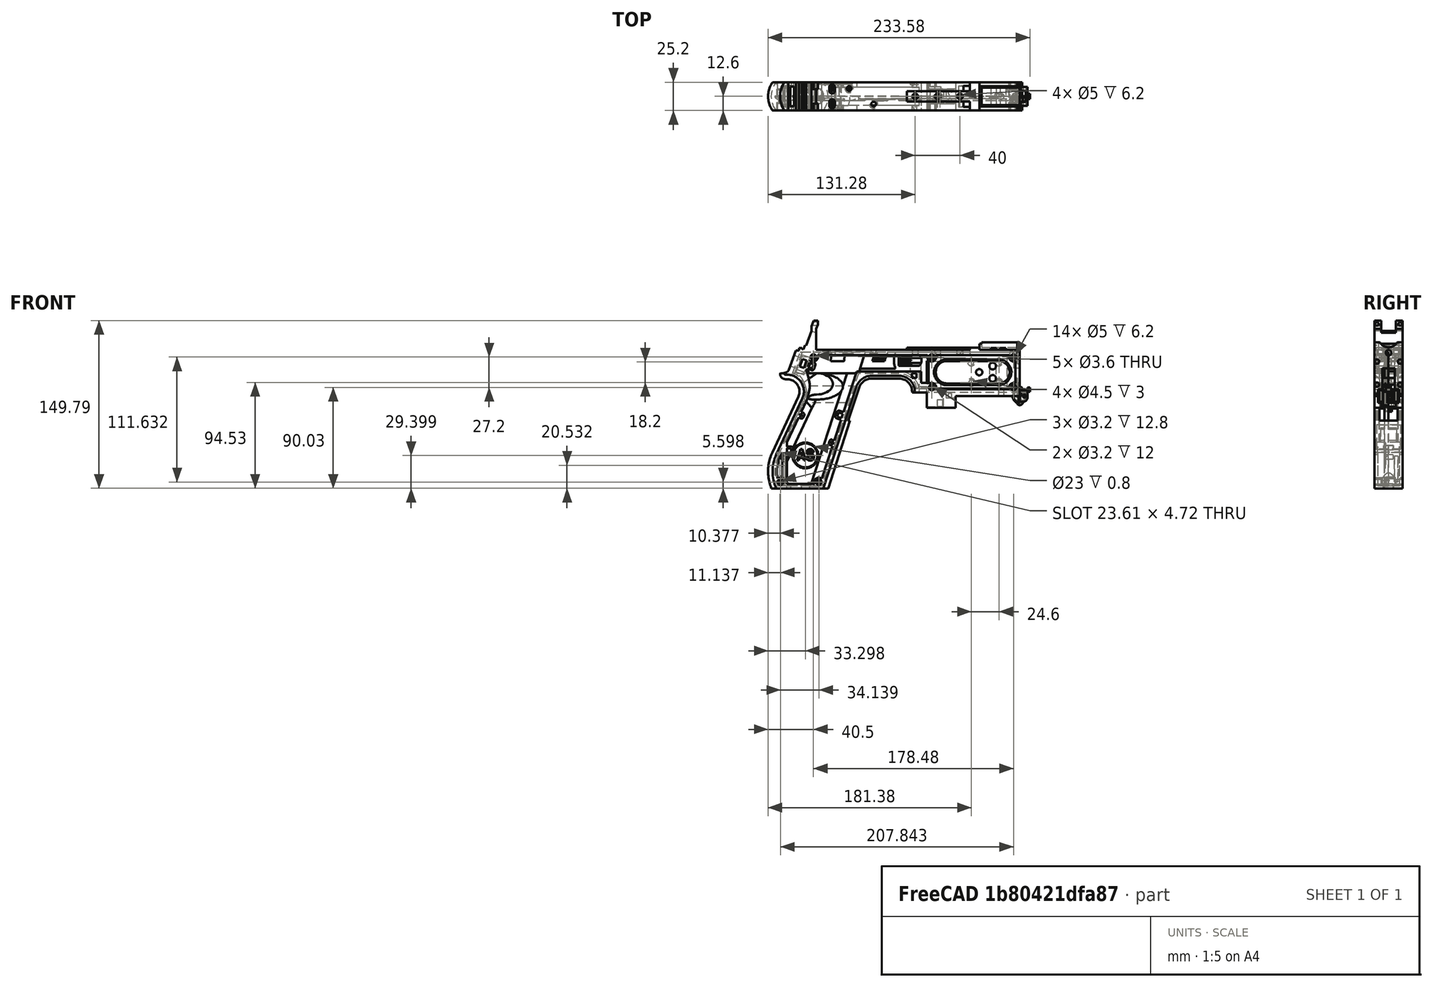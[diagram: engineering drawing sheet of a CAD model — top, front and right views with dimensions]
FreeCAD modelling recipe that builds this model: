
FCSTD DOCUMENT  (FreeCAD 1.0R39319 (Git))
Label: PICON-OF_ver_35
License: All rights reserved
LicenseURL: https://en.wikipedia.org/wiki/All_rights_reserved
objects: Sketcher::SketchObject×106, Part::Extrusion×61, Part::Cut×43, PartDesign::Pad×20, PartDesign::Pocket×14, PartDesign::Chamfer×14, PartDesign::Body×8, PartDesign::Fillet×6, Part::MultiFuse×4, PartDesign::SubtractivePipe×4, Part::Part2DObjectPython×4, PartDesign::SubtractiveLoft×4, PartDesign::Plane×2, PartDesign::SubShapeBinder×2, Part::Sweep×1, PartDesign::ShapeBinder×1, Part::Chamfer×1, Mesh::Feature×1
note: 525 computed .brp shape members not serialized (recipe doc carries the construction recipe); baked Part::Feature solids carry a one-line shape summary decoded from their .brp

FEATURE [Sketcher::SketchObject] Sketch  label="corpo principale"
  ArcFitTolerance = 1e-06
  AttacherType = Attacher::AttachEngine3D
  AttachmentSupport = -> [XZ_Plane]
  FullyConstrained = true
  MakeInternals = false
  MapMode = 5
  Placement = pos=(0,0,0) rot=(1,0,0;1.5708rad)
  sketch-geometry (65):
    g0: LineSegment StartX=0 StartY=0 StartZ=0 EndX=-57.2 EndY=0 EndZ=0
    g1: LineSegment StartX=-57.2 StartY=0 StartZ=0 EndX=-57.2 EndY=-10.4 EndZ=0
    g2: LineSegment StartX=-57.2 StartY=-10.4 StartZ=0 EndX=-82.8 EndY=-10.4 EndZ=0
    g3: LineSegment StartX=-82.8 StartY=-10.4 StartZ=0 EndX=-82.8 EndY=3.2 EndZ=0
    g4: LineSegment StartX=-82.8 StartY=3.2 StartZ=0 EndX=-93.6 EndY=3.2 EndZ=0
    g5: LineSegment StartX=-93.6 StartY=3.2 StartZ=0 EndX=-93.6 EndY=4 EndZ=0
    g6: LineSegment StartX=-107.6 StartY=18 StartZ=0 EndX=-132.428 EndY=18 EndZ=0
    g7: LineSegment StartX=-145.743 StartY=8.32624 StartZ=0 EndX=-175.232 EndY=-82.4316 EndZ=0
    g8: LineSegment StartX=-175.232 StartY=-82.4316 StartZ=0 EndX=-217.232 EndY=-82.4316 EndZ=0
    g9: LineSegment StartX=-217.232 StartY=-52.1862 StartZ=0 EndX=-193.988 EndY=-2.33927 EndZ=0
    g10: LineSegment StartX=-206.196 StartY=23.0857 StartZ=0 EndX=-199.861 EndY=40.4914 EndZ=0
    g11: LineSegment StartX=-199.861 StartY=40.4914 StartZ=0 EndX=-197.061 EndY=40.4914 EndZ=0
    g12: LineSegment StartX=-197.061 StartY=40.4914 StartZ=0 EndX=-197.061 EndY=42.8914 EndZ=0
    g13: LineSegment StartX=-197.061 StartY=42.8914 StartZ=0 EndX=-194.261 EndY=42.8914 EndZ=0
    g14: LineSegment StartX=-194.261 StartY=42.8914 StartZ=0 EndX=-194.535 EndY=42.1397 EndZ=0
    g15: LineSegment StartX=-194.535 StartY=42.1397 StartZ=0 EndX=-193.031 EndY=41.5924 EndZ=0
    g16: LineSegment StartX=-193.031 StartY=41.5924 StartZ=0 EndX=-191.663 EndY=45.3512 EndZ=0
    g17: LineSegment StartX=-191.663 StartY=45.3512 StartZ=0 EndX=-190.536 EndY=44.9408 EndZ=0
    g18: LineSegment StartX=-190.536 StartY=44.9408 StartZ=0 EndX=-185.747 EndY=58.0965 EndZ=0
    g19: LineSegment StartX=-185.747 StartY=58.0965 StartZ=0 EndX=-185.747 EndY=62.0965 EndZ=0
    g20: LineSegment StartX=-185.747 StartY=62.0965 StartZ=0 EndX=-183.832 EndY=67.3588 EndZ=0
    g21: LineSegment StartX=-183.832 StartY=67.3588 StartZ=0 EndX=-180.232 EndY=67.3588 EndZ=0
    g22: LineSegment StartX=-180.232 StartY=67.3588 StartZ=0 EndX=-180.232 EndY=63.7588 EndZ=0
    g23: LineSegment StartX=-180.232 StartY=63.7588 StartZ=0 EndX=-181.6 EndY=60 EndZ=0
    g24: LineSegment StartX=-181.6 StartY=60 StartZ=0 EndX=-181.6 EndY=41.2 EndZ=0
    g25: LineSegment StartX=-181.6 StartY=41.2 StartZ=0 EndX=-100.8 EndY=41.2 EndZ=0
    g26: LineSegment StartX=-36 StartY=43.2 StartZ=0 EndX=-36 EndY=41.2 EndZ=0
    g27: LineSegment StartX=0 StartY=48 StartZ=0 EndX=0 EndY=0 EndZ=0
    g28: LineSegment StartX=-209.901 StartY=19.85 StartZ=0 EndX=-209.901 EndY=20.1 EndZ=0
    g29: LineSegment StartX=-208.001 StartY=22 StartZ=0 EndX=-207.747 EndY=22 EndZ=0
    g30: LineSegment StartX=-207.583 StartY=19 StartZ=0 EndX=-209.051 EndY=19 EndZ=0
    g31: ArcOfCircle CenterX=-208.001 CenterY=20.1 CenterZ=0 NormalX=0 NormalY=0 NormalZ=1 AngleXU=0 Radius=1.9 StartAngle=1.5708 EndAngle=3.14159
    g32: GeomPoint [constr] X=-209.901 Y=22 Z=0
    g33: ArcOfCircle CenterX=-209.051 CenterY=19.85 CenterZ=0 NormalX=0 NormalY=0 NormalZ=1 AngleXU=0 Radius=0.85 StartAngle=3.14159 EndAngle=4.71239
    g34: GeomPoint [constr] X=-209.901 Y=19 Z=0
    g35: ArcOfCircle CenterX=-207.747 CenterY=23.65 CenterZ=0 NormalX=0 NormalY=0 NormalZ=1 AngleXU=0 Radius=1.65 StartAngle=4.71239 EndAngle=5.93412
    g36: GeomPoint [constr] X=-206.591 Y=22 Z=0
    g37: LineSegment StartX=-4 StartY=6 StartZ=0 EndX=-4 EndY=36.4 EndZ=0
    g38: LineSegment StartX=-4 StartY=36.4 StartZ=0 EndX=-185.2 EndY=36.4 EndZ=0
    g39: LineSegment StartX=-185.2 StartY=36.4 StartZ=0 EndX=-190.441 EndY=22 EndZ=0
    g40: LineSegment StartX=-214.575 StartY=-78.4316 StartZ=0 EndX=-178.142 EndY=-78.4316 EndZ=0
    g41: LineSegment StartX=-178.142 StartY=-78.4316 StartZ=0 EndX=-145.51 EndY=22 EndZ=0
    g42: LineSegment StartX=-145.51 StartY=22 StartZ=0 EndX=-87.91 EndY=22 EndZ=0
    g43: LineSegment StartX=-87.91 StartY=22 StartZ=0 EndX=-87.91 EndY=11.6 EndZ=0
    g44: LineSegment StartX=-87.91 StartY=11.6 StartZ=0 EndX=-80.11 EndY=11.6 EndZ=0
    g45: LineSegment StartX=-80.11 StartY=11.6 StartZ=0 EndX=-80.11 EndY=6 EndZ=0
    g46: LineSegment StartX=-80.11 StartY=6 StartZ=0 EndX=-4 EndY=6 EndZ=0
    g47: LineSegment StartX=-190.363 StartY=-4.02975 StartZ=0 EndX=-213.607 EndY=-53.8767 EndZ=0
    g48: ArcOfCircle CenterX=-132.428 CenterY=4 CenterZ=0 NormalX=0 NormalY=0 NormalZ=1 AngleXU=0 Radius=14 StartAngle=1.5708 EndAngle=2.82743
    g49: GeomPoint [constr] X=-142.6 Y=18 Z=0
    g50: ArcOfCircle CenterX=-107.6 CenterY=4 CenterZ=0 NormalX=0 NormalY=0 NormalZ=1 AngleXU=0 Radius=14 StartAngle=0 EndAngle=1.5708
    g51: GeomPoint [constr] X=-93.6 Y=18 Z=0
    g52: ArcOfCircle CenterX=-184.801 CenterY=-67.3089 CenterZ=0 NormalX=0 NormalY=0 NormalZ=1 AngleXU=0 Radius=35.7833 StartAngle=2.70526 EndAngle=3.57792
    g53: ArcOfCircle CenterX=-207.583 CenterY=4 CenterZ=0 NormalX=0 NormalY=0 NormalZ=1 AngleXU=0 Radius=15 StartAngle=5.84685 EndAngle=7.85398
    g54: LineSegment [constr] StartX=-213.607 StartY=-53.8767 StartZ=0 EndX=-217.232 EndY=-52.1862 EndZ=0
    g55: ArcOfCircle CenterX=-184.801 CenterY=-67.3089 CenterZ=0 NormalX=0 NormalY=0 NormalZ=1 AngleXU=0 Radius=31.7833 StartAngle=2.70526 EndAngle=3.49911
    g56: ArcOfCircle CenterX=-218.095 CenterY=8.90192 CenterZ=0 NormalX=0 NormalY=0 NormalZ=1 AngleXU=0 Radius=30.5989 StartAngle=5.84685 EndAngle=6.72553
    g57: LineSegment StartX=-44.6 StartY=43.2 StartZ=0 EndX=-36 EndY=43.2 EndZ=0
    g58: LineSegment StartX=-100.8 StartY=41.2 StartZ=0 EndX=-44.6 EndY=41.2 EndZ=0
    g59: LineSegment StartX=-44.6 StartY=41.2 StartZ=0 EndX=-44.6 EndY=43.2 EndZ=0
    g60: LineSegment StartX=-2.4 StartY=48 StartZ=0 EndX=0 EndY=48 EndZ=0
    g61: LineSegment StartX=-36 StartY=41.2 StartZ=0 EndX=-2.4 EndY=41.2 EndZ=0
    g62: LineSegment StartX=-2.4 StartY=41.2 StartZ=0 EndX=-2.4 EndY=48 EndZ=0
    g63: LineSegment [constr] StartX=-181.6 StartY=36.4 StartZ=0 EndX=-152.209 EndY=36.4 EndZ=0
    g64: LineSegment [constr] StartX=-181.6 StartY=36.4 StartZ=0 EndX=-130.41 EndY=36.4 EndZ=0
  constraints (183):
    c: Coincident(g-1,g0)
    c: PointOnObject(g0,g-1)
    c: Coincident(g0,g1)
    c: Vertical(g1)
    c: Coincident(g1,g2)
    c: Horizontal(g2)
    c: Coincident(g2,g3)
    c: Vertical(g3)
    c: Coincident(g3,g4)
    c: Coincident(g4,g5)
    c: Vertical(g5)
    c: Horizontal(g6)
    c: Coincident(g7,g8)
    c: Horizontal(g8)
    c: Coincident(g10,g11)
    c: Horizontal(g11)
    c: Coincident(g11,g12)
    c: Vertical(g12)
    c: Coincident(g12,g13)
    c: Horizontal(g13)
    c: Coincident(g13,g14)
    c: Coincident(g14,g15)
    c: Coincident(g15,g16)
    c: Coincident(g16,g17)
    c: Coincident(g17,g18)
    c: Coincident(g18,g19)
    c: Vertical(g19)
    c: Coincident(g19,g20)
    c: Coincident(g20,g21)
    c: Horizontal(g21)
    c: Coincident(g21,g22)
    c: Vertical(g22)
    c: Coincident(g22,g23)
    c: Coincident(g23,g24)
    c: Vertical(g24)
    c: Coincident(g24,g25)
    c: Horizontal(g25)
    c: Coincident(g57,g26)
    c: Vertical(g26)
    c: Coincident(g26,g61)
    c: PointOnObject(g60,g-2)
    c: Coincident(g60,g27)
    c: Coincident(g27,g0)
    c: DistanceY(g27,g27) = 48
    c: DistanceY(g1,g1) = 10.4
    c: DistanceX(g0,g0) = 57.2
    c: DistanceX(g2,g2) = 25.6
    c: Horizontal(g4)
    c: DistanceY(g3,g3) = 13.6
    c: DistanceX(g4,g4) = 10.8
    c: DistanceY(g5,g51) = 14.8
    c: DistanceX(g49,g51) = 49
    c: Distance(g7,g49) = 105.6
    c: DistanceX(g61,g60) = 36
    c: DistanceX(g25,g25) = 80.8
    c: DistanceY(g24,g24) = 18.8
    c: DistanceY(g22,g22) = 3.6
    c: Distance(g23) = 4
    c: Angle(g-1,g23) = 1.22173
    c: DistanceX(g21,g21) = 3.6
    c: Distance(g20) = 5.6
    c: Angle(g-1,g20) = 1.22173
    c: DistanceY(g19,g19) = 4
    c: Distance(g18) = 14
    c: Angle(g-1,g18) = 1.22173
    c: Distance(g17) = 1.2
    c: Distance(g16) = 4
    c: Angle(g16) = 1.22173
    c: Perpendicular(g18,g17)
    c: Distance(g15) = 1.6
    c: Perpendicular(g16,g15)
    c: Distance(g14) = 0.8
    c: DistanceX(g13,g13) = 2.8
    c: Perpendicular(g15,g14)
    c: DistanceY(g12,g12) = 2.4
    c: DistanceX(g11,g11) = 2.8
    c: Distance(g9) = 55
    c: Angle(g9,g-1) = 2.00713
    c: Horizontal(g29)
    c: Vertical(g28)
    c: Horizontal(g30)
    c: PointOnObject(g32,g29)
    c: PointOnObject(g32,g28)
    c: Tangent(g29,g31) = 1.5708
    c: Tangent(g28,g31) = 1.5708
    c: PointOnObject(g34,g28)
    c: PointOnObject(g34,g30)
    c: Tangent(g28,g33) = 1.5708
    c: Tangent(g30,g33) = 1.5708
    c: PointOnObject(g36,g29)
    c: PointOnObject(g36,g10)
    c: Tangent(g29,g35) = -1.5708
    c: Tangent(g10,g35) = -1.5708
    c: Angle(g-1,g10) = 1.22173
    c: Radius(g35) = 1.65
    c: Vertical(g37)
    c: Coincident(g37,g38)
    c: Horizontal(g38)
    c: Coincident(g38,g39)
    c: Horizontal(g40)
    c: Coincident(g40,g41)
    c: Coincident(g41,g42)
    c: Horizontal(g42)
    c: Coincident(g42,g43)
    c: Vertical(g43)
    c: Coincident(g43,g44)
    c: Horizontal(g44)
    c: Coincident(g44,g45)
    c: Vertical(g45)
    c: Coincident(g45,g46)
    c: Coincident(g46,g37)
    c: Horizontal(g46)
    c: DistanceY(g0,g37) = 6
    c: DistanceX(g37,g0) = 4
    c: DistanceY(g37,g25) = 4.8
    c: DistanceX(g38,g38) = 181.2
    c: DistanceX(g42,g42) = 57.6
    c: DistanceY(g49,g41) = 4
    c: DistanceX(g41,g49) = 2.91
    c: DistanceY(g43,g43) = 10.4
    c: DistanceX(g44,g44) = 7.8
    c: DistanceY(g7,g40) = 4
    c: Distance(g47) = 55
    c: Angle(g-1,g39) = 1.22173
    c: PointOnObject(g49,g7)
    c: PointOnObject(g49,g6)
    c: Tangent(g7,g48) = -1.5708
    c: Tangent(g6,g48) = -1.5708
    c: PointOnObject(g51,g5)
    c: PointOnObject(g51,g6)
    c: Tangent(g5,g50) = -1.5708
    c: Tangent(g6,g50) = -1.5708
    c: Radius(g50) = 14
    c: Radius(g48) = 14
    c: DistanceX(g8,g8) = 42
    c: Angle(g7,g-1) = 1.88496
    c: Parallel(g41,g7)
    c: Parallel(g47,g9)
    c: Coincident(g52,g8)
    c: Tangent(g52,g9) = 1.5708
    c: DistanceX(g9,g8) = 0
    c: Tangent(g53,g9) = -1.5708
    c: Tangent(g53,g30) = -1.5708
    c: Diameter(g53) = 30
    c: DistanceY(g53,g0) = -4
    c: Coincident(g54,g47)
    c: Distance(g54) = 4
    c: Coincident(g54,g9)
    c: Coincident(g55,g40)
    c: Tangent(g55,g47) = -1.5708
    c: Coincident(g52,g55)
    c: Coincident(g56,g39)
    c: Tangent(g56,g47) = 1.5708
    c: Horizontal(g57)
    c: DistanceX(g57,g57) = 8.6
    c: Coincident(g58,g25)
    c: Horizontal(g58)
    c: Coincident(g59,g58)
    c: Vertical(g59)
    c: DistanceY(g58,g57) = 2
    c: DistanceX(g58,g58) = 56.2
    c: Coincident(g59,g57)
    c: DistanceY(g41,g36) = 0
    c: DistanceY(g36,g39) = 0
    c: DistanceY(g28,g28) = 0.25
    c: DistanceX(g30,g36) = 2.46
    c: DistanceX(g28,g29) = 1.9
    c: Coincident(g62,g60)
    c: Horizontal(g60)
    c: DistanceX(g62,g27) = 2.4
    c: Coincident(g61,g62)
    c: DistanceY(g26,g26) = 2
    c: Vertical(g62)
    c: DistanceY(g61,g60) = 6.8
    c: Horizontal(g61)
    c: Distance(g63) = 29.391
    c: PointOnObject(g63,g38)
    c: PointOnObject(g63,g38)
    c: Distance(g64) = 51.19
    c: PointOnObject(g64,g38)
    c: PointOnObject(g64,g38)
    c: DistanceX(g24,g63) = 0
    c: DistanceX(g24,g64) = 0
FEATURE [Part::Extrusion] Extrude  label="Extrude corpo principale"
  Base = -> Sketch
  Dir = (0,-1,2e-16)
  DirMode = 2
  FaceMakerClass = Part::FaceMakerBullseye
  FaceMakerMode = 3
  LengthFwd = 25.2
  LengthRev = 12.6
  Solid = true
  Symmetric = true
FEATURE [Sketcher::SketchObject] Sketch002  label="scavo grilletto"
  ArcFitTolerance = 1e-06
  AttachmentSupport = -> [XZ_Plane]
  ExternalGeometry = -> [Sketch]
  FullyConstrained = true
  MakeInternals = false
  MapMode = 5
  Placement = pos=(0,0,0) rot=(1,0,0;1.5708rad)
  sketch-geometry (4):
    g0: LineSegment StartX=-89.51 StartY=22 StartZ=0 EndX=-152.71 EndY=22 EndZ=0
    g1: LineSegment StartX=-152.71 StartY=22 StartZ=0 EndX=-167.006 EndY=-22 EndZ=0
    g2: LineSegment StartX=-167.006 StartY=-22 StartZ=0 EndX=-89.51 EndY=-22 EndZ=0
    g3: LineSegment StartX=-89.51 StartY=-22 StartZ=0 EndX=-89.51 EndY=22 EndZ=0
  constraints (12):
    c: Horizontal(g0)
    c: Coincident(g0,g1)
    c: Coincident(g1,g2)
    c: Horizontal(g2)
    c: Coincident(g2,g3)
    c: Coincident(g3,g0)
    c: Vertical(g3)
    c: Angle(g1,g0) = 1.88496
    c: DistanceY(g3,g3) = 44
    c: DistanceX(g0,g0) = 63.2
    c: DistanceX(g0,g-3) = 1.6
    c: DistanceY(g-3,g0) = 0
FEATURE [Sketcher::SketchObject] Sketch004  label="traiettoria arrotondamento impugnatura anteriore"
  ArcFitTolerance = 1e-06
  AttachmentSupport = -> [XZ_Plane]
  ExternalGeometry = -> [Sketch]
  FullyConstrained = true
  MakeInternals = false
  MapMode = 5
  Placement = pos=(0,0,0) rot=(1,0,0;1.5708rad)
  sketch-geometry (13):
    g0: LineSegment StartX=-175.232 StartY=-82.4316 StartZ=0 EndX=-145.743 EndY=8.32624 EndZ=0
    g1: LineSegment StartX=-93.6 StartY=3.2 StartZ=0 EndX=-93.6 EndY=4 EndZ=0
    g2: LineSegment StartX=-132.428 StartY=18 StartZ=0 EndX=-107.6 EndY=18 EndZ=0
    g3: ArcOfCircle CenterX=-132.428 CenterY=4 CenterZ=0 NormalX=0 NormalY=0 NormalZ=1 AngleXU=0 Radius=14 StartAngle=1.5708 EndAngle=2.82743
    g4: ArcOfCircle CenterX=-107.6 CenterY=4 CenterZ=0 NormalX=0 NormalY=0 NormalZ=1 AngleXU=0 Radius=14 StartAngle=0 EndAngle=1.5708
    g5: LineSegment StartX=-175.232 StartY=-82.4316 StartZ=0 EndX=-217.232 EndY=-82.4316 EndZ=0
    g6: LineSegment StartX=-217.232 StartY=-52.1862 StartZ=0 EndX=-193.988 EndY=-2.33927 EndZ=0
    g7: LineSegment StartX=-209.051 StartY=19 StartZ=0 EndX=-207.583 EndY=19 EndZ=0
    g8: LineSegment StartX=-209.901 StartY=20.1 StartZ=0 EndX=-209.901 EndY=19.85 EndZ=0
    g9: ArcOfCircle CenterX=-184.801 CenterY=-67.3089 CenterZ=0 NormalX=0 NormalY=0 NormalZ=1 AngleXU=0 Radius=35.7833 StartAngle=2.70526 EndAngle=3.57792
    g10: ArcOfCircle CenterX=-207.583 CenterY=4 CenterZ=0 NormalX=0 NormalY=0 NormalZ=1 AngleXU=0 Radius=15 StartAngle=5.84685 EndAngle=7.85398
    g11: ArcOfCircle CenterX=-209.051 CenterY=19.85 CenterZ=0 NormalX=0 NormalY=0 NormalZ=1 AngleXU=0 Radius=0.85 StartAngle=3.14159 EndAngle=4.71239
    g12: ArcOfCircle CenterX=-208.001 CenterY=20.1 CenterZ=0 NormalX=0 NormalY=0 NormalZ=1 AngleXU=0 Radius=1.9 StartAngle=1.5708 EndAngle=3.14159
  constraints (26):
    c: Coincident(g0,g-3)
    c: Coincident(g0,g-6)
    c: Coincident(g1,g-8)
    c: Coincident(g1,g-7)
    c: Coincident(g2,g-5)
    c: Coincident(g2,g-4)
    c: Coincident(g3,g2)
    c: Tangent(g3,g0) = 1.5708
    c: Coincident(g4,g1)
    c: Tangent(g4,g2) = 1.5708
    c: Coincident(g5,g0)
    c: Coincident(g5,g-9)
    c: Coincident(g6,g-12)
    c: Coincident(g6,g-11)
    c: Coincident(g7,g-15)
    c: Coincident(g7,g-14)
    c: Coincident(g8,g-16)
    c: Coincident(g8,g-17)
    c: Tangent(g9,g6) = 1.5708
    c: Coincident(g9,g5)
    c: Coincident(g10,g7)
    c: Tangent(g10,g6) = -1.5708
    c: Tangent(g11,g7) = -1.5708
    c: Coincident(g11,g8)
    c: Tangent(g12,g8) = -1.5708
    c: Coincident(g12,g-17)
FEATURE [PartDesign::Plane] DatumPlane  label="Piano per disegno arrotondamento impugnatura"
  AttachmentSupport = -> [Sketch]
  Length = 68.5841
  MapMode = 7
  Placement = pos=(-145.743,1.8e-15,8.32624) rot=(0.154555,0.154555,0.97582;1.59527rad)
  ResizeMode = 0
  Width = 191.269
FEATURE [Sketcher::SketchObject] Sketch005  label="forma arrotondamento impugnatura anteriore"
  ArcFitTolerance = 1e-06
  AttachmentSupport = -> [DatumPlane]
  FullyConstrained = true
  MakeInternals = false
  MapMode = 5
  Placement = pos=(-145.743,1.8e-15,8.32624) rot=(0.154555,0.154555,0.97582;1.59527rad)
  sketch-geometry (5):
    g0: GeomPoint [constr] X=0 Y=-4 Z=0
    g1: GeomPoint [constr] X=-12.6 Y=7.1e-15 Z=0
    g2: GeomPoint [constr] X=12.6 Y=4.97e-14 Z=0
    g3: LineSegment StartX=-12.6 StartY=7.1e-15 StartZ=0 EndX=12.6 EndY=4.97e-14 EndZ=0
    g4: ArcOfCircle CenterX=-3.88e-14 CenterY=17.845 CenterZ=0 NormalX=0 NormalY=0 NormalZ=1 AngleXU=0 Radius=21.845 StartAngle=4.09759 EndAngle=5.32718
  constraints (11):
    c: DistanceY(g0,g-1) = 4
    c: DistanceX(g-1,g0) = 0
    c: DistanceX(g1,g-1) = 12.6
    c: DistanceX(g-1,g2) = 12.6
    c: DistanceY(g-1,g2) = 0
    c: DistanceY(g-1,g1) = 0
    c: Coincident(g3,g1)
    c: Coincident(g3,g2)
    c: Coincident(g4,g1)
    c: Coincident(g4,g2)
    c: PointOnObject(g0,g4)
FEATURE [Part::Sweep] Sweep  label="Sweep impugnatura"
  Frenet = true
  Sections = -> [Sketch005]
  Solid = true
  Spine = -> Sketch [Edge32,Edge33,Edge34,Edge35,Edge36,Edge37,Edge38,Edge39,Edge40,Edge41,Edge42,Edge43,Edge44]
  Transition = 1
FEATURE [Sketcher::SketchObject] Sketch008  label="buchi e pulizie varie"
  ArcFitTolerance = 1e-06
  AttachmentSupport = -> [XZ_Plane]
  ExternalGeometry = -> [Sketch]
  FullyConstrained = true
  MakeInternals = false
  MapMode = 5
  Placement = pos=(0,0,0) rot=(1,0,0;1.5708rad)
  sketch-geometry (26):
    g0: LineSegment StartX=-96.278 StartY=20.155 StartZ=0 EndX=-92.278 EndY=20.155 EndZ=0
    g1: LineSegment StartX=-92.278 StartY=20.155 StartZ=0 EndX=-92.278 EndY=16.155 EndZ=0
    g2: LineSegment StartX=-92.278 StartY=16.155 StartZ=0 EndX=-96.278 EndY=16.155 EndZ=0
    g3: LineSegment StartX=-96.278 StartY=16.155 StartZ=0 EndX=-96.278 EndY=20.155 EndZ=0
    g4: LineSegment StartX=-222.232 StartY=-82.4316 StartZ=0 EndX=-170.232 EndY=-82.4316 EndZ=0
    g5: LineSegment StartX=-170.232 StartY=-82.4316 StartZ=0 EndX=-170.232 EndY=-86.4316 EndZ=0
    g6: LineSegment StartX=-170.232 StartY=-86.4316 StartZ=0 EndX=-222.232 EndY=-86.4316 EndZ=0
    g7: LineSegment StartX=-222.232 StartY=-86.4316 StartZ=0 EndX=-222.232 EndY=-82.4316 EndZ=0
    g8: LineSegment StartX=-213.901 StartY=20.1 StartZ=0 EndX=-213.901 EndY=26 EndZ=0
    g9: LineSegment StartX=-213.901 StartY=26 StartZ=0 EndX=-206.196 EndY=26 EndZ=0
    g10: LineSegment StartX=-17.4 StartY=42.8 StartZ=0 EndX=-12.4 EndY=42.8 EndZ=0
    g11: LineSegment StartX=-12.4 StartY=42.8 StartZ=0 EndX=-12.4 EndY=41.2 EndZ=0
    g12: LineSegment StartX=-12.4 StartY=41.2 StartZ=0 EndX=-17.4 EndY=41.2 EndZ=0
    g13: LineSegment StartX=-17.4 StartY=41.2 StartZ=0 EndX=-17.4 EndY=42.8 EndZ=0
    g14: LineSegment StartX=-25.9 StartY=42.8 StartZ=0 EndX=-20.9 EndY=42.8 EndZ=0
    g15: LineSegment StartX=-20.9 StartY=42.8 StartZ=0 EndX=-20.9 EndY=41.2 EndZ=0
    g16: LineSegment StartX=-20.9 StartY=41.2 StartZ=0 EndX=-25.9 EndY=41.2 EndZ=0
    g17: LineSegment StartX=-25.9 StartY=41.2 StartZ=0 EndX=-25.9 EndY=42.8 EndZ=0
    g18: GeomPoint [constr] X=-206.196 Y=23.0857 Z=0
    g19: GeomPoint [constr] X=-213.901 Y=20.1 Z=0
    g20: BSplineCurve PolesCount=4 KnotsCount=2 Degree=3 IsPeriodic=0
    g21-g24: Circle [constr] x4 (B-spline internal-alignment scaffolding for g20; pole/knot coordinates omitted)
    g25: LineSegment StartX=-206.196 StartY=26 StartZ=0 EndX=-206.196 EndY=23.0857 EndZ=0
  constraints (73):
    c: Horizontal(g0)
    c: Coincident(g1,g0)
    c: Vertical(g1)
    c: Coincident(g2,g1)
    c: Horizontal(g2)
    c: Coincident(g3,g2)
    c: Coincident(g3,g0)
    c: Vertical(g3)
    c: DistanceX(g0,g-4) = 4.368
    c: DistanceY(g0,g-4) = 1.845
    c: DistanceY(g1,g1) = 4
    c: DistanceX(g2,g2) = 4
    c: Horizontal(g4)
    c: Coincident(g5,g4)
    c: Vertical(g5)
    c: Coincident(g6,g5)
    c: Horizontal(g6)
    c: Coincident(g7,g6)
    c: Coincident(g7,g4)
    c: Vertical(g7)
    c: DistanceY(g7,g7) = 4
    c: DistanceX(g4,g-5) = 5
    c: DistanceX(g-5,g4) = 5
    c: DistanceY(g4,g-5) = 0
    c: Coincident(g9,g8)
    c: Parallel(g9,g-6)
    c: DistanceX(g8,g-8) = 4
    c: Horizontal(g10)
    c: Coincident(g11,g10)
    c: Vertical(g11)
    c: Coincident(g12,g11)
    c: Horizontal(g12)
    c: Coincident(g13,g12)
    c: Coincident(g13,g10)
    c: Vertical(g13)
    c: Horizontal(g14)
    c: Coincident(g15,g14)
    c: Vertical(g15)
    c: Coincident(g16,g15)
    c: Horizontal(g16)
    c: Coincident(g17,g16)
    c: Coincident(g17,g14)
    c: Vertical(g17)
    c: DistanceY(g11,g10) = 1.6
    c: DistanceX(g10,g10) = 5
    c: DistanceY(g15,g14) = 1.6
    c: DistanceX(g14,g14) = 5
    c: DistanceX(g15,g12) = 3.5
    c: DistanceX(g11,g-9) = 10
    c: DistanceY(g-9,g11) = 0
    c: DistanceY(g-9,g15) = 0
    c: Perpendicular(g8,g9)
    c: DistanceY(g-7,g9) = 4
    c: DistanceY(g8,g-8) = 0
    c: InternalAlignment(g18,g20)
    c: InternalAlignment(g19,g20)
    c: InternalAlignment(g21,g20)
    c: Weight(g21) = 1
    c: InternalAlignment(g22,g20)
    c: Equal(g22,g21)
    c: InternalAlignment(g23,g20)
    c: Equal(g23,g21)
    c: InternalAlignment(g24,g20)
    c: Equal(g24,g21)
    c: Coincident(g18,g-12)
    c: Coincident(g19,g8)
    c: Coincident(g25,g9)
    c: Coincident(g25,g20)
    c: Vertical(g25)
    c: DistanceY(g20,g23) = 0
    c: DistanceY(g22,g18) = 2.26
    c: DistanceX(g22,g18) = 0.93
    c: DistanceX(g20,g23) = 2.9
FEATURE [Part::Extrusion] Extrude004  label="Extrude Buchi e pulizie varie"
  Base = -> Sketch008
  Dir = (0,-1,2e-16)
  DirMode = 2
  FaceMakerClass = Part::FaceMakerBullseye
  FaceMakerMode = 3
  LengthFwd = 25.2
  LengthRev = 0
  Solid = true
  Symmetric = true
FEATURE [Sketcher::SketchObject] Sketch009  label="rinforzi"
  ArcFitTolerance = 1e-06
  AttachmentSupport = -> [XZ_Plane]
  ExternalGeometry = -> [Sketch]
  FullyConstrained = true
  MakeInternals = false
  MapMode = 5
  Placement = pos=(0,0,0) rot=(1,0,0;1.5708rad)
  sketch-geometry (9):
    g0: LineSegment StartX=-87.91 StartY=22 StartZ=0 EndX=-87.91 EndY=36.4 EndZ=0
    g1: LineSegment StartX=-87.91 StartY=36.4 StartZ=0 EndX=-97.91 EndY=36.4 EndZ=0
    g2: LineSegment StartX=-97.91 StartY=36.4 StartZ=0 EndX=-97.91 EndY=22 EndZ=0
    g3: LineSegment StartX=-97.91 StartY=22 StartZ=0 EndX=-87.91 EndY=22 EndZ=0
    g4: LineSegment StartX=-149.713 StartY=9.06563 StartZ=0 EndX=-154.586 EndY=-5.93437 EndZ=0
    g5: LineSegment StartX=-154.586 StartY=-5.93437 StartZ=0 EndX=-191.863 EndY=-5.93437 EndZ=0
    g6: LineSegment StartX=-191.863 StartY=-5.93437 StartZ=0 EndX=-191.863 EndY=9.06563 EndZ=0
    g7: LineSegment StartX=-191.863 StartY=9.06563 StartZ=0 EndX=-149.713 EndY=9.06563 EndZ=0
    g8: LineSegment [constr] StartX=-145.51 StartY=22 StartZ=0 EndX=-149.713 EndY=9.06563 EndZ=0
  constraints (25):
    c: Vertical(g0)
    c: Coincident(g1,g0)
    c: Horizontal(g1)
    c: Coincident(g2,g1)
    c: Vertical(g2)
    c: Coincident(g3,g2)
    c: Coincident(g3,g0)
    c: Horizontal(g3)
    c: Coincident(g0,g-4)
    c: DistanceX(g3,g3) = 10
    c: DistanceY(g0,g-3) = 0
    c: Coincident(g5,g4)
    c: Horizontal(g5)
    c: Coincident(g6,g5)
    c: Vertical(g6)
    c: Coincident(g7,g6)
    c: Coincident(g7,g4)
    c: Horizontal(g7)
    c: Distance(g8) = 13.6
    c: Parallel(g-6,g8)
    c: Coincident(g-6,g8)
    c: Parallel(g4,g-6)
    c: DistanceY(g4,g4) = 15
    c: Coincident(g4,g8)
    c: DistanceX(g-5,g5) = -1.5
FEATURE [Part::Extrusion] Extrude001  label="Extrude scavo grilletto"
  Base = -> Sketch002
  Dir = (0,-1,2e-16)
  DirMode = 2
  FaceMakerClass = Part::FaceMakerBullseye
  FaceMakerMode = 3
  LengthFwd = 16
  LengthRev = 0
  Solid = true
  Symmetric = true
FEATURE [Part::Extrusion] Extrude005  label="Extrude Rinforzi"
  Base = -> Sketch009
  Dir = (0,-1,2e-16)
  DirMode = 2
  FaceMakerClass = Part::FaceMakerBullseye
  FaceMakerMode = 3
  LengthFwd = 2
  LengthRev = 0
  Placement = pos=(0,12.6,0) rot=(0,0,1;0rad)
  Solid = true
  Symmetric = false
FEATURE [PartDesign::ShapeBinder] CopyCut
  TraceSupport = false
FEATURE [PartDesign::Plane] DatumPlane001
  AttachmentSupport = -> [CopyCut]
  Length = 60
  MapMode = 5
  Placement = pos=(0,12.6,0) rot=(0,0.707107,0.707107;3.14159rad)
  ResizeMode = 0
  Width = 60
FEATURE [Sketcher::SketchObject] Sketch010  label="buco neopixel"
  ArcFitTolerance = 1e-06
  AttachmentSupport = -> [XZ_Plane]
  ExternalGeometry = -> [Sketch]
  FullyConstrained = true
  MakeInternals = false
  MapMode = 5
  Placement = pos=(0,0,0) rot=(1,0,0;1.5708rad)
  sketch-geometry (5):
    g0: LineSegment [constr] StartX=-199.861 StartY=40.4914 StartZ=0 EndX=-201.368 EndY=36.3521 EndZ=0
    g1: LineSegment StartX=-201.368 StartY=36.3521 StartZ=0 EndX=-204.932 EndY=26.5605 EndZ=0
    g2: LineSegment StartX=-201.368 StartY=36.3521 StartZ=0 EndX=-180.2 EndY=28.6477 EndZ=0
    g3: LineSegment StartX=-180.2 StartY=28.6477 StartZ=0 EndX=-183.764 EndY=18.8561 EndZ=0
    g4: LineSegment StartX=-183.764 StartY=18.8561 StartZ=0 EndX=-204.932 EndY=26.5605 EndZ=0
  constraints (14):
    c: Parallel(g0,g-3)
    c: Distance(g0) = 4.405
    c: Coincident(g0,g-3)
    c: Coincident(g2,g1)
    c: Coincident(g3,g2)
    c: Coincident(g4,g3)
    c: Coincident(g4,g1)
    c: Parallel(g1,g-3)
    c: Distance(g1) = 10.42
    c: Coincident(g1,g0)
    c: Parallel(g2,g4)
    c: Perpendicular(g1,g2)
    c: DistanceX(g-4,g2) = 5
    c: Parallel(g3,g1)
FEATURE [Part::Extrusion] Extrude006  label="Extrude buco neopixel"
  Base = -> Sketch010
  Dir = (0,-1,2e-16)
  DirMode = 2
  FaceMakerClass = Part::FaceMakerBullseye
  FaceMakerMode = 3
  LengthFwd = 17.2
  LengthRev = 0
  Solid = true
  Symmetric = true
FEATURE [Sketcher::SketchObject] Sketch011  label="fermo grilletto"
  ArcFitTolerance = 1e-06
  AttachmentSupport = -> [XZ_Plane]
  ExternalGeometry = -> [Sketch]
  FullyConstrained = true
  MakeInternals = false
  MapMode = 5
  Placement = pos=(0,0,0) rot=(1,0,0;1.5708rad)
  sketch-geometry (18):
    g0: LineSegment [constr] StartX=-145.51 StartY=22 StartZ=0 EndX=-157.347 EndY=-14.4293 EndZ=0
    g1: LineSegment [constr] StartX=-157.347 StartY=-14.4293 StartZ=0 EndX=-157.841 EndY=-15.951 EndZ=0
    g2: LineSegment StartX=-161.151 StartY=-13.1932 StartZ=0 EndX=-155.825 EndY=-14.9237 EndZ=0
    g3: LineSegment StartX=-163.167 StartY=-14.2205 StartZ=0 EndX=-164.403 EndY=-18.0247 EndZ=0
    g4: LineSegment StartX=-163.376 StartY=-20.0408 StartZ=0 EndX=-158.05 EndY=-21.7713 EndZ=0
    g5: LineSegment StartX=-158.05 StartY=-21.7713 StartZ=0 EndX=-155.825 EndY=-14.9237 EndZ=0
    g6: LineSegment StartX=-161.645 StartY=-14.7149 StartZ=0 EndX=-157.841 EndY=-15.951 EndZ=0
    g7: LineSegment StartX=-157.841 StartY=-15.951 StartZ=0 EndX=-159.077 EndY=-19.7552 EndZ=0
    g8: LineSegment StartX=-159.077 StartY=-19.7552 StartZ=0 EndX=-162.881 EndY=-18.5191 EndZ=0
    g9: LineSegment StartX=-162.881 StartY=-18.5191 StartZ=0 EndX=-161.645 EndY=-14.7149 EndZ=0
    g10: LineSegment [constr] StartX=-161.645 StartY=-14.7149 StartZ=0 EndX=-161.151 EndY=-13.1932 EndZ=0
    g11: LineSegment [constr] StartX=-159.077 StartY=-19.7552 StartZ=0 EndX=-157.555 EndY=-20.2496 EndZ=0
    g12: LineSegment [constr] StartX=-159.077 StartY=-19.7552 StartZ=0 EndX=-159.572 EndY=-21.2769 EndZ=0
    g13: LineSegment [constr] StartX=-161.645 StartY=-14.7149 StartZ=0 EndX=-163.167 EndY=-14.2205 EndZ=0
    g14: ArcOfCircle CenterX=-161.645 CenterY=-14.7149 CenterZ=0 NormalX=0 NormalY=0 NormalZ=1 AngleXU=0 Radius=1.6 StartAngle=1.25664 EndAngle=2.82743
    g15: GeomPoint [constr] X=-162.673 Y=-12.6988 Z=0
    g16: ArcOfCircle CenterX=-162.881 CenterY=-18.5191 CenterZ=0 NormalX=0 NormalY=0 NormalZ=1 AngleXU=0 Radius=1.6 StartAngle=2.82743 EndAngle=4.39823
    g17: GeomPoint [constr] X=-164.897 Y=-19.5464 Z=0
  constraints (48):
    c: Parallel(g0,g-3)
    c: Distance(g0) = 38.304
    c: Coincident(g0,g-3)
    c: Parallel(g1,g-3)
    c: Distance(g1) = 1.6
    c: Coincident(g1,g0)
    c: Coincident(g5,g4)
    c: Coincident(g5,g2)
    c: Coincident(g7,g6)
    c: Coincident(g8,g7)
    c: Coincident(g9,g8)
    c: Coincident(g9,g6)
    c: Parallel(g7,g-3)
    c: Parallel(g9,g7)
    c: Perpendicular(g6,g7)
    c: Parallel(g6,g8)
    c: Distance(g6) = 4
    c: Distance(g9) = 4
    c: Parallel(g5,g7)
    c: Parallel(g9,g3)
    c: Parallel(g2,g6)
    c: Parallel(g4,g8)
    c: Parallel(g13,g6)
    c: Parallel(g10,g9)
    c: Parallel(g11,g8)
    c: Parallel(g12,g7)
    c: Distance(g10) = 1.6
    c: Distance(g13) = 1.6
    c: Distance(g12) = 1.6
    c: Distance(g11) = 1.6
    c: Coincident(g10,g6)
    c: Coincident(g13,g6)
    c: Coincident(g12,g7)
    c: Coincident(g11,g7)
    c: Distance(g10,g15) = 1.6
    c: Distance(g15,g13) = 1.6
    c: Distance(g4,g12) = 1.6
    c: Distance(g4,g11) = 1.6
    c: PointOnObject(g15,g2)
    c: Tangent(g3,g14) = -1.5708
    c: Tangent(g2,g14) = 1.5708
    c: PointOnObject(g17,g4)
    c: PointOnObject(g17,g3)
    c: Tangent(g4,g16) = -1.5708
    c: Tangent(g3,g16) = -1.5708
    c: Equal(g16,g14)
    c: Coincident(g16,g8)
    c: Coincident(g6,g1)
FEATURE [Part::Extrusion] Extrude007  label="Extrude fermo grilletto"
  Base = -> Sketch011
  Dir = (0,-1,2e-16)
  DirMode = 2
  FaceMakerClass = Part::FaceMakerBullseye
  FaceMakerMode = 3
  LengthFwd = 25.2
  LengthRev = 0
  Solid = true
  Symmetric = true
FEATURE [Sketcher::SketchObject] Sketch012  label="buco oled"
  ArcFitTolerance = 1e-06
  AttachmentSupport = -> [XZ_Plane]
  ExternalGeometry = -> [Sketch]
  FullyConstrained = true
  MakeInternals = false
  MapMode = 5
  Placement = pos=(0,0,0) rot=(1,0,0;1.5708rad)
  sketch-geometry (4):
    g0: LineSegment StartX=-185.747 StartY=58.0965 StartZ=0 EndX=-180.232 EndY=56.0891 EndZ=0
    g1: LineSegment StartX=-185.747 StartY=58.0965 StartZ=0 EndX=-185.747 EndY=67.3588 EndZ=0
    g2: LineSegment StartX=-185.747 StartY=67.3588 StartZ=0 EndX=-180.232 EndY=67.3588 EndZ=0
    g3: LineSegment StartX=-180.232 StartY=67.3588 StartZ=0 EndX=-180.232 EndY=56.0891 EndZ=0
  constraints (10):
    c: Coincident(g1,g0)
    c: Coincident(g2,g1)
    c: Coincident(g3,g2)
    c: Coincident(g3,g0)
    c: Parallel(g1,g-5)
    c: Perpendicular(g-3,g0)
    c: Parallel(g2,g-6)
    c: Parallel(g3,g-4)
    c: Coincident(g0,g-5)
    c: Coincident(g2,g-6)
FEATURE [Part::Extrusion] Extrude008  label="Extrude buco oled"
  Base = -> Sketch012
  Dir = (0,-1,2e-16)
  DirMode = 2
  FaceMakerClass = Part::FaceMakerBullseye
  FaceMakerMode = 3
  LengthFwd = 12.8
  LengthRev = 0
  Solid = true
  Symmetric = true
FEATURE [Sketcher::SketchObject] Sketch013  label="buco pompa"
  ArcFitTolerance = 1e-06
  AttachmentSupport = -> [XZ_Plane]
  ExternalGeometry = -> [Sketch]
  FullyConstrained = true
  MakeInternals = false
  MapMode = 5
  Placement = pos=(0,0,0) rot=(1,0,0;1.5708rad)
  sketch-geometry (8):
    g0: LineSegment StartX=-82.8 StartY=-10.4 StartZ=0 EndX=-82.8 EndY=-9.6 EndZ=0
    g1: LineSegment StartX=-82.8 StartY=-9.6 StartZ=0 EndX=-67.9 EndY=-9.6 EndZ=0
    g2: LineSegment StartX=-67.9 StartY=-9.6 StartZ=0 EndX=-67.9 EndY=6 EndZ=0
    g3: LineSegment StartX=-67.9 StartY=6 StartZ=0 EndX=-65.9 EndY=6 EndZ=0
    g4: LineSegment StartX=-65.9 StartY=6 StartZ=0 EndX=-65.9 EndY=-1.7 EndZ=0
    g5: LineSegment StartX=-65.9 StartY=-1.7 StartZ=0 EndX=-57.2 EndY=-1.7 EndZ=0
    g6: LineSegment StartX=-57.2 StartY=-1.7 StartZ=0 EndX=-57.2 EndY=-10.4 EndZ=0
    g7: LineSegment StartX=-57.2 StartY=-10.4 StartZ=0 EndX=-82.8 EndY=-10.4 EndZ=0
  constraints (22):
    c: Vertical(g0)
    c: Coincident(g1,g0)
    c: Horizontal(g1)
    c: Coincident(g2,g1)
    c: Vertical(g2)
    c: Coincident(g3,g2)
    c: Horizontal(g3)
    c: Coincident(g4,g3)
    c: Vertical(g4)
    c: Coincident(g5,g4)
    c: Horizontal(g5)
    c: Coincident(g6,g5)
    c: Vertical(g6)
    c: Coincident(g7,g6)
    c: Coincident(g7,g0)
    c: DistanceY(g0,g0) = 0.8
    c: DistanceY(g6,g6) = 8.7
    c: DistanceX(g1,g1) = 14.9
    c: DistanceX(g3,g3) = 2
    c: Coincident(g0,g-4)
    c: DistanceY(g2,g-6) = 0
    c: Coincident(g6,g-5)
FEATURE [Part::Extrusion] Extrude009  label="Extrude buco pompa"
  Base = -> Sketch013
  Dir = (0,-1,2e-16)
  DirMode = 2
  FaceMakerClass = Part::FaceMakerBullseye
  FaceMakerMode = 3
  LengthFwd = 13.2
  LengthRev = 0
  Solid = true
  Symmetric = true
FEATURE [Sketcher::SketchObject] Sketch014  label="buco frontale"
  ArcFitTolerance = 1e-06
  AttachmentSupport = -> [XZ_Plane]
  ExternalGeometry = -> [Sketch]
  FullyConstrained = true
  MakeInternals = false
  MapMode = 5
  Placement = pos=(0,0,0) rot=(1,0,0;1.5708rad)
  sketch-geometry (10):
    g0: LineSegment StartX=0 StartY=0 StartZ=0 EndX=0 EndY=24.671 EndZ=0
    g1: LineSegment StartX=0 StartY=24.671 StartZ=0 EndX=-4 EndY=24.671 EndZ=0
    g2: LineSegment StartX=-4 StartY=24.671 StartZ=0 EndX=-4 EndY=16 EndZ=0
    g3: LineSegment StartX=-4 StartY=16 StartZ=0 EndX=-2.4 EndY=16 EndZ=0
    g4: LineSegment StartX=-2.4 StartY=16 StartZ=0 EndX=-2.4 EndY=10 EndZ=0
    g5: LineSegment StartX=-2.4 StartY=10 StartZ=0 EndX=-12 EndY=10 EndZ=0
    g6: LineSegment StartX=-12 StartY=10 StartZ=0 EndX=-12 EndY=6 EndZ=0
    g7: LineSegment StartX=-12 StartY=6 StartZ=0 EndX=-2.4 EndY=6 EndZ=0
    g8: LineSegment StartX=-2.4 StartY=6 StartZ=0 EndX=-2.4 EndY=0 EndZ=0
    g9: LineSegment StartX=-2.4 StartY=0 StartZ=0 EndX=0 EndY=0 EndZ=0
  constraints (29):
    c: Vertical(g0)
    c: Coincident(g1,g0)
    c: Horizontal(g1)
    c: Coincident(g2,g1)
    c: Vertical(g2)
    c: Coincident(g3,g2)
    c: Horizontal(g3)
    c: Coincident(g4,g3)
    c: Vertical(g4)
    c: Coincident(g5,g4)
    c: Horizontal(g5)
    c: Coincident(g6,g5)
    c: Vertical(g6)
    c: Coincident(g7,g6)
    c: Coincident(g8,g7)
    c: Vertical(g8)
    c: Coincident(g9,g8)
    c: Coincident(g9,g0)
    c: Horizontal(g9)
    c: DistanceY(g0,g0) = 24.671
    c: Horizontal(g7)
    c: DistanceY(g6,g6) = 4
    c: DistanceY(g4,g4) = 6
    c: DistanceX(g9,g9) = 2.4
    c: Coincident(g0,g-1)
    c: DistanceY(g-3,g7) = 0
    c: DistanceX(g8,g4) = 0
    c: DistanceX(g-3,g1) = 0
    c: DistanceX(g6,g-3) = 8
FEATURE [Part::Extrusion] Extrude010  label="Extrude buco frontale"
  Base = -> Sketch014
  Dir = (0,-1,2e-16)
  DirMode = 2
  FaceMakerClass = Part::FaceMakerBullseye
  FaceMakerMode = 3
  LengthFwd = 11.2
  LengthRev = 0
  Solid = true
  Symmetric = true
FEATURE [Sketcher::SketchObject] Sketch015  label="guida rail"
  ArcFitTolerance = 1e-06
  AttachmentSupport = -> [XZ_Plane]
  ExternalGeometry = -> [Sketch]
  FullyConstrained = true
  MakeInternals = false
  MapMode = 5
  Placement = pos=(0,0,0) rot=(1,0,0;1.5708rad)
  sketch-geometry (4):
    g0: LineSegment StartX=-100.8 StartY=43.2 StartZ=0 EndX=-44.6 EndY=43.2 EndZ=0
    g1: LineSegment StartX=-44.6 StartY=43.2 StartZ=0 EndX=-44.6 EndY=41.2 EndZ=0
    g2: LineSegment StartX=-44.6 StartY=41.2 StartZ=0 EndX=-100.8 EndY=41.2 EndZ=0
    g3: LineSegment StartX=-100.8 StartY=41.2 StartZ=0 EndX=-100.8 EndY=43.2 EndZ=0
  constraints (9):
    c: Horizontal(g0)
    c: Coincident(g1,g0)
    c: Coincident(g2,g1)
    c: Coincident(g3,g2)
    c: Coincident(g3,g0)
    c: Vertical(g3)
    c: Coincident(g2,g-3)
    c: Coincident(g1,g-3)
    c: Coincident(g0,g-4)
FEATURE [Part::Extrusion] Extrude011  label="Extrude guida rail"
  Base = -> Sketch015
  Dir = (0,-1,2e-16)
  DirMode = 2
  FaceMakerClass = Part::FaceMakerBullseye
  FaceMakerMode = 3
  LengthFwd = 9
  LengthRev = 0
  Solid = true
  Symmetric = true
FEATURE [Sketcher::SketchObject] Sketch016  label="guide per coperture laterali"
  ArcFitTolerance = 1e-06
  AttachmentSupport = -> [XZ_Plane]
  ExternalGeometry = -> [Sketch]
  FullyConstrained = true
  MakeInternals = false
  MapMode = 5
  Placement = pos=(0,0,0) rot=(1,0,0;1.5708rad)
  sketch-geometry (14):
    g0: Circle CenterX=-5.6 CenterY=7.6 CenterZ=0 NormalX=0 NormalY=0 NormalZ=1 AngleXU=0 Radius=1.6
    g1: Circle CenterX=-5.6 CenterY=7.6 CenterZ=0 NormalX=0 NormalY=0 NormalZ=1 AngleXU=0 Radius=4
    g2: Circle CenterX=-5.6 CenterY=34.8 CenterZ=0 NormalX=0 NormalY=0 NormalZ=1 AngleXU=0 Radius=1.6
    g3: Circle CenterX=-5.6 CenterY=34.8 CenterZ=0 NormalX=0 NormalY=0 NormalZ=1 AngleXU=0 Radius=4
    g4: Circle CenterX=-184.08 CenterY=34.8 CenterZ=0 NormalX=0 NormalY=0 NormalZ=1 AngleXU=0 Radius=1.6
    g5: Circle CenterX=-184.08 CenterY=34.8 CenterZ=0 NormalX=0 NormalY=0 NormalZ=1 AngleXU=0 Radius=4
    g6: Circle CenterX=-179.305 CenterY=-76.8316 CenterZ=0 NormalX=0 NormalY=0 NormalZ=1 AngleXU=0 Radius=1.6
    g7: Circle CenterX=-179.305 CenterY=-76.8316 CenterZ=0 NormalX=0 NormalY=0 NormalZ=1 AngleXU=0 Radius=4
    g8: Circle CenterX=-213.443 CenterY=-76.8316 CenterZ=0 NormalX=0 NormalY=0 NormalZ=1 AngleXU=0 Radius=1.6
    g9: Circle CenterX=-213.443 CenterY=-76.8316 CenterZ=0 NormalX=0 NormalY=0 NormalZ=1 AngleXU=0 Radius=4
    g10: Circle CenterX=-78.51 CenterY=7.6 CenterZ=0 NormalX=0 NormalY=0 NormalZ=1 AngleXU=0 Radius=1.6
    g11: Circle CenterX=-78.51 CenterY=7.6 CenterZ=0 NormalX=0 NormalY=0 NormalZ=1 AngleXU=0 Radius=4
    g12: Circle CenterX=-78.51 CenterY=34.8 CenterZ=0 NormalX=0 NormalY=0 NormalZ=1 AngleXU=0 Radius=1.6
    g13: Circle CenterX=-78.51 CenterY=34.8 CenterZ=0 NormalX=0 NormalY=0 NormalZ=1 AngleXU=0 Radius=4
  constraints (35):
    c: Diameter(g0) = 3.2
    c: Diameter(g1) = 8
    c: Coincident(g0,g1)
    c: Diameter(g2) = 3.2
    c: Diameter(g3) = 8
    c: Coincident(g3,g2)
    c: Tangent(g2,g-7)
    c: Diameter(g4) = 3.2
    c: Diameter(g5) = 8
    c: Coincident(g5,g4)
    c: Tangent(g4,g-7)
    c: Tangent(g4,g-8)
    c: Diameter(g6) = 3.2
    c: Diameter(g7) = 8
    c: Coincident(g7,g6)
    c: Tangent(g6,g-9)
    c: Tangent(g6,g-10)
    c: Diameter(g8) = 3.2
    c: Diameter(g9) = 8
    c: Coincident(g9,g8)
    c: Tangent(g8,g-10)
    c: Tangent(g8,g-11)
    c: Diameter(g10) = 3.2
    c: Diameter(g11) = 8
    c: Diameter(g12) = 3.2
    c: Diameter(g13) = 8
    c: Coincident(g12,g13)
    c: Coincident(g10,g11)
    c: Tangent(g12,g-7)
    c: DistanceX(g12,g10) = 0
    c: Tangent(g2,g-6)
    c: Tangent(g0,g-6)
    c: Tangent(g0,g-3)
    c: Tangent(g10,g-3)
    c: Tangent(g10,g-4)
FEATURE [Part::Extrusion] Extrude012  label="extrude guide per coperture laterali"
  Base = -> Sketch016
  Dir = (0,-1,2e-16)
  DirMode = 2
  FaceMakerClass = Part::FaceMakerBullseye
  FaceMakerMode = 3
  LengthFwd = 25.2
  LengthRev = 0
  Solid = true
  Symmetric = true
FEATURE [Sketcher::SketchObject] Sketch017  label="supporto CAM"
  ArcFitTolerance = 1e-06
  AttachmentSupport = -> [XZ_Plane]
  ExternalGeometry = -> [Sketch]
  FullyConstrained = true
  MakeInternals = false
  MapMode = 5
  Placement = pos=(0,0,0) rot=(1,0,0;1.5708rad)
  sketch-geometry (6):
    g0: LineSegment StartX=-2.4 StartY=48 StartZ=0 EndX=-2.4 EndY=41.2 EndZ=0
    g1: LineSegment StartX=-2.4 StartY=48 StartZ=0 EndX=-34 EndY=48 EndZ=0
    g2: LineSegment StartX=-34 StartY=48 StartZ=0 EndX=-34 EndY=46.72 EndZ=0
    g3: LineSegment StartX=-34 StartY=46.72 StartZ=0 EndX=-36 EndY=46.72 EndZ=0
    g4: LineSegment StartX=-36 StartY=46.72 StartZ=0 EndX=-36 EndY=41.2 EndZ=0
    g5: LineSegment StartX=-36 StartY=41.2 StartZ=0 EndX=-2.4 EndY=41.2 EndZ=0
  constraints (15):
    c: Coincident(g1,g0)
    c: Horizontal(g1)
    c: Coincident(g2,g1)
    c: Vertical(g2)
    c: Coincident(g3,g2)
    c: Horizontal(g3)
    c: Coincident(g4,g3)
    c: Coincident(g5,g4)
    c: DistanceX(g1,g0) = 31.6
    c: Coincident(g5,g0)
    c: Vertical(g4)
    c: DistanceY(g2,g1) = 1.28
    c: Coincident(g0,g-3)
    c: Coincident(g0,g-3)
    c: Coincident(g4,g-4)
FEATURE [Part::Extrusion] Extrude013  label="Extrude supporto CAM"
  Base = -> Sketch017
  Dir = (0,-1,2e-16)
  DirMode = 2
  FaceMakerClass = Part::FaceMakerBullseye
  FaceMakerMode = 3
  LengthFwd = 17.8
  LengthRev = 0
  Solid = true
  Symmetric = true
FEATURE [Sketcher::SketchObject] Sketch018  label="Scavo CAM"
  ArcFitTolerance = 1e-06
  AttachmentSupport = -> [YZ_Plane]
  ExternalGeometry = -> [Sketch]
  FullyConstrained = true
  MakeInternals = false
  MapMode = 5
  Placement = pos=(0,0,0) rot=(0.57735,0.57735,0.57735;2.0944rad)
  sketch-geometry (4):
    g0: LineSegment StartX=-7.73 StartY=48 StartZ=0 EndX=7.73 EndY=48 EndZ=0
    g1: LineSegment [constr] StartX=1.07e-14 StartY=48 StartZ=0 EndX=0 EndY=43.5155 EndZ=0
    g2: ArcOfCircle CenterX=9e-15 CenterY=52.42 CenterZ=0 NormalX=0 NormalY=0 NormalZ=1 AngleXU=0 Radius=8.90445 StartAngle=3.66102 EndAngle=5.76376
    g3: Circle [constr] CenterX=9e-15 CenterY=52.42 CenterZ=0 NormalX=0 NormalY=0 NormalZ=1 AngleXU=0 Radius=8.9
  constraints (13):
    c: Horizontal(g0)
    c: DistanceY(g-3,g0) = 0
    c: DistanceX(g0,g0) = 15.46
    c: DistanceX(g0,g-3) = 7.73
    c: DistanceX(g-3) = 0
    c: Coincident(g1,g-3)
    c: PointOnObject(g1,g-2)
    c: Coincident(g2,g0)
    c: Coincident(g2,g0)
    c: PointOnObject(g1,g2)
    c: Diameter(g3) = 17.8
    c: DistanceY(g1,g3) = 4.42
    c: Coincident(g2,g3)
FEATURE [Part::Extrusion] Extrude014  label="Extrude Scavo CAM"
  Base = -> Sketch018
  Dir = (1,0,0)
  DirMode = 2
  FaceMakerClass = Part::FaceMakerBullseye
  FaceMakerMode = 3
  LengthFwd = -34
  LengthRev = 0
  Solid = true
  Symmetric = false
FEATURE [Sketcher::SketchObject] Sketch019  label="scavo rumble"
  ArcFitTolerance = 1e-06
  AttachmentSupport = -> [XZ_Plane]
  ExternalGeometry = -> [Sketch]
  FullyConstrained = true
  MakeInternals = false
  MapMode = 5
  Placement = pos=(0,0,0) rot=(1,0,0;1.5708rad)
  sketch-geometry (6):
    g0: LineSegment StartX=-164.575 StartY=-24.3786 StartZ=0 EndX=-159.439 EndY=-26.0473 EndZ=0
    g1: LineSegment StartX=-159.439 StartY=-26.0473 StartZ=0 EndX=-166.547 EndY=-47.9216 EndZ=0
    g2: LineSegment StartX=-166.547 StartY=-47.9216 StartZ=0 EndX=-171.682 EndY=-46.2529 EndZ=0
    g3: LineSegment StartX=-171.682 StartY=-46.2529 StartZ=0 EndX=-164.575 EndY=-24.3786 EndZ=0
    g4: LineSegment [constr] StartX=-145.51 StartY=22 StartZ=0 EndX=-160.961 EndY=-25.5528 EndZ=0
    g5: LineSegment [constr] StartX=-159.439 StartY=-26.0473 StartZ=0 EndX=-160.961 EndY=-25.5528 EndZ=0
  constraints (17):
    c: Coincident(g1,g0)
    c: Coincident(g2,g1)
    c: Coincident(g3,g2)
    c: Coincident(g3,g0)
    c: Parallel(g3,g-3)
    c: Parallel(g3,g1)
    c: Perpendicular(g3,g0)
    c: Perpendicular(g2,g3)
    c: Distance(g2,g0) = 23
    c: Parallel(g4,g-3)
    c: Distance(g4) = 50
    c: Coincident(g4,g-3)
    c: Parallel(g5,g0)
    c: Distance(g5) = 1.6
    c: Coincident(g5,g0)
    c: Distance(g5,g0) = 3.8
    c: Coincident(g5,g4)
FEATURE [Part::Extrusion] Extrude015  label="scavo rumble001"
  Base = -> Sketch019
  Dir = (0,-1,2e-16)
  DirMode = 2
  FaceMakerClass = Part::FaceMakerBullseye
  FaceMakerMode = 3
  LengthFwd = 21
  LengthRev = 0
  Solid = true
  Symmetric = true
FEATURE [Sketcher::SketchObject] Sketch020  label="fermo rumble"
  ArcFitTolerance = 1e-06
  AttachmentSupport = -> [XZ_Plane]
  ExternalGeometry = -> [Sketch019,Sketch]
  FullyConstrained = true
  MakeInternals = false
  MapMode = 5
  Placement = pos=(0,0,0) rot=(1,0,0;1.5708rad)
  sketch-geometry (16):
    g0: LineSegment [constr] StartX=-166.709 StartY=-43.2425 StartZ=0 EndX=-168.068 EndY=-47.4271 EndZ=0
    g1: LineSegment [constr] StartX=-168.068 StartY=-47.4271 StartZ=0 EndX=-166.547 EndY=-47.9216 EndZ=0
    g2: LineSegment StartX=-168.121 StartY=-40.4703 StartZ=0 EndX=-166.029 EndY=-41.1502 EndZ=0
    g3: LineSegment StartX=-166.029 StartY=-41.1502 StartZ=0 EndX=-166.709 EndY=-43.2425 EndZ=0
    g4: LineSegment StartX=-166.709 StartY=-43.2425 StartZ=0 EndX=-168.801 EndY=-42.5626 EndZ=0
    g5: LineSegment StartX=-168.801 StartY=-42.5626 StartZ=0 EndX=-168.121 EndY=-40.4703 EndZ=0
    g6: LineSegment StartX=-167.627 StartY=-38.9486 StartZ=0 EndX=-164.203 EndY=-40.0611 EndZ=0
    g7: LineSegment StartX=-164.203 StartY=-40.0611 StartZ=0 EndX=-165.81 EndY=-45.0066 EndZ=0
    g8: LineSegment StartX=-165.81 StartY=-45.0066 StartZ=0 EndX=-169.234 EndY=-43.8941 EndZ=0
    g9: LineSegment StartX=-170.261 StartY=-41.878 StartZ=0 EndX=-169.643 EndY=-39.9759 EndZ=0
    g10: LineSegment [constr] StartX=-169.643 StartY=-39.9759 StartZ=0 EndX=-169.148 EndY=-38.4542 EndZ=0
    g11: LineSegment [constr] StartX=-169.148 StartY=-38.4542 StartZ=0 EndX=-167.627 EndY=-38.9486 EndZ=0
    g12: ArcOfCircle CenterX=-168.739 CenterY=-42.3724 CenterZ=0 NormalX=0 NormalY=0 NormalZ=1 AngleXU=0 Radius=1.6 StartAngle=2.82743 EndAngle=4.39823
    g13: GeomPoint [constr] X=-170.755 Y=-43.3997 Z=0
    g14: ArcOfCircle CenterX=-168.121 CenterY=-40.4703 CenterZ=0 NormalX=0 NormalY=0 NormalZ=1 AngleXU=0 Radius=1.6 StartAngle=1.25664 EndAngle=2.82743
    g15: GeomPoint [constr] X=-169.148 Y=-38.4542 Z=0
  constraints (42):
    c: Parallel(g0,g-4)
    c: Distance(g0) = 4.4
    c: Coincident(g1,g0)
    c: Perpendicular(g0,g1)
    c: Distance(g1) = 1.6
    c: Coincident(g1,g-5)
    c: Coincident(g3,g2)
    c: Coincident(g4,g3)
    c: Coincident(g5,g4)
    c: Coincident(g5,g2)
    c: Parallel(g3,g-4)
    c: Parallel(g3,g5)
    c: Perpendicular(g2,g3)
    c: Parallel(g4,g2)
    c: Distance(g2) = 2.2
    c: Distance(g3) = 2.2
    c: Coincident(g7,g6)
    c: Coincident(g8,g7)
    c: Parallel(g7,g-4)
    c: Parallel(g7,g9)
    c: Perpendicular(g6,g7)
    c: Parallel(g6,g8)
    c: Distance(g6,g15) = 5.2
    c: Distance(g7) = 5.2
    c: Coincident(g11,g10)
    c: Parallel(g10,g9)
    c: Parallel(g11,g6)
    c: Distance(g10) = 1.6
    c: Distance(g11) = 1.6
    c: Coincident(g10,g15)
    c: Distance(g11,g2) = 1.6
    c: Distance(g2,g10) = 1.6
    c: PointOnObject(g13,g8)
    c: PointOnObject(g13,g9)
    c: Tangent(g8,g12) = 1.5708
    c: Tangent(g9,g12) = 1.5708
    c: PointOnObject(g15,g9)
    c: Tangent(g6,g14) = 1.5708
    c: Tangent(g9,g14) = 1.5708
    c: Equal(g12,g14)
    c: Coincident(g6,g11)
    c: Coincident(g3,g0)
FEATURE [Part::Extrusion] Extrude016  label="Extrude fermo rumble"
  Base = -> Sketch020
  Dir = (0,-1,2e-16)
  DirMode = 2
  FaceMakerClass = Part::FaceMakerBullseye
  FaceMakerMode = 3
  LengthFwd = 25.2
  LengthRev = 0
  Solid = true
  Symmetric = true
FEATURE [Sketcher::SketchObject] Sketch021  label="perno fermo rumble001"
  ArcFitTolerance = 1e-06
  AttachmentSupport = -> [XZ_Plane001]
  FullyConstrained = true
  MakeInternals = false
  MapMode = 5
  Placement = pos=(0,0,0) rot=(1,0,0;1.5708rad)
  sketch-geometry (16):
    g0: LineSegment StartX=0 StartY=0.45 StartZ=0 EndX=0 EndY=1.55 EndZ=0
    g1: LineSegment StartX=0.45 StartY=2 StartZ=0 EndX=1.55 EndY=2 EndZ=0
    g2: LineSegment StartX=2 StartY=1.55 StartZ=0 EndX=2 EndY=0.45 EndZ=0
    g3: LineSegment StartX=1.55 StartY=0 StartZ=0 EndX=0.45 EndY=0 EndZ=0
    g4: ArcOfCircle [constr] CenterX=0.45 CenterY=1.55 CenterZ=0 NormalX=0 NormalY=0 NormalZ=1 AngleXU=0 Radius=0.45 StartAngle=1.5708 EndAngle=3.14159
    g5: GeomPoint [constr] X=0 Y=2 Z=0
    g6: LineSegment StartX=0.45 StartY=2 StartZ=0 EndX=0 EndY=1.55 EndZ=0
    g7: ArcOfCircle [constr] CenterX=1.55 CenterY=1.55 CenterZ=0 NormalX=0 NormalY=0 NormalZ=1 AngleXU=0 Radius=0.45 StartAngle=0 EndAngle=1.5708
    g8: GeomPoint [constr] X=2 Y=2 Z=0
    g9: LineSegment StartX=2 StartY=1.55 StartZ=0 EndX=1.55 EndY=2 EndZ=0
    g10: ArcOfCircle [constr] CenterX=1.55 CenterY=0.45 CenterZ=0 NormalX=0 NormalY=0 NormalZ=1 AngleXU=0 Radius=0.45 StartAngle=4.71239 EndAngle=6.28319
    g11: GeomPoint [constr] X=2 Y=0 Z=0
    g12: LineSegment StartX=1.55 StartY=0 StartZ=0 EndX=2 EndY=0.45 EndZ=0
    g13: ArcOfCircle [constr] CenterX=0.45 CenterY=0.45 CenterZ=0 NormalX=0 NormalY=0 NormalZ=1 AngleXU=0 Radius=0.45 StartAngle=3.14159 EndAngle=4.71239
    g14: GeomPoint [constr] X=0 Y=0 Z=0
    g15: LineSegment StartX=0 StartY=0.45 StartZ=0 EndX=0.45 EndY=0 EndZ=0
  constraints (35):
    c: Coincident(g14,g-1)
    c: PointOnObject(g5,g-2)
    c: Horizontal(g1)
    c: Vertical(g2)
    c: Horizontal(g3)
    c: DistanceX(g5,g8) = 2
    c: DistanceY(g11,g8) = 2
    c: PointOnObject(g5,g0)
    c: PointOnObject(g5,g1)
    c: Tangent(g0,g4) = 1.5708
    c: Tangent(g1,g4) = 1.5708
    c: Coincident(g6,g0)
    c: Coincident(g6,g1)
    c: PointOnObject(g8,g2)
    c: PointOnObject(g8,g1)
    c: Tangent(g2,g7) = 1.5708
    c: Tangent(g1,g7) = 1.5708
    c: Coincident(g9,g2)
    c: Coincident(g9,g1)
    c: PointOnObject(g11,g2)
    c: PointOnObject(g11,g3)
    c: Tangent(g2,g10) = 1.5708
    c: Tangent(g3,g10) = 1.5708
    c: Coincident(g12,g2)
    c: Coincident(g12,g3)
    c: PointOnObject(g14,g0)
    c: PointOnObject(g14,g3)
    c: Tangent(g0,g13) = 1.5708
    c: Tangent(g3,g13) = 1.5708
    c: Coincident(g15,g0)
    c: Coincident(g15,g3)
    c: Equal(g6,g9)
    c: Equal(g9,g12)
    c: Equal(g12,g15)
    c: DistanceX(g14,g3) = 0.45
FEATURE [Sketcher::SketchObject] Sketch022  label="fori per M3x5(OD)x6(L)"
  ArcFitTolerance = 1e-06
  AttachmentSupport = -> [XZ_Plane]
  ExternalGeometry = -> [Sketch016]
  FullyConstrained = true
  MakeInternals = false
  MapMode = 5
  Placement = pos=(0,0,0) rot=(1,0,0;1.5708rad)
  sketch-geometry (7):
    g0: Circle CenterX=-5.6 CenterY=34.8 CenterZ=0 NormalX=0 NormalY=0 NormalZ=1 AngleXU=0 Radius=2.5
    g1: Circle CenterX=-5.6 CenterY=7.6 CenterZ=0 NormalX=0 NormalY=0 NormalZ=1 AngleXU=0 Radius=2.5
    g2: Circle CenterX=-78.51 CenterY=34.8 CenterZ=0 NormalX=0 NormalY=0 NormalZ=1 AngleXU=0 Radius=2.5
    g3: Circle CenterX=-78.51 CenterY=7.6 CenterZ=0 NormalX=0 NormalY=0 NormalZ=1 AngleXU=0 Radius=2.5
    g4: Circle CenterX=-184.08 CenterY=34.8 CenterZ=0 NormalX=0 NormalY=0 NormalZ=1 AngleXU=0 Radius=2.5
    g5: Circle CenterX=-179.305 CenterY=-76.8316 CenterZ=0 NormalX=0 NormalY=0 NormalZ=1 AngleXU=0 Radius=2.5
    g6: Circle CenterX=-213.443 CenterY=-76.8316 CenterZ=0 NormalX=0 NormalY=0 NormalZ=1 AngleXU=0 Radius=2.5
  constraints (14):
    c: Diameter(g0) = 5
    c: Diameter(g1) = 5
    c: Diameter(g2) = 5
    c: Diameter(g3) = 5
    c: Diameter(g4) = 5
    c: Diameter(g5) = 5
    c: Diameter(g6) = 5
    c: Coincident(g0,g-8)
    c: Coincident(g1,g-9)
    c: Coincident(g2,g-6)
    c: Coincident(g3,g-7)
    c: Coincident(g4,g-5)
    c: Coincident(g5,g-4)
    c: Coincident(g6,g-3)
FEATURE [Part::Extrusion] Extrude018  label="Extrude fori M3x5x6 - dx"
  Base = -> Sketch022
  Dir = (0,-1,2e-16)
  DirMode = 2
  FaceMakerClass = Part::FaceMakerBullseye
  FaceMakerMode = 3
  LengthFwd = 6.2
  LengthRev = 0
  Placement = pos=(0,-9.5,0) rot=(0,0,1;0rad)
  Solid = true
  Symmetric = true
FEATURE [Part::Extrusion] Extrude019  label="Extrude fori M3x5x6 - sx"
  Base = -> Sketch022
  Dir = (0,-1,2e-16)
  DirMode = 2
  FaceMakerClass = Part::FaceMakerBullseye
  FaceMakerMode = 3
  LengthFwd = 6.2
  LengthRev = 0
  Placement = pos=(0,9.5,0) rot=(0,0,1;0rad)
  Solid = true
  Symmetric = true
FEATURE [Sketcher::SketchObject] Sketch023  label="foro anteriore M3x5x6"
  ArcFitTolerance = 1e-06
  AttachmentSupport = -> [YZ_Plane]
  FullyConstrained = true
  MakeInternals = false
  MapMode = 5
  Placement = pos=(0,0,0) rot=(0.57735,0.57735,0.57735;2.0944rad)
  sketch-geometry (2):
    g0: LineSegment [constr] StartX=0 StartY=0 StartZ=0 EndX=0 EndY=38.6 EndZ=0
    g1: Circle CenterX=0 CenterY=38.6 CenterZ=0 NormalX=0 NormalY=0 NormalZ=1 AngleXU=0 Radius=2.5
  constraints (5):
    c: Coincident(g0,g-1)
    c: PointOnObject(g0,g-2)
    c: DistanceY(g0,g0) = 38.6
    c: Diameter(g1) = 5
    c: Coincident(g1,g0)
FEATURE [Part::Extrusion] Extrude020  label="Extrude foro anteriore M3x5x6"
  Base = -> Sketch023
  Dir = (1,0,0)
  DirMode = 2
  FaceMakerClass = Part::FaceMakerBullseye
  FaceMakerMode = 3
  LengthFwd = -6.2
  LengthRev = 0
  Solid = true
  Symmetric = false
FEATURE [Sketcher::SketchObject] Sketch024  label="fori per viti frontale"
  ArcFitTolerance = 1e-06
  AttachmentSupport = -> [YZ_Plane]
  FullyConstrained = true
  MakeInternals = false
  MapMode = 5
  Placement = pos=(0,0,0) rot=(0.57735,0.57735,0.57735;2.0944rad)
  sketch-geometry (9):
    g0: LineSegment [constr] StartX=-10.3 StartY=30.721 StartZ=0 EndX=10.3 EndY=30.721 EndZ=0
    g1: LineSegment [constr] StartX=10.3 StartY=30.721 StartZ=0 EndX=10.3 EndY=10.121 EndZ=0
    g2: LineSegment [constr] StartX=10.3 StartY=10.121 StartZ=0 EndX=-10.3 EndY=10.121 EndZ=0
    g3: LineSegment [constr] StartX=-10.3 StartY=10.121 StartZ=0 EndX=-10.3 EndY=30.721 EndZ=0
    g4: LineSegment [constr] StartX=0 StartY=0 StartZ=0 EndX=0 EndY=10.121 EndZ=0
    g5: Circle CenterX=-10.3 CenterY=30.721 CenterZ=0 NormalX=0 NormalY=0 NormalZ=1 AngleXU=0 Radius=2
    g6: Circle CenterX=10.3 CenterY=30.721 CenterZ=0 NormalX=0 NormalY=0 NormalZ=1 AngleXU=0 Radius=2
    g7: Circle CenterX=-10.3 CenterY=10.121 CenterZ=0 NormalX=0 NormalY=0 NormalZ=1 AngleXU=0 Radius=2
    g8: Circle CenterX=10.3 CenterY=10.121 CenterZ=0 NormalX=0 NormalY=0 NormalZ=1 AngleXU=0 Radius=2
  constraints (22):
    c: Horizontal(g0)
    c: Coincident(g1,g0)
    c: Vertical(g1)
    c: Coincident(g2,g1)
    c: Horizontal(g2)
    c: Coincident(g3,g2)
    c: Coincident(g3,g0)
    c: Vertical(g3)
    c: DistanceX(g0,g0) = 20.6
    c: DistanceY(g3,g3) = 20.6
    c: Coincident(g4,g-1)
    c: PointOnObject(g4,g-2)
    c: DistanceY(g4,g4) = 10.121
    c: Symmetric(g2,g2,g4)
    c: Diameter(g5) = 4
    c: Diameter(g6) = 4
    c: Diameter(g7) = 4
    c: Diameter(g8) = 4
    c: Coincident(g5,g0)
    c: Coincident(g6,g0)
    c: Coincident(g7,g2)
    c: Coincident(g8,g1)
FEATURE [Part::Extrusion] Extrude021  label="Extrude fori per viti frontale"
  Base = -> Sketch024
  Dir = (1,0,0)
  DirMode = 2
  FaceMakerClass = Part::FaceMakerBullseye
  FaceMakerMode = 3
  LengthFwd = -2.4
  LengthRev = 0
  Solid = true
  Symmetric = false
FEATURE [Sketcher::SketchObject] Sketch025  label="foro per filo CAM"
  ArcFitTolerance = 1e-06
  AttachmentSupport = -> [XZ_Plane]
  ExternalGeometry = -> [Sketch]
  FullyConstrained = true
  MakeInternals = false
  MapMode = 5
  Placement = pos=(0,0,0) rot=(1,0,0;1.5708rad)
  sketch-geometry (4):
    g0: LineSegment StartX=-44.6 StartY=41.2 StartZ=0 EndX=-44.6 EndY=36.4 EndZ=0
    g1: LineSegment StartX=-44.6 StartY=36.4 StartZ=0 EndX=-54.6 EndY=36.4 EndZ=0
    g2: LineSegment StartX=-54.6 StartY=36.4 StartZ=0 EndX=-50.4 EndY=41.2 EndZ=0
    g3: LineSegment StartX=-50.4 StartY=41.2 StartZ=0 EndX=-44.6 EndY=41.2 EndZ=0
  constraints (11):
    c: Vertical(g0)
    c: Coincident(g1,g0)
    c: Horizontal(g1)
    c: Coincident(g2,g1)
    c: Coincident(g3,g2)
    c: Coincident(g3,g0)
    c: Horizontal(g3)
    c: Coincident(g0,g-3)
    c: DistanceY(g0,g-4) = 0
    c: DistanceX(g3,g3) = 5.8
    c: DistanceX(g1,g1) = 10
FEATURE [Part::Extrusion] Extrude022  label="Extrude foro per filo CAM dx"
  Base = -> Sketch025
  Dir = (0,-1,2e-16)
  DirMode = 2
  FaceMakerClass = Part::FaceMakerBullseye
  FaceMakerMode = 3
  LengthFwd = 4.9
  LengthRev = 0
  Placement = pos=(0,6.95,0) rot=(0,0,1;0rad)
  Solid = true
  Symmetric = true
FEATURE [Part::Extrusion] Extrude023  label="Extrude foro per filo CAM sx"
  Base = -> Sketch025
  Dir = (0,-1,2e-16)
  DirMode = 2
  FaceMakerClass = Part::FaceMakerBullseye
  FaceMakerMode = 3
  LengthFwd = 4.9
  LengthRev = 0
  Placement = pos=(0,-6.95,0) rot=(0,0,1;0rad)
  Solid = true
  Symmetric = true
FEATURE [Sketcher::SketchObject] Sketch026  label="foro sotto anteriore M3x5x6"
  ArcFitTolerance = 1e-06
  AttachmentSupport = -> [XY_Plane]
  FullyConstrained = true
  MakeInternals = false
  MapMode = 5
  sketch-geometry (2):
    g0: LineSegment [constr] StartX=0 StartY=0 StartZ=0 EndX=-16.5 EndY=0 EndZ=0
    g1: Circle CenterX=-16.5 CenterY=0 CenterZ=0 NormalX=0 NormalY=0 NormalZ=1 AngleXU=0 Radius=2.5
  constraints (5):
    c: Distance(g0) = 16.5
    c: Coincident(g0,g-1)
    c: PointOnObject(g0,g-1)
    c: Diameter(g1) = 5
    c: Coincident(g0,g1)
FEATURE [Sketcher::SketchObject] Sketch027  label="foro sotto posteriore M3x5x6"
  ArcFitTolerance = 1e-06
  AttachmentSupport = -> [XY_Plane]
  ExternalGeometry = -> [Sketch]
  FullyConstrained = true
  MakeInternals = false
  MapMode = 5
  sketch-geometry (2):
    g0: LineSegment [constr] StartX=-82.8 StartY=2e-16 StartZ=0 EndX=-71.3 EndY=2e-16 EndZ=0
    g1: Circle CenterX=-71.3 CenterY=2e-16 CenterZ=0 NormalX=0 NormalY=0 NormalZ=1 AngleXU=0 Radius=2.5
  constraints (5):
    c: Distance(g0) = 11.5
    c: Coincident(g0,g-3)
    c: PointOnObject(g0,g-3)
    c: Diameter(g1) = 5
    c: Coincident(g1,g0)
FEATURE [Sketcher::SketchObject] Sketch029  label="fori sotto impugnatura"
  ArcFitTolerance = 1e-06
  AttachmentSupport = -> [XY_Plane]
  ExternalGeometry = -> [Sketch]
  FullyConstrained = true
  MakeInternals = false
  MapMode = 5
  sketch-geometry (15):
    g0: LineSegment [constr] StartX=-175.232 StartY=-1.83e-14 StartZ=0 EndX=-191.232 EndY=0 EndZ=0
    g1: Circle CenterX=-191.232 CenterY=0 CenterZ=0 NormalX=0 NormalY=0 NormalZ=1 AngleXU=0 Radius=3.95
    g2: LineSegment [constr] StartX=-175.232 StartY=-1.83e-14 StartZ=0 EndX=-204.275 EndY=0 EndZ=0
    g3: LineSegment StartX=-204.275 StartY=3.525 StartZ=0 EndX=-204.275 EndY=-3.525 EndZ=0
    g4: LineSegment StartX=-205.4 StartY=-4.65 StartZ=0 EndX=-206.65 EndY=-4.65 EndZ=0
    g5: LineSegment StartX=-207.775 StartY=-3.525 StartZ=0 EndX=-207.775 EndY=3.525 EndZ=0
    g6: LineSegment StartX=-206.65 StartY=4.65 StartZ=0 EndX=-205.4 EndY=4.65 EndZ=0
    g7: ArcOfCircle CenterX=-206.65 CenterY=3.525 CenterZ=0 NormalX=0 NormalY=0 NormalZ=1 AngleXU=0 Radius=1.125 StartAngle=1.5708 EndAngle=3.14159
    g8: GeomPoint [constr] X=-207.775 Y=4.65 Z=0
    g9: ArcOfCircle CenterX=-205.4 CenterY=3.525 CenterZ=0 NormalX=0 NormalY=0 NormalZ=1 AngleXU=0 Radius=1.125 StartAngle=0 EndAngle=1.5708
    g10: GeomPoint [constr] X=-204.275 Y=4.65 Z=0
    g11: ArcOfCircle CenterX=-205.4 CenterY=-3.525 CenterZ=0 NormalX=0 NormalY=0 NormalZ=1 AngleXU=0 Radius=1.125 StartAngle=4.71239 EndAngle=6.28319
    g12: GeomPoint [constr] X=-204.275 Y=-4.65 Z=0
    g13: ArcOfCircle CenterX=-206.65 CenterY=-3.525 CenterZ=0 NormalX=0 NormalY=0 NormalZ=1 AngleXU=0 Radius=1.125 StartAngle=3.14159 EndAngle=4.71239
    g14: GeomPoint [constr] X=-207.775 Y=-4.65 Z=0
  constraints (35):
    c: Distance(g0) = 16
    c: Coincident(g0,g-3)
    c: PointOnObject(g0,g-1)
    c: Diameter(g1) = 7.9
    c: Coincident(g1,g0)
    c: Coincident(g2,g0)
    c: PointOnObject(g2,g-1)
    c: Vertical(g3)
    c: Horizontal(g4)
    c: Vertical(g5)
    c: Horizontal(g6)
    c: DistanceY(g12,g10) = 9.3
    c: DistanceX(g8,g10) = 3.5
    c: Symmetric(g10,g12,g2)
    c: PointOnObject(g8,g5)
    c: PointOnObject(g8,g6)
    c: Tangent(g5,g7) = 1.5708
    c: Tangent(g6,g7) = 1.5708
    c: PointOnObject(g10,g3)
    c: PointOnObject(g10,g6)
    c: Tangent(g3,g9) = 1.5708
    c: Tangent(g6,g9) = 1.5708
    c: PointOnObject(g12,g3)
    c: PointOnObject(g12,g4)
    c: Tangent(g3,g11) = 1.5708
    c: Tangent(g4,g11) = 1.5708
    c: PointOnObject(g14,g4)
    c: PointOnObject(g14,g5)
    c: Tangent(g4,g13) = 1.5708
    c: Tangent(g5,g13) = 1.5708
    c: Equal(g7,g9)
    c: Equal(g9,g11)
    c: Equal(g11,g13)
    c: DistanceX(g6,g6) = 1.25
    c: DistanceX(g-5,g5) = 6.8
FEATURE [Sketcher::SketchObject] Sketch030  label="fori superiori per solenoide e oled"
  ArcFitTolerance = 1e-06
  AttachmentSupport = -> [XY_Plane]
  ExternalGeometry = -> [Sketch]
  FullyConstrained = true
  MakeInternals = false
  MapMode = 5
  sketch-geometry (33):
    g0: LineSegment [constr] StartX=-181.6 StartY=1.12e-14 StartZ=0 EndX=-169.91 EndY=0 EndZ=0
    g1: LineSegment [constr] StartX=-169.91 StartY=0 StartZ=0 EndX=-169.91 EndY=-2.6 EndZ=0
    g2: LineSegment [constr] StartX=-169.91 StartY=0 StartZ=0 EndX=-169.91 EndY=2.6 EndZ=0
    g3: LineSegment StartX=-169.91 StartY=4.975 StartZ=0 EndX=-169.91 EndY=8.225 EndZ=0
    g4: LineSegment StartX=-167.535 StartY=10.6 StartZ=0 EndX=-167.285 EndY=10.6 EndZ=0
    g5: LineSegment StartX=-164.91 StartY=8.225 StartZ=0 EndX=-164.91 EndY=4.975 EndZ=0
    g6: LineSegment StartX=-167.285 StartY=2.6 StartZ=0 EndX=-167.535 EndY=2.6 EndZ=0
    g7: LineSegment StartX=-169.91 StartY=-4.975 StartZ=0 EndX=-169.91 EndY=-8.225 EndZ=0
    g8: LineSegment StartX=-167.535 StartY=-10.6 StartZ=0 EndX=-167.285 EndY=-10.6 EndZ=0
    g9: LineSegment StartX=-164.91 StartY=-8.225 StartZ=0 EndX=-164.91 EndY=-4.975 EndZ=0
    g10: LineSegment StartX=-167.285 StartY=-2.6 StartZ=0 EndX=-167.535 EndY=-2.6 EndZ=0
    g11: ArcOfCircle CenterX=-167.535 CenterY=8.225 CenterZ=0 NormalX=0 NormalY=0 NormalZ=1 AngleXU=0 Radius=2.375 StartAngle=1.5708 EndAngle=3.14159
    g12: GeomPoint [constr] X=-169.91 Y=10.6 Z=0
    g13: ArcOfCircle CenterX=-167.285 CenterY=8.225 CenterZ=0 NormalX=0 NormalY=0 NormalZ=1 AngleXU=0 Radius=2.375 StartAngle=0 EndAngle=1.5708
    g14: GeomPoint [constr] X=-164.91 Y=10.6 Z=0
    g15: ArcOfCircle CenterX=-167.285 CenterY=4.975 CenterZ=0 NormalX=0 NormalY=0 NormalZ=1 AngleXU=0 Radius=2.375 StartAngle=4.71239 EndAngle=6.28319
    g16: GeomPoint [constr] X=-164.91 Y=2.6 Z=0
    g17: ArcOfCircle CenterX=-167.535 CenterY=4.975 CenterZ=0 NormalX=0 NormalY=0 NormalZ=1 AngleXU=0 Radius=2.375 StartAngle=3.14159 EndAngle=4.71239
    g18: GeomPoint [constr] X=-169.91 Y=2.6 Z=0
    g19: ArcOfCircle CenterX=-167.535 CenterY=-4.975 CenterZ=0 NormalX=0 NormalY=0 NormalZ=1 AngleXU=0 Radius=2.375 StartAngle=1.5708 EndAngle=3.14159
    g20: GeomPoint [constr] X=-169.91 Y=-2.6 Z=0
    g21: ArcOfCircle CenterX=-167.285 CenterY=-4.975 CenterZ=0 NormalX=0 NormalY=0 NormalZ=1 AngleXU=0 Radius=2.375 StartAngle=0 EndAngle=1.5708
    g22: GeomPoint [constr] X=-164.91 Y=-2.6 Z=0
    g23: ArcOfCircle CenterX=-167.285 CenterY=-8.225 CenterZ=0 NormalX=0 NormalY=0 NormalZ=1 AngleXU=0 Radius=2.375 StartAngle=4.71239 EndAngle=6.28319
    g24: GeomPoint [constr] X=-164.91 Y=-10.6 Z=0
    g25: ArcOfCircle CenterX=-167.535 CenterY=-8.225 CenterZ=0 NormalX=0 NormalY=0 NormalZ=1 AngleXU=0 Radius=2.375 StartAngle=3.14159 EndAngle=4.71239
    g26: GeomPoint [constr] X=-169.91 Y=-10.6 Z=0
    g27: LineSegment [constr] StartX=-181.6 StartY=1.12e-14 StartZ=0 EndX=-152.209 EndY=0 EndZ=0
    g28: LineSegment [constr] StartX=-181.6 StartY=1.12e-14 StartZ=0 EndX=-130.41 EndY=0 EndZ=0
    g29: LineSegment [constr] StartX=-152.209 StartY=0 StartZ=0 EndX=-152.209 EndY=6.95 EndZ=0
    g30: LineSegment [constr] StartX=-130.41 StartY=0 StartZ=0 EndX=-130.41 EndY=-6.95 EndZ=0
    g31: Circle CenterX=-152.209 CenterY=6.95 CenterZ=0 NormalX=0 NormalY=0 NormalZ=1 AngleXU=0 Radius=2.1
    g32: Circle CenterX=-130.41 CenterY=-6.95 CenterZ=0 NormalX=0 NormalY=0 NormalZ=1 AngleXU=0 Radius=2.1
  constraints (79):
    c: Distance(g0) = 11.69
    c: PointOnObject(g0,g-1)
    c: Coincident(g-4,g0)
    c: Distance(g1) = 2.6
    c: Coincident(g1,g0)
    c: Vertical(g1)
    c: Distance(g2) = 2.6
    c: Coincident(g2,g0)
    c: Vertical(g2)
    c: Distance(g18,g12) = 8
    c: Coincident(g18,g2)
    c: Vertical(g3)
    c: Distance(g14,g12) = 5
    c: Horizontal(g4)
    c: Distance(g16,g14) = 8
    c: Vertical(g5)
    c: Distance(g26,g20) = 8
    c: Coincident(g20,g1)
    c: Vertical(g7)
    c: Distance(g26,g24) = 5
    c: Horizontal(g8)
    c: Distance(g24,g22) = 8
    c: Vertical(g9)
    c: PointOnObject(g12,g3)
    c: PointOnObject(g12,g4)
    c: Tangent(g3,g11) = 1.5708
    c: Tangent(g4,g11) = 1.5708
    c: PointOnObject(g14,g5)
    c: PointOnObject(g14,g4)
    c: Tangent(g5,g13) = 1.5708
    c: Tangent(g4,g13) = 1.5708
    c: PointOnObject(g16,g5)
    c: PointOnObject(g16,g6)
    c: Tangent(g5,g15) = 1.5708
    c: Tangent(g6,g15) = 1.5708
    c: PointOnObject(g18,g3)
    c: PointOnObject(g18,g6)
    c: Tangent(g3,g17) = 1.5708
    c: Tangent(g6,g17) = 1.5708
    c: Equal(g11,g13)
    c: Equal(g13,g15)
    c: Equal(g15,g17)
    c: DistanceX(g4,g4) = 0.25
    c: PointOnObject(g20,g7)
    c: PointOnObject(g20,g10)
    c: Tangent(g7,g19) = -1.5708
    c: Tangent(g10,g19) = -1.5708
    c: PointOnObject(g22,g9)
    c: PointOnObject(g22,g10)
    c: Tangent(g9,g21) = -1.5708
    c: Tangent(g10,g21) = -1.5708
    c: PointOnObject(g24,g9)
    c: PointOnObject(g24,g8)
    c: Tangent(g9,g23) = -1.5708
    c: Tangent(g8,g23) = -1.5708
    c: PointOnObject(g26,g8)
    c: PointOnObject(g26,g7)
    c: Tangent(g8,g25) = -1.5708
    c: Tangent(g7,g25) = -1.5708
    c: Equal(g19,g21)
    c: Equal(g21,g23)
    c: Equal(g23,g25)
    c: DistanceX(g10,g10) = 0.25
    c: Distance(g27) = 29.391
    c: Coincident(g27,g0)
    c: PointOnObject(g27,g-1)
    c: Distance(g28) = 51.19
    c: Coincident(g28,g0)
    c: PointOnObject(g28,g-1)
    c: Distance(g29) = 6.95
    c: Coincident(g29,g27)
    c: Vertical(g29)
    c: Distance(g30) = 6.95
    c: Coincident(g30,g28)
    c: Vertical(g30)
    c: Diameter(g31) = 4.2
    c: Diameter(g32) = 4.2
    c: Coincident(g32,g30)
    c: Coincident(g31,g29)
FEATURE [Sketcher::SketchObject] Sketch031  label="fori inferiori switch pompa"
  ArcFitTolerance = 1e-06
  AttachmentSupport = -> [XY_Plane]
  ExternalGeometry = -> [Sketch]
  FullyConstrained = true
  MakeInternals = false
  MapMode = 5
  sketch-geometry (4):
    g0: LineSegment [constr] StartX=-57.2 StartY=1.9e-15 StartZ=0 EndX=-62.45 EndY=1.9e-15 EndZ=0
    g1: LineSegment [constr] StartX=-62.45 StartY=3.25 StartZ=0 EndX=-62.45 EndY=-3.25 EndZ=0
    g2: Circle CenterX=-62.45 CenterY=3.25 CenterZ=0 NormalX=0 NormalY=0 NormalZ=1 AngleXU=0 Radius=1.6
    g3: Circle CenterX=-62.45 CenterY=-3.25 CenterZ=0 NormalX=0 NormalY=0 NormalZ=1 AngleXU=0 Radius=1.6
  constraints (10):
    c: Distance(g0) = 5.25
    c: Coincident(g0,g-3)
    c: PointOnObject(g0,g-3)
    c: Vertical(g1)
    c: DistanceY(g1,g1) = 6.5
    c: Symmetric(g1,g1,g0)
    c: Diameter(g2) = 3.2
    c: Diameter(g3) = 3.2
    c: Coincident(g2,g1)
    c: Coincident(g3,g1)
FEATURE [Sketcher::SketchObject] Sketch032  label="spazio per PILA 18650"
  ArcFitTolerance = 1e-06
  AttachmentSupport = -> [XY_Plane]
  ExternalGeometry = -> [Sketch]
  FullyConstrained = true
  MakeInternals = false
  MapMode = 5
  sketch-geometry (2):
    g0: LineSegment [constr] StartX=-178.142 StartY=-1.74e-14 StartZ=0 EndX=-190.142 EndY=-1.83e-14 EndZ=0
    g1: Circle CenterX=-190.142 CenterY=-1.83e-14 CenterZ=0 NormalX=0 NormalY=0 NormalZ=1 AngleXU=0 Radius=9.25
  constraints (5):
    c: Distance(g0) = 12
    c: Coincident(g0,g-3)
    c: PointOnObject(g0,g-4)
    c: Diameter(g1) = 18.5
    c: Coincident(g1,g0)
FEATURE [Part::Extrusion] Extrude030  label="Extrude spazio per PILA 18650"
  Base = -> Sketch032
  Dir = (0,0,1)
  DirLink = -> Sketch [Edge45]
  DirMode = 2
  FaceMakerClass = Part::FaceMakerBullseye
  FaceMakerMode = 3
  LengthFwd = 68
  LengthRev = 0
  Placement = pos=(6,0,-72.7) rot=(0,0,1;0rad)
  Solid = true
  Symmetric = false
FEATURE [Sketcher::SketchObject] Sketch033  label="fermo per scheda micro"
  ArcFitTolerance = 1e-06
  AttachmentSupport = -> [XZ_Plane]
  ExternalGeometry = -> [Sketch]
  FullyConstrained = true
  MakeInternals = false
  MapMode = 5
  Placement = pos=(0,0,0) rot=(1,0,0;1.5708rad)
  sketch-geometry (12):
    g0: LineSegment StartX=-11.6 StartY=6 StartZ=0 EndX=-4 EndY=6 EndZ=0
    g1: LineSegment StartX=-4 StartY=6 StartZ=0 EndX=-4 EndY=36.4 EndZ=0
    g2: LineSegment StartX=-4 StartY=36.4 StartZ=0 EndX=-11.6 EndY=36.4 EndZ=0
    g3: LineSegment StartX=-11.6 StartY=36.4 StartZ=0 EndX=-11.6 EndY=6 EndZ=0
    g4: LineSegment StartX=-80.11 StartY=11.6 StartZ=0 EndX=-70.51 EndY=11.6 EndZ=0
    g5: LineSegment StartX=-70.51 StartY=11.6 StartZ=0 EndX=-70.51 EndY=6 EndZ=0
    g6: LineSegment StartX=-70.51 StartY=6 StartZ=0 EndX=-80.11 EndY=6 EndZ=0
    g7: LineSegment StartX=-80.11 StartY=6 StartZ=0 EndX=-80.11 EndY=11.6 EndZ=0
    g8: LineSegment StartX=-78.51 StartY=36.4 StartZ=0 EndX=-70.51 EndY=36.4 EndZ=0
    g9: LineSegment StartX=-70.51 StartY=36.4 StartZ=0 EndX=-70.51 EndY=30.8 EndZ=0
    g10: LineSegment StartX=-70.51 StartY=30.8 StartZ=0 EndX=-78.51 EndY=30.8 EndZ=0
    g11: LineSegment StartX=-78.51 StartY=30.8 StartZ=0 EndX=-78.51 EndY=36.4 EndZ=0
  constraints (33):
    c: Horizontal(g0)
    c: Coincident(g1,g0)
    c: Coincident(g2,g1)
    c: Horizontal(g2)
    c: Coincident(g3,g2)
    c: Coincident(g3,g0)
    c: Vertical(g3)
    c: DistanceX(g2,g2) = 7.6
    c: Coincident(g1,g-3)
    c: Coincident(g0,g-3)
    c: Horizontal(g4)
    c: Coincident(g5,g4)
    c: Vertical(g5)
    c: Coincident(g6,g5)
    c: Horizontal(g6)
    c: Coincident(g7,g6)
    c: Coincident(g7,g4)
    c: Vertical(g7)
    c: DistanceY(g5,g5) = 5.6
    c: DistanceX(g4,g4) = 9.6
    c: Coincident(g9,g8)
    c: Vertical(g9)
    c: Coincident(g10,g9)
    c: Horizontal(g10)
    c: Coincident(g11,g10)
    c: Coincident(g11,g8)
    c: Vertical(g11)
    c: DistanceY(g9,g9) = 5.6
    c: DistanceX(g10,g10) = 8
    c: Coincident(g4,g-4)
    c: DistanceX(g4,g10) = 1.6
    c: Horizontal(g8)
    c: DistanceY(g8,g1) = 0
FEATURE [Sketcher::SketchObject] Sketch034  label="buchi guida rail"
  ArcFitTolerance = 1e-06
  AttachmentSupport = -> [XY_Plane]
  ExternalGeometry = -> [Sketch]
  FullyConstrained = true
  MakeInternals = false
  MapMode = 5
  sketch-geometry (6):
    g0: LineSegment [constr] StartX=-100.8 StartY=9.1e-15 StartZ=0 EndX=-93.3 EndY=0 EndZ=0
    g1: LineSegment [constr] StartX=-93.3 StartY=0 StartZ=0 EndX=-73.3 EndY=0 EndZ=0
    g2: LineSegment [constr] StartX=-73.3 StartY=0 StartZ=0 EndX=-53.3 EndY=0 EndZ=0
    g3: Circle CenterX=-93.3 CenterY=0 CenterZ=0 NormalX=0 NormalY=0 NormalZ=1 AngleXU=0 Radius=2.5
    g4: Circle CenterX=-73.3 CenterY=0 CenterZ=0 NormalX=0 NormalY=0 NormalZ=1 AngleXU=0 Radius=2.5
    g5: Circle CenterX=-53.3 CenterY=0 CenterZ=0 NormalX=0 NormalY=0 NormalZ=1 AngleXU=0 Radius=2.5
  constraints (15):
    c: Distance(g0) = 7.5
    c: Coincident(g0,g-3)
    c: PointOnObject(g0,g-1)
    c: Distance(g1) = 20
    c: Coincident(g1,g0)
    c: PointOnObject(g1,g-1)
    c: Distance(g2) = 20
    c: Coincident(g2,g1)
    c: PointOnObject(g2,g-1)
    c: Diameter(g3) = 5
    c: Diameter(g4) = 5
    c: Diameter(g5) = 5
    c: Coincident(g3,g0)
    c: Coincident(g4,g1)
    c: Coincident(g5,g2)
FEATURE [Part::Extrusion] Extrude032  label="Extrude buchi guida rail"
  Base = -> Sketch034
  Dir = (0,0,1)
  DirMode = 2
  FaceMakerClass = Part::FaceMakerBullseye
  FaceMakerMode = 3
  LengthFwd = -6.2
  LengthRev = 0
  Placement = pos=(0,0,43.2) rot=(0,0,1;0rad)
  Solid = true
  Symmetric = false
FEATURE [Part::Extrusion] Extrude033  label="Extrude fori superiori per solenoide e oled001"
  Base = -> Sketch030
  Dir = (0,0,1)
  DirMode = 2
  FaceMakerClass = Part::FaceMakerBullseye
  FaceMakerMode = 3
  LengthFwd = -4.8
  LengthRev = 0
  Placement = pos=(0,0,41.2) rot=(0,0,1;0rad)
  Solid = true
  Symmetric = false
FEATURE [Part::Extrusion] Extrude034  label="Extrude fori sotto impugnatura001"
  Base = -> Sketch029
  Dir = (0,0,1)
  DirMode = 2
  FaceMakerClass = Part::FaceMakerBullseye
  FaceMakerMode = 3
  LengthFwd = 5
  LengthRev = 0
  Placement = pos=(0,0,-83) rot=(0,0,1;0rad)
  Solid = true
  Symmetric = false
FEATURE [Part::Extrusion] Extrude035  label="Extrude fori inferiori switch pompa001"
  Base = -> Sketch031
  Dir = (0,0,1)
  DirMode = 2
  FaceMakerClass = Part::FaceMakerBullseye
  FaceMakerMode = 3
  LengthFwd = 4
  LengthRev = 0
  Placement = pos=(0,0,-1.7) rot=(0,0,1;0rad)
  Solid = true
  Symmetric = false
FEATURE [Part::Extrusion] Extrude036  label="Extrude foro sotto posteriore M3x5x007"
  Base = -> Sketch027
  Dir = (0,0,1)
  DirMode = 2
  FaceMakerClass = Part::FaceMakerBullseye
  FaceMakerMode = 3
  LengthFwd = 6.2
  LengthRev = 0
  Placement = pos=(0,0,-9.6) rot=(0,0,1;0rad)
  Solid = true
  Symmetric = false
FEATURE [Part::Extrusion] Extrude037  label="Extrude foro sotto anteriore M3x5x007"
  Base = -> Sketch026
  Dir = (0,0,1)
  DirMode = 2
  FaceMakerClass = Part::FaceMakerBullseye
  FaceMakerMode = 3
  LengthFwd = 6.2
  LengthRev = 0
  Solid = true
  Symmetric = false
FEATURE [Sketcher::SketchObject] Sketch035  label="foro per fissaggio micro"
  ArcFitTolerance = 1e-06
  AttachmentSupport = -> [XZ_Plane]
  ExternalGeometry = -> [Sketch,Sketch033]
  FullyConstrained = true
  MakeInternals = false
  MapMode = 5
  Placement = pos=(0,0,0) rot=(1,0,0;1.5708rad)
  sketch-geometry (3):
    g0: Circle CenterX=-7.8 CenterY=21.2 CenterZ=0 NormalX=0 NormalY=0 NormalZ=1 AngleXU=0 Radius=1.6
    g1: GeomPoint [constr] X=-4 Y=21.2 Z=0
    g2: LineSegment [constr] StartX=-4 StartY=21.2 StartZ=0 EndX=-11.6 EndY=21.2 EndZ=0
  constraints (6):
    c: Diameter(g0) = 3.2
    c: Symmetric(g-3,g-3,g1)
    c: Coincident(g2,g1)
    c: Horizontal(g2)
    c: DistanceX(g-4,g2) = 0
    c: Symmetric(g2,g1,g0)
FEATURE [Part::Extrusion] Extrude038  label="Extrude foro per fissaggio micro"
  Base = -> Sketch035
  Dir = (0,-1,2e-16)
  DirMode = 2
  FaceMakerClass = Part::FaceMakerBullseye
  FaceMakerMode = 3
  LengthFwd = 3
  LengthRev = 0
  Placement = pos=(0,8.6,0) rot=(0,0,1;0rad)
  Solid = true
  Symmetric = false
FEATURE [Sketcher::SketchObject] Sketch036  label="supporto per alimentatore"
  ArcFitTolerance = 1e-06
  AttachmentSupport = -> [XZ_Plane]
  ExternalGeometry = -> [Sketch,Sketch016,Sketch022]
  FullyConstrained = true
  MakeInternals = false
  MapMode = 5
  Placement = pos=(0,0,0) rot=(1,0,0;1.5708rad)
  sketch-geometry (5):
    g0: LineSegment StartX=-211.843 StartY=-50.0944 StartZ=0 EndX=-211.843 EndY=-80.4316 EndZ=0
    g1: LineSegment StartX=-211.843 StartY=-50.0944 StartZ=0 EndX=-207.775 EndY=-41.3701 EndZ=0
    g2: LineSegment [constr] StartX=-209.443 StartY=-50.0944 StartZ=0 EndX=-209.443 EndY=-80.4316 EndZ=0
    g3: LineSegment StartX=-207.775 StartY=-41.3701 StartZ=0 EndX=-207.775 EndY=-80.4316 EndZ=0
    g4: LineSegment StartX=-211.843 StartY=-80.4316 StartZ=0 EndX=-207.775 EndY=-80.4316 EndZ=0
  constraints (15):
    c: Vertical(g0)
    c: Coincident(g1,g0)
    c: Vertical(g2)
    c: Tangent(g2,g-5)
    c: Coincident(g3,g1)
    c: Vertical(g3)
    c: DistanceY(g-3,g3) = -2
    c: Tangent(g1,g-8)
    c: DistanceY(g-3,g0) = -2
    c: Coincident(g4,g0)
    c: Coincident(g4,g3)
    c: Tangent(g0,g-6)
    c: DistanceY(g-3,g2) = -2
    c: DistanceY(g2,g0) = 0
    c: DistanceX(g-3,g3) = 6.8
FEATURE [Part::Extrusion] Extrude039  label="Extrude039 supporto alimentatore"
  Base = -> Sketch036
  Dir = (0,-1,2e-16)
  DirMode = 2
  FaceMakerClass = Part::FaceMakerBullseye
  FaceMakerMode = 3
  LengthFwd = 25.2
  LengthRev = 0
  Solid = true
  Symmetric = true
FEATURE [Sketcher::SketchObject] Sketch037  label="scavo per alimentatore"
  ArcFitTolerance = 1e-06
  AttachmentSupport = -> [XZ_Plane]
  ExternalGeometry = -> [Sketch036]
  FullyConstrained = true
  MakeInternals = false
  MapMode = 5
  Placement = pos=(0,0,0) rot=(1,0,0;1.5708rad)
  sketch-geometry (4):
    g0: LineSegment StartX=-209.575 StartY=-50.4316 StartZ=0 EndX=-209.575 EndY=-80.4316 EndZ=0
    g1: LineSegment StartX=-209.575 StartY=-50.4316 StartZ=0 EndX=-207.775 EndY=-50.4316 EndZ=0
    g2: LineSegment StartX=-207.775 StartY=-50.4316 StartZ=0 EndX=-207.775 EndY=-80.4316 EndZ=0
    g3: LineSegment StartX=-207.775 StartY=-80.4316 StartZ=0 EndX=-209.575 EndY=-80.4316 EndZ=0
  constraints (11):
    c: Vertical(g0)
    c: Coincident(g1,g0)
    c: Horizontal(g1)
    c: Coincident(g2,g1)
    c: Vertical(g2)
    c: Coincident(g3,g2)
    c: Coincident(g3,g0)
    c: Horizontal(g3)
    c: DistanceX(g1,g1) = 1.8
    c: Coincident(g2,g-3)
    c: DistanceY(g2,g2) = 30
FEATURE [Part::Extrusion] Extrude040  label="Extrude040 scavo alimentatore"
  Base = -> Sketch037
  Dir = (0,-1,2e-16)
  DirMode = 2
  FaceMakerClass = Part::FaceMakerBullseye
  FaceMakerMode = 3
  LengthFwd = 19.5
  LengthRev = 0
  Solid = true
  Symmetric = true
FEATURE [Part::Extrusion] Extrude031  label="Extrude fermo per scheda micro"
  Base = -> Sketch033
  Dir = (0,-1,2e-16)
  DirMode = 2
  FaceMakerClass = Part::FaceMakerBullseye
  FaceMakerMode = 3
  LengthFwd = 3
  LengthRev = 0
  Placement = pos=(0,8.6,0) rot=(0,0,1;0rad)
  Solid = true
  Symmetric = false
FEATURE [Sketcher::SketchObject] Sketch038  label="scavo driver solenoide"
  ArcFitTolerance = 1e-06
  AttachmentSupport = -> [XZ_Plane]
  ExternalGeometry = -> [Sketch,Sketch036]
  FullyConstrained = true
  MakeInternals = false
  MapMode = 5
  Placement = pos=(0,0,0) rot=(1,0,0;1.5708rad)
  sketch-geometry (7):
    g0: LineSegment StartX=-193.66 StartY=-11.0994 StartZ=0 EndX=-195.11 EndY=-10.4232 EndZ=0
    g1: LineSegment StartX=-195.11 StartY=-10.4232 StartZ=0 EndX=-209.225 EndY=-40.6939 EndZ=0
    g2: LineSegment StartX=-193.66 StartY=-11.0994 StartZ=0 EndX=-190.216 EndY=-12.7054 EndZ=0
    g3: LineSegment StartX=-190.216 StartY=-12.7054 StartZ=0 EndX=-204.331 EndY=-42.9761 EndZ=0
    g4: LineSegment StartX=-204.331 StartY=-42.9761 StartZ=0 EndX=-207.775 EndY=-41.3701 EndZ=0
    g5: LineSegment [constr] StartX=-209.225 StartY=-40.6939 StartZ=0 EndX=-207.775 EndY=-41.3701 EndZ=0
    g6: LineSegment StartX=-209.225 StartY=-40.6939 StartZ=0 EndX=-207.775 EndY=-41.3701 EndZ=0
  constraints (19):
    c: Coincident(g1,g0)
    c: Coincident(g3,g2)
    c: Coincident(g4,g3)
    c: Distance(g2) = 3.8
    c: Distance(g1) = 33.4
    c: Coincident(g5,g1)
    c: Distance(g5) = 1.6
    c: Coincident(g-4,g5)
    c: Perpendicular(g5,g-3)
    c: Parallel(g1,g-3)
    c: Perpendicular(g1,g0)
    c: Distance(g0) = 1.6
    c: Coincident(g6,g1)
    c: Coincident(g6,g5)
    c: Parallel(g3,g-3)
    c: Perpendicular(g3,g4)
    c: Perpendicular(g2,g3)
    c: Coincident(g2,g0)
    c: Coincident(g4,g5)
FEATURE [Part::Extrusion] Extrude041  label="Extrude scavo driver solenoide"
  Base = -> Sketch038
  Dir = (0,-1,2e-16)
  DirMode = 2
  FaceMakerClass = Part::FaceMakerBullseye
  FaceMakerMode = 3
  LengthFwd = 17
  LengthRev = 0
  Solid = true
  Symmetric = true
FEATURE [Sketcher::SketchObject] Sketch039  label="scavo per cavo usb per micro"
  ArcFitTolerance = 1e-06
  AttachmentSupport = -> [XZ_Plane]
  ExternalGeometry = -> [Sketch,Sketch016]
  FullyConstrained = true
  MakeInternals = false
  MapMode = 5
  Placement = pos=(0,0,0) rot=(1,0,0;1.5708rad)
  sketch-geometry (4):
    g0: LineSegment StartX=-82.51 StartY=36.4 StartZ=0 EndX=-74.51 EndY=36.4 EndZ=0
    g1: LineSegment StartX=-74.51 StartY=36.4 StartZ=0 EndX=-74.51 EndY=30.8 EndZ=0
    g2: LineSegment StartX=-74.51 StartY=30.8 StartZ=0 EndX=-82.51 EndY=30.8 EndZ=0
    g3: LineSegment StartX=-82.51 StartY=30.8 StartZ=0 EndX=-82.51 EndY=36.4 EndZ=0
  constraints (11):
    c: Coincident(g1,g0)
    c: Vertical(g1)
    c: Coincident(g2,g1)
    c: Horizontal(g2)
    c: Coincident(g3,g2)
    c: Coincident(g3,g0)
    c: Vertical(g3)
    c: Tangent(g0,g-3)
    c: Tangent(g2,g-4)
    c: Tangent(g3,g-4)
    c: Tangent(g1,g-4)
FEATURE [Part::Extrusion] Extrude042  label="Extrude scavo per cavo usb per micro"
  Base = -> Sketch039
  Dir = (0,-1,2e-16)
  DirMode = 2
  FaceMakerClass = Part::FaceMakerBullseye
  FaceMakerMode = 3
  LengthFwd = 11.2
  LengthRev = 0
  Solid = true
  Symmetric = true
FEATURE [Sketcher::SketchObject] Sketch040  label="scavo saldature alimentatore connettore 5v"
  ArcFitTolerance = 1e-06
  AttachmentSupport = -> [XZ_Plane]
  ExternalGeometry = -> [Sketch037]
  FullyConstrained = true
  MakeInternals = false
  MapMode = 5
  Placement = pos=(0,0,0) rot=(1,0,0;1.5708rad)
  sketch-geometry (4):
    g0: LineSegment StartX=-211.175 StartY=-52.4316 StartZ=0 EndX=-211.175 EndY=-56.4316 EndZ=0
    g1: LineSegment StartX=-211.175 StartY=-52.4316 StartZ=0 EndX=-209.575 EndY=-52.4316 EndZ=0
    g2: LineSegment StartX=-209.575 StartY=-52.4316 StartZ=0 EndX=-209.575 EndY=-56.4316 EndZ=0
    g3: LineSegment StartX=-209.575 StartY=-56.4316 StartZ=0 EndX=-211.175 EndY=-56.4316 EndZ=0
  constraints (11):
    c: Vertical(g0)
    c: Coincident(g1,g0)
    c: Horizontal(g1)
    c: Coincident(g2,g1)
    c: Coincident(g3,g2)
    c: Coincident(g3,g0)
    c: Horizontal(g3)
    c: DistanceX(g1,g1) = 1.6
    c: DistanceY(g2,g2) = 4
    c: Tangent(g2,g-3)
    c: DistanceY(g1,g-3) = 2
FEATURE [Part::Extrusion] Extrude043  label="Extrude scavo saldature alimentatore connettore 5v"
  Base = -> Sketch040
  Dir = (0,-1,2e-16)
  DirMode = 2
  FaceMakerClass = Part::FaceMakerBullseye
  FaceMakerMode = 3
  LengthFwd = 8
  LengthRev = 0
  Solid = true
  Symmetric = true
FEATURE [Sketcher::SketchObject] Sketch041  label="scavo saldature alimentatore connettore 5v verticali"
  ArcFitTolerance = 1e-06
  AttachmentSupport = -> [XZ_Plane]
  ExternalGeometry = -> [Sketch037]
  FullyConstrained = true
  MakeInternals = false
  MapMode = 5
  Placement = pos=(0,0,0) rot=(1,0,0;1.5708rad)
  sketch-geometry (4):
    g0: LineSegment StartX=-211.175 StartY=-53.6316 StartZ=0 EndX=-209.575 EndY=-53.6316 EndZ=0
    g1: LineSegment StartX=-209.575 StartY=-53.6316 StartZ=0 EndX=-209.575 EndY=-76.6316 EndZ=0
    g2: LineSegment StartX=-209.575 StartY=-76.6316 StartZ=0 EndX=-211.175 EndY=-76.6316 EndZ=0
    g3: LineSegment StartX=-211.175 StartY=-76.6316 StartZ=0 EndX=-211.175 EndY=-53.6316 EndZ=0
  constraints (11):
    c: Horizontal(g0)
    c: Coincident(g1,g0)
    c: Coincident(g2,g1)
    c: Horizontal(g2)
    c: Coincident(g3,g2)
    c: Coincident(g3,g0)
    c: Vertical(g3)
    c: DistanceY(g3,g3) = 23
    c: DistanceX(g0,g0) = 1.6
    c: Tangent(g1,g-3)
    c: DistanceY(g0,g-3) = 3.2
FEATURE [Part::Extrusion] Extrude044  label="Extrude scavo saldature alimentatore connettore 5v verticali"
  Base = -> Sketch041
  Dir = (0,-1,2e-16)
  DirMode = 2
  FaceMakerClass = Part::FaceMakerBullseye
  FaceMakerMode = 3
  LengthFwd = 3.2
  LengthRev = 0
  Placement = pos=(0,8.3,0) rot=(0,0,1;0rad)
  Solid = true
  Symmetric = false
FEATURE [Sketcher::SketchObject] Sketch042  label="fermi per driver solenoide e alimentatore"
  ArcFitTolerance = 1e-06
  AttachmentSupport = -> [XZ_Plane]
  ExternalGeometry = -> [Sketch036,Sketch037,Sketch,Sketch038]
  FullyConstrained = true
  MakeInternals = false
  MapMode = 5
  Placement = pos=(0,0,0) rot=(1,0,0;1.5708rad)
  sketch-geometry (27):
    g0: LineSegment StartX=-195.773 StartY=-15.631 StartZ=0 EndX=-196.702 EndY=-17.6249 EndZ=0
    g1: LineSegment StartX=-196.702 StartY=-17.6249 StartZ=0 EndX=-194.709 EndY=-18.5546 EndZ=0
    g2: LineSegment StartX=-194.709 StartY=-18.5546 StartZ=0 EndX=-193.779 EndY=-16.5607 EndZ=0
    g3: LineSegment StartX=-193.779 StartY=-16.5607 StartZ=0 EndX=-195.773 EndY=-15.631 EndZ=0
    g4: LineSegment StartX=-196.547 StartY=-13.5047 StartZ=0 EndX=-198.829 EndY=-18.3988 EndZ=0
    g5: LineSegment StartX=-198.829 StartY=-18.3988 StartZ=0 EndX=-195.385 EndY=-20.0047 EndZ=0
    g6: LineSegment StartX=-193.258 StartY=-19.2308 StartZ=0 EndX=-192.329 EndY=-17.2369 EndZ=0
    g7: LineSegment StartX=-193.103 StartY=-15.1106 StartZ=0 EndX=-196.547 EndY=-13.5047 EndZ=0
    g8: LineSegment [constr] StartX=-193.935 StartY=-20.6809 StartZ=0 EndX=-193.258 EndY=-19.2308 EndZ=0
    g9: LineSegment [constr] StartX=-193.935 StartY=-20.6809 StartZ=0 EndX=-195.385 EndY=-20.0047 EndZ=0
    g10: ArcOfCircle CenterX=-193.779 CenterY=-16.5607 CenterZ=0 NormalX=0 NormalY=0 NormalZ=1 AngleXU=0 Radius=1.6 StartAngle=5.84685 EndAngle=7.41765
    g11: GeomPoint [constr] X=-191.653 Y=-15.7868 Z=0
    g12: ArcOfCircle CenterX=-194.709 CenterY=-18.5546 CenterZ=0 NormalX=0 NormalY=0 NormalZ=1 AngleXU=0 Radius=1.6 StartAngle=4.27606 EndAngle=5.84685
    g13: GeomPoint [constr] X=-193.935 Y=-20.6809 Z=0
    g14: LineSegment StartX=-207.775 StartY=-46.8316 StartZ=0 EndX=-207.775 EndY=-50.8316 EndZ=0
    g15: LineSegment StartX=-207.775 StartY=-46.8316 StartZ=0 EndX=-203.775 EndY=-46.8316 EndZ=0
    g16: LineSegment StartX=-203.775 StartY=-46.8316 StartZ=0 EndX=-203.775 EndY=-50.8316 EndZ=0
    g17: LineSegment StartX=-207.775 StartY=-50.8316 StartZ=0 EndX=-203.775 EndY=-50.8316 EndZ=0
    g18: LineSegment StartX=-209.375 StartY=-52.4316 StartZ=0 EndX=-203.775 EndY=-52.4316 EndZ=0
    g19: LineSegment StartX=-202.175 StartY=-50.8316 StartZ=0 EndX=-202.175 EndY=-46.8316 EndZ=0
    g20: LineSegment StartX=-203.775 StartY=-45.2316 StartZ=0 EndX=-209.375 EndY=-45.2316 EndZ=0
    g21: LineSegment StartX=-209.375 StartY=-45.2316 StartZ=0 EndX=-209.375 EndY=-52.4316 EndZ=0
    g22: ArcOfCircle CenterX=-203.775 CenterY=-46.8316 CenterZ=0 NormalX=0 NormalY=0 NormalZ=1 AngleXU=0 Radius=1.6 StartAngle=1.8e-15 EndAngle=1.5708
    g23: GeomPoint [constr] X=-202.175 Y=-45.2316 Z=0
    g24: ArcOfCircle CenterX=-203.775 CenterY=-50.8316 CenterZ=0 NormalX=0 NormalY=0 NormalZ=1 AngleXU=0 Radius=1.6 StartAngle=4.71239 EndAngle=6.28319
    g25: GeomPoint [constr] X=-202.175 Y=-52.4316 Z=0
    g26: LineSegment [constr] StartX=-207.775 StartY=-50.4316 StartZ=0 EndX=-207.775 EndY=-50.8316 EndZ=0
  constraints (69):
    c: Coincident(g1,g0)
    c: Coincident(g2,g1)
    c: Coincident(g3,g2)
    c: Coincident(g3,g0)
    c: Parallel(g0,g2)
    c: Perpendicular(g3,g0)
    c: Perpendicular(g1,g0)
    c: Coincident(g5,g4)
    c: Coincident(g7,g4)
    c: Distance(g3) = 2.2
    c: Distance(g2) = 2.2
    c: Parallel(g6,g2)
    c: Parallel(g6,g4)
    c: Perpendicular(g5,g6)
    c: Perpendicular(g7,g6)
    c: Distance(g13,g11) = 5.4
    c: Distance(g5,g13) = 5.4
    c: Coincident(g9,g8)
    c: Distance(g8) = 1.6
    c: Distance(g9) = 1.6
    c: Perpendicular(g9,g8)
    c: Parallel(g8,g6)
    c: Coincident(g8,g13)
    c: Distance(g8,g1) = 1.6
    c: Distance(g9,g1) = 1.6
    c: Tangent(g0,g-5)
    c: Distance(g0,g-6) = 26.2
    c: PointOnObject(g11,g7)
    c: PointOnObject(g11,g6)
    c: Tangent(g7,g10) = -1.5708
    c: Tangent(g6,g10) = -1.5708
    c: PointOnObject(g13,g5)
    c: Tangent(g5,g12) = -1.5708
    c: Tangent(g6,g12) = -1.5708
    c: Equal(g10,g12)
    c: Coincident(g10,g2)
    c: Vertical(g14)
    c: Coincident(g15,g14)
    c: Horizontal(g15)
    c: Coincident(g16,g15)
    c: Vertical(g16)
    c: Coincident(g17,g14)
    c: Coincident(g17,g16)
    c: Horizontal(g17)
    c: Distance(g16) = 4
    c: Distance(g15) = 4
    c: Horizontal(g18)
    c: Vertical(g19)
    c: Horizontal(g20)
    c: Coincident(g21,g20)
    c: Coincident(g21,g18)
    c: Vertical(g21)
    c: Distance(g20,g23) = 7.2
    c: Distance(g25,g23) = 7.2
    c: DistanceY(g18,g14) = 1.6
    c: DistanceX(g18,g14) = 1.6
    c: PointOnObject(g23,g20)
    c: PointOnObject(g23,g19)
    c: Tangent(g20,g22) = -1.5708
    c: Tangent(g19,g22) = -1.5708
    c: PointOnObject(g25,g19)
    c: Tangent(g18,g24) = -1.5708
    c: Tangent(g19,g24) = -1.5708
    c: Equal(g22,g24)
    c: Coincident(g22,g15)
    c: Vertical(g26)
    c: Distance(g26) = 0.4
    c: Coincident(g26,g-4)
    c: Coincident(g14,g26)
FEATURE [Part::Extrusion] Extrude045  label="Extrude fermi per driver solenoide e alimentatore"
  Base = -> Sketch042
  Dir = (0,-1,2e-16)
  DirMode = 2
  FaceMakerClass = Part::FaceMakerBullseye
  FaceMakerMode = 3
  LengthFwd = 25.2
  LengthRev = 0
  Solid = true
  Symmetric = true
FEATURE [Sketcher::SketchObject] Sketch043  label="scavo pulizia fermo alimentatore"
  ArcFitTolerance = 1e-06
  AttachmentSupport = -> [XZ_Plane]
  ExternalGeometry = -> [Sketch042,Sketch036,Sketch037]
  FullyConstrained = true
  MakeInternals = false
  MapMode = 5
  Placement = pos=(0,0,0) rot=(1,0,0;1.5708rad)
  sketch-geometry (6):
    g0: LineSegment StartX=-209.375 StartY=-52.4316 StartZ=0 EndX=-209.375 EndY=-50.4316 EndZ=0
    g1: LineSegment StartX=-209.375 StartY=-50.4316 StartZ=0 EndX=-207.775 EndY=-50.4316 EndZ=0
    g2: LineSegment StartX=-207.775 StartY=-50.4316 StartZ=0 EndX=-207.775 EndY=-45.2316 EndZ=0
    g3: LineSegment StartX=-207.775 StartY=-45.2316 StartZ=0 EndX=-202.175 EndY=-45.2316 EndZ=0
    g4: LineSegment StartX=-202.175 StartY=-45.2316 StartZ=0 EndX=-202.175 EndY=-52.4316 EndZ=0
    g5: LineSegment StartX=-202.175 StartY=-52.4316 StartZ=0 EndX=-209.375 EndY=-52.4316 EndZ=0
  constraints (13):
    c: Vertical(g0)
    c: Coincident(g1,g0)
    c: Coincident(g2,g1)
    c: Coincident(g3,g2)
    c: Coincident(g4,g3)
    c: Coincident(g5,g4)
    c: Coincident(g5,g0)
    c: Horizontal(g5)
    c: Coincident(g0,g-6)
    c: Tangent(g1,g-8)
    c: Tangent(g2,g-4)
    c: Tangent(g3,g-7)
    c: Tangent(g4,g-3)
FEATURE [Part::Extrusion] Extrude046  label="Extrude scavo pulizia fermo alimentatore"
  Base = -> Sketch043
  Dir = (0,-1,2e-16)
  DirMode = 2
  FaceMakerClass = Part::FaceMakerBullseye
  FaceMakerMode = 3
  LengthFwd = 19.5
  LengthRev = 0
  Solid = true
  Symmetric = true
FEATURE [Sketcher::SketchObject] Sketch044  label="buchini per fissaggio oled"
  ArcFitTolerance = 1e-06
  AttachmentSupport = -> [YZ_Plane]
  ExternalGeometry = -> [Sketch]
  FullyConstrained = true
  MakeInternals = false
  MapMode = 5
  Placement = pos=(0,0,0) rot=(0.57735,0.57735,0.57735;2.0944rad)
  sketch-geometry (5):
    g0: LineSegment [constr] StartX=1.5e-14 StartY=67.3588 StartZ=0 EndX=0 EndY=64.3588 EndZ=0
    g1: LineSegment [constr] StartX=0 StartY=64.3588 StartZ=0 EndX=10.4 EndY=64.3588 EndZ=0
    g2: LineSegment [constr] StartX=0 StartY=64.3588 StartZ=0 EndX=-10.4 EndY=64.3588 EndZ=0
    g3: Circle CenterX=10.4 CenterY=64.3588 CenterZ=0 NormalX=0 NormalY=0 NormalZ=1 AngleXU=0 Radius=1.5
    g4: Circle CenterX=-10.4 CenterY=64.3588 CenterZ=0 NormalX=0 NormalY=0 NormalZ=1 AngleXU=0 Radius=1.5
  constraints (13):
    c: Distance(g0) = 3
    c: PointOnObject(g0,g-2)
    c: Coincident(g1,g0)
    c: Horizontal(g1)
    c: Coincident(g2,g0)
    c: Horizontal(g2)
    c: DistanceX(g1,g1) = 10.4
    c: Coincident(g3,g1)
    c: Diameter(g4) = 3
    c: Coincident(g4,g2)
    c: Coincident(g0,g-7)
    c: Equal(g1,g2)
    c: Equal(g4,g3)
FEATURE [Part::Extrusion] Extrude047  label="Extrude buchini per fissaggio oled"
  Base = -> Sketch044
  Dir = (1,0,0)
  DirMode = 2
  FaceMakerClass = Part::FaceMakerBullseye
  FaceMakerMode = 3
  LengthFwd = 10
  LengthRev = 0
  Placement = pos=(-186,0,0) rot=(0,0,1;0rad)
  Solid = true
  Symmetric = false
FEATURE [Sketcher::SketchObject] Sketch046  label="scavo 5x5 neopixel"
  ArcFitTolerance = 1e-06
  AttachmentSupport = -> [YZ_Plane002]
  FullyConstrained = true
  MakeInternals = false
  MapMode = 5
  Placement = pos=(0,0,0) rot=(0.57735,0.57735,0.57735;2.0944rad)
  sketch-geometry (4):
    g0: LineSegment StartX=-2.7 StartY=2.7 StartZ=0 EndX=2.7 EndY=2.7 EndZ=0
    g1: LineSegment StartX=2.7 StartY=2.7 StartZ=0 EndX=2.7 EndY=-2.7 EndZ=0
    g2: LineSegment StartX=2.7 StartY=-2.7 StartZ=0 EndX=-2.7 EndY=-2.7 EndZ=0
    g3: LineSegment StartX=-2.7 StartY=-2.7 StartZ=0 EndX=-2.7 EndY=2.7 EndZ=0
  constraints (11):
    c: Horizontal(g0)
    c: Coincident(g1,g0)
    c: Vertical(g1)
    c: Coincident(g2,g1)
    c: Horizontal(g2)
    c: Coincident(g3,g2)
    c: Coincident(g3,g0)
    c: Vertical(g3)
    c: DistanceX(g0,g0) = 5.4
    c: DistanceY(g1,g1) = 5.4
    c: Symmetric(g0,g1,g-1)
FEATURE [Part::Extrusion] Extrude049  label="Extrude scavo 5x5 neopixel"
  Base = -> Sketch046
  Dir = (1,0,0)
  DirMode = 2
  FaceMakerClass = Part::FaceMakerBullseye
  FaceMakerMode = 3
  LengthFwd = 1
  LengthRev = 0
  Solid = true
  Symmetric = false
FEATURE [Sketcher::SketchObject] Sketch047  label="scavo 10x10 neopixel corpo"
  ArcFitTolerance = 1e-06
  AttachmentSupport = -> [YZ_Plane002]
  FullyConstrained = true
  MakeInternals = false
  MapMode = 5
  Placement = pos=(0,0,0) rot=(0.57735,0.57735,0.57735;2.0944rad)
  sketch-geometry (4):
    g0: LineSegment StartX=-5 StartY=5.1 StartZ=0 EndX=5 EndY=5.1 EndZ=0
    g1: LineSegment StartX=5 StartY=5.1 StartZ=0 EndX=5 EndY=-5.1 EndZ=0
    g2: LineSegment StartX=5 StartY=-5.1 StartZ=0 EndX=-5 EndY=-5.1 EndZ=0
    g3: LineSegment StartX=-5 StartY=-5.1 StartZ=0 EndX=-5 EndY=5.1 EndZ=0
  constraints (11):
    c: Horizontal(g0)
    c: Coincident(g1,g0)
    c: Vertical(g1)
    c: Coincident(g2,g1)
    c: Horizontal(g2)
    c: Coincident(g3,g2)
    c: Coincident(g3,g0)
    c: Vertical(g3)
    c: DistanceX(g0,g0) = 10
    c: DistanceY(g1,g1) = 10.2
    c: Symmetric(g0,g2,g-1)
FEATURE [Part::Extrusion] Extrude050  label="Extrude scavo 10x10 neopixel corpo"
  Base = -> Sketch047
  Dir = (1,0,0)
  DirMode = 2
  FaceMakerClass = Part::FaceMakerBullseye
  FaceMakerMode = 3
  LengthFwd = 8
  LengthRev = 0
  Placement = pos=(1,0,0) rot=(0,0,1;0rad)
  Solid = true
  Symmetric = false
FEATURE [Sketcher::SketchObject] Sketch048  label="buco per perno blocco neopixel"
  ArcFitTolerance = 1e-06
  AttachmentSupport = -> [XZ_Plane002]
  FullyConstrained = true
  MakeInternals = false
  MapMode = 5
  Placement = pos=(0,0,0) rot=(1,0,0;1.5708rad)
  sketch-geometry (4):
    g0: LineSegment StartX=3 StartY=1.2 StartZ=0 EndX=3 EndY=-1.2 EndZ=0
    g1: LineSegment StartX=3 StartY=-1.2 StartZ=0 EndX=5.4 EndY=-1.2 EndZ=0
    g2: LineSegment StartX=5.4 StartY=-1.2 StartZ=0 EndX=5.4 EndY=1.2 EndZ=0
    g3: LineSegment StartX=5.4 StartY=1.2 StartZ=0 EndX=3 EndY=1.2 EndZ=0
  constraints (11):
    c: Coincident(g1,g0)
    c: Horizontal(g1)
    c: Coincident(g2,g1)
    c: Vertical(g2)
    c: Coincident(g3,g2)
    c: Coincident(g3,g0)
    c: Horizontal(g3)
    c: DistanceX(g1,g1) = 2.4
    c: DistanceY(g2,g2) = 2.4
    c: Symmetric(g0,g0,g-1)
    c: DistanceX(g-1,g0) = 3
FEATURE [Sketcher::SketchObject] Sketch045  label="blocco principale per neopixel"
  ArcFitTolerance = 1e-06
  AttachmentSupport = -> [XZ_Plane002]
  ExternalGeometry = -> [Sketch048]
  FullyConstrained = true
  MakeInternals = false
  MapMode = 5
  Placement = pos=(0,0,0) rot=(1,0,0;1.5708rad)
  sketch-geometry (6):
    g0: LineSegment StartX=0 StartY=5.1 StartZ=0 EndX=0 EndY=-5.1 EndZ=0
    g1: LineSegment StartX=0 StartY=-5.1 StartZ=0 EndX=3 EndY=-5.1 EndZ=0
    g2: LineSegment StartX=7 StartY=-1.1 StartZ=0 EndX=7 EndY=5.1 EndZ=0
    g3: LineSegment StartX=7 StartY=5.1 StartZ=0 EndX=0 EndY=5.1 EndZ=0
    g4: ArcOfCircle CenterX=3 CenterY=-1.1 CenterZ=0 NormalX=0 NormalY=0 NormalZ=1 AngleXU=0 Radius=4 StartAngle=4.71239 EndAngle=6.28319
    g5: GeomPoint [constr] X=7 Y=-5.1 Z=0
  constraints (15):
    c: Vertical(g0)
    c: Coincident(g1,g0)
    c: Horizontal(g1)
    c: Vertical(g2)
    c: Coincident(g3,g2)
    c: Coincident(g3,g0)
    c: Horizontal(g3)
    c: DistanceY(g0,g0) = 10.2
    c: Symmetric(g0,g0,g-1)
    c: DistanceX(g3,g3) = 7
    c: PointOnObject(g5,g2)
    c: PointOnObject(g5,g1)
    c: Tangent(g2,g4) = -1.5708
    c: Tangent(g1,g4) = -1.5708
    c: DistanceX(g-3,g1) = 0
FEATURE [Part::Extrusion] Extrude048  label="Extrude blocco principale per neopixel"
  Base = -> Sketch045
  Dir = (0,-1,2e-16)
  DirMode = 2
  FaceMakerClass = Part::FaceMakerBullseye
  FaceMakerMode = 3
  LengthFwd = 17
  LengthRev = 0
  Solid = true
  Symmetric = true
FEATURE [Part::Extrusion] Extrude051  label="Extrude buco per perno blocco neopixel"
  Base = -> Sketch048
  Dir = (0,-1,2e-16)
  DirMode = 2
  FaceMakerClass = Part::FaceMakerBullseye
  FaceMakerMode = 3
  LengthFwd = 17
  LengthRev = 0
  Solid = true
  Symmetric = true
FEATURE [Sketcher::SketchObject] Sketch049  label="rinforzi esterni per corpo neopoixel"
  ArcFitTolerance = 1e-06
  AttachmentSupport = -> [XZ_Plane002]
  ExternalGeometry = -> [Sketch045]
  FullyConstrained = true
  MakeInternals = false
  MapMode = 5
  Placement = pos=(0,0,0) rot=(1,0,0;1.5708rad)
  sketch-geometry (8):
    g0: LineSegment StartX=1 StartY=-4.1 StartZ=0 EndX=2 EndY=-4.1 EndZ=0
    g1: LineSegment StartX=2 StartY=-4.1 StartZ=0 EndX=2 EndY=-5.1 EndZ=0
    g2: LineSegment StartX=2 StartY=-5.1 StartZ=0 EndX=1 EndY=-5.1 EndZ=0
    g3: LineSegment StartX=1 StartY=-5.1 StartZ=0 EndX=1 EndY=-4.1 EndZ=0
    g4: LineSegment StartX=1 StartY=5.1 StartZ=0 EndX=2 EndY=5.1 EndZ=0
    g5: LineSegment StartX=2 StartY=5.1 StartZ=0 EndX=2 EndY=4.1 EndZ=0
    g6: LineSegment StartX=2 StartY=4.1 StartZ=0 EndX=1 EndY=4.1 EndZ=0
    g7: LineSegment StartX=1 StartY=4.1 StartZ=0 EndX=1 EndY=5.1 EndZ=0
  constraints (24):
    c: Horizontal(g0)
    c: Coincident(g1,g0)
    c: Vertical(g1)
    c: Coincident(g2,g1)
    c: Horizontal(g2)
    c: Coincident(g3,g2)
    c: Coincident(g3,g0)
    c: Vertical(g3)
    c: Horizontal(g4)
    c: Coincident(g5,g4)
    c: Vertical(g5)
    c: Coincident(g6,g5)
    c: Horizontal(g6)
    c: Coincident(g7,g6)
    c: Coincident(g7,g4)
    c: Vertical(g7)
    c: DistanceX(g4,g4) = 1
    c: DistanceY(g5,g5) = 1
    c: DistanceX(g0,g0) = 1
    c: DistanceY(g1,g1) = 1
    c: DistanceX(g-3,g4) = 1
    c: DistanceY(g-3,g4) = 0
    c: DistanceX(g-4,g2) = 1
    c: DistanceY(g2,g-4) = 0
FEATURE [Part::Extrusion] Extrude052  label="Extrude rinforzi esterni per corpo neopoixel"
  Base = -> Sketch049
  Dir = (0,-1,2e-16)
  DirMode = 2
  FaceMakerClass = Part::FaceMakerBullseye
  FaceMakerMode = 3
  LengthFwd = 17
  LengthRev = 0
  Solid = true
  Symmetric = true
FEATURE [Part::Cut] Cut030
  Base = -> Extrude048
  Refine = true
  Tool = -> Extrude050
FEATURE [Part::Cut] Cut031
  Base = -> Cut030
  Refine = true
  Tool = -> Extrude049
FEATURE [Part::Cut] Cut032
  Base = -> Cut031
  Refine = true
  Tool = -> Extrude051
FEATURE [Part::MultiFuse] Fusion001  label="fusion neopixel"
  Refine = true
  Shapes = -> [Cut032,Extrude052]
FEATURE [Sketcher::SketchObject] Sketch052  label="scavo saldature driver solenoide"
  ArcFitTolerance = 1e-06
  AttachmentSupport = -> [XZ_Plane]
  ExternalGeometry = -> [Sketch038]
  FullyConstrained = true
  MakeInternals = false
  MapMode = 5
  Placement = pos=(0,0,0) rot=(1,0,0;1.5708rad)
  sketch-geometry (4):
    g0: LineSegment StartX=-196.56 StartY=-9.74706 StartZ=0 EndX=-198.25 EndY=-13.3723 EndZ=0
    g1: LineSegment StartX=-198.25 StartY=-13.3723 StartZ=0 EndX=-196.8 EndY=-14.0485 EndZ=0
    g2: LineSegment StartX=-196.8 StartY=-14.0485 StartZ=0 EndX=-195.11 EndY=-10.4232 EndZ=0
    g3: LineSegment StartX=-195.11 StartY=-10.4232 StartZ=0 EndX=-196.56 EndY=-9.74706 EndZ=0
  constraints (11):
    c: Coincident(g1,g0)
    c: Coincident(g2,g1)
    c: Coincident(g3,g2)
    c: Coincident(g3,g0)
    c: Parallel(g2,g0)
    c: Perpendicular(g2,g3)
    c: Perpendicular(g1,g2,g1) = 1.5708
    c: Parallel(g2,g-3)
    c: Distance(g2) = 4
    c: Distance(g3) = 1.6
    c: Coincident(g2,g-3)
FEATURE [Part::Extrusion] Extrude055  label="Extrude scavo saldature driver solenoide"
  Base = -> Sketch052
  Dir = (0,-1,2e-16)
  DirMode = 2
  FaceMakerClass = Part::FaceMakerBullseye
  FaceMakerMode = 3
  LengthFwd = 6
  LengthRev = 0
  Solid = true
  Symmetric = true
FEATURE [Sketcher::SketchObject] Sketch053  label="scavo saldature rumble"
  ArcFitTolerance = 1e-06
  AttachmentSupport = -> [XZ_Plane]
  ExternalGeometry = -> [Sketch019]
  FullyConstrained = true
  MakeInternals = false
  MapMode = 5
  Placement = pos=(0,0,0) rot=(1,0,0;1.5708rad)
  sketch-geometry (4):
    g0: LineSegment StartX=-165.31 StartY=-44.1173 StartZ=0 EndX=-166.547 EndY=-47.9216 EndZ=0
    g1: LineSegment StartX=-166.547 StartY=-47.9216 StartZ=0 EndX=-165.405 EndY=-48.2924 EndZ=0
    g2: LineSegment StartX=-165.405 StartY=-48.2924 StartZ=0 EndX=-164.169 EndY=-44.4881 EndZ=0
    g3: LineSegment StartX=-164.169 StartY=-44.4881 StartZ=0 EndX=-165.31 EndY=-44.1173 EndZ=0
  constraints (11):
    c: Coincident(g1,g0)
    c: Coincident(g2,g1)
    c: Coincident(g3,g2)
    c: Coincident(g3,g0)
    c: Parallel(g0,g2)
    c: Perpendicular(g3,g0)
    c: Perpendicular(g1,g0)
    c: Parallel(g0,g-3)
    c: Distance(g0) = 4
    c: Distance(g1) = 1.2
    c: Coincident(g0,g-3)
FEATURE [Part::Extrusion] Extrude056  label="Extrude scavo saldature rumble"
  Base = -> Sketch053
  Dir = (0,-1,2e-16)
  DirMode = 2
  FaceMakerClass = Part::FaceMakerBullseye
  FaceMakerMode = 3
  LengthFwd = 8.4
  LengthRev = 0
  Solid = true
  Symmetric = true
FEATURE [Sketcher::SketchObject] Sketch054  label="scavo saldature alimentatore connettore USB"
  ArcFitTolerance = 1e-06
  AttachmentSupport = -> [XZ_Plane]
  ExternalGeometry = -> [Sketch037]
  FullyConstrained = true
  MakeInternals = false
  MapMode = 5
  Placement = pos=(0,0,0) rot=(1,0,0;1.5708rad)
  sketch-geometry (4):
    g0: LineSegment StartX=-209.575 StartY=-80.4316 StartZ=0 EndX=-210.375 EndY=-80.4316 EndZ=0
    g1: LineSegment StartX=-210.375 StartY=-80.4316 StartZ=0 EndX=-210.375 EndY=-72.4316 EndZ=0
    g2: LineSegment StartX=-210.375 StartY=-72.4316 StartZ=0 EndX=-209.575 EndY=-72.4316 EndZ=0
    g3: LineSegment StartX=-209.575 StartY=-72.4316 StartZ=0 EndX=-209.575 EndY=-80.4316 EndZ=0
  constraints (11):
    c: Horizontal(g0)
    c: Coincident(g1,g0)
    c: Vertical(g1)
    c: Coincident(g2,g1)
    c: Horizontal(g2)
    c: Coincident(g3,g2)
    c: Coincident(g3,g0)
    c: Vertical(g3)
    c: DistanceX(g0,g0) = 0.8
    c: DistanceY(g3,g3) = 8
    c: Coincident(g0,g-4)
FEATURE [Part::Extrusion] Extrude057  label="Extrude scavo saldature alimentatore connettore USB"
  Base = -> Sketch054
  Dir = (0,-1,2e-16)
  DirMode = 2
  FaceMakerClass = Part::FaceMakerBullseye
  FaceMakerMode = 3
  LengthFwd = 11
  LengthRev = 0
  Solid = true
  Symmetric = true
FEATURE [Sketcher::SketchObject] Sketch055  label="buco interno per micro switch"
  ArcFitTolerance = 1e-06
  AttachmentSupport = -> [XZ_Plane]
  ExternalGeometry = -> [Sketch]
  FullyConstrained = true
  MakeInternals = false
  MapMode = 5
  Placement = pos=(0,0,0) rot=(1,0,0;1.5708rad)
  sketch-geometry (11):
    g0: LineSegment [constr] StartX=-194.483 StartY=34.2854 StartZ=0 EndX=-196.022 EndY=30.0568 EndZ=0
    g1: LineSegment [constr] StartX=-196.022 StartY=30.0568 StartZ=0 EndX=-197.561 EndY=25.8282 EndZ=0
    g2: LineSegment [constr] StartX=-196.022 StartY=30.0568 StartZ=0 EndX=-194.143 EndY=29.3727 EndZ=0
    g3: LineSegment [constr] StartX=-196.022 StartY=30.0568 StartZ=0 EndX=-197.902 EndY=30.7408 EndZ=0
    g4: LineSegment StartX=-196.362 StartY=34.9694 StartZ=0 EndX=-192.604 EndY=33.6014 EndZ=0
    g5: LineSegment StartX=-199.441 StartY=26.5122 StartZ=0 EndX=-195.682 EndY=25.1441 EndZ=0
    g6: LineSegment StartX=-192.604 StartY=33.6014 StartZ=0 EndX=-195.682 EndY=25.1441 EndZ=0
    g7: LineSegment StartX=-196.362 StartY=34.9694 StartZ=0 EndX=-199.441 EndY=26.5122 EndZ=0
    g8: GeomPoint [constr] X=-187.821 Y=29.2 Z=0
    g9: LineSegment [constr] StartX=-188.505 StartY=27.3206 StartZ=0 EndX=-196.022 EndY=30.0568 EndZ=0
    g10: LineSegment [constr] StartX=-187.821 StartY=29.2 StartZ=0 EndX=-188.505 EndY=27.3206 EndZ=0
  constraints (27):
    c: Coincident(g2,g0)
    c: Parallel(g0,g-3)
    c: Tangent(g1,g0) = -1.5708
    c: Perpendicular(g0,g2)
    c: Tangent(g2,g3)
    c: Distance(g0,g1) = 9
    c: Equal(g0,g1)
    c: Distance(g3,g2) = 4
    c: Equal(g2,g3)
    c: Parallel(g3,g4)
    c: Symmetric(g4,g4,g0)
    c: Parallel(g6,g1)
    c: Parallel(g7,g1)
    c: Symmetric(g6,g6,g2)
    c: Symmetric(g5,g5,g1)
    c: Symmetric(g7,g7,g3)
    c: Coincident(g7,g4)
    c: Coincident(g6,g4)
    c: Coincident(g5,g6)
    c: Symmetric(g-3,g-3,g8)
    c: Perpendicular(g-3,g9)
    c: Distance(g9) = 8
    c: Coincident(g3,g9)
    c: Coincident(g10,g8)
    c: Parallel(g10,g-3)
    c: Distance(g10) = 2
    c: Coincident(g10,g9)
FEATURE [Sketcher::SketchObject] Sketch056  label="buco esterno per micro switch"
  ArcFitTolerance = 1e-06
  AttachmentSupport = -> [XZ_Plane]
  ExternalGeometry = -> [Sketch055]
  FullyConstrained = true
  MakeInternals = false
  MapMode = 5
  Placement = pos=(0,0,0) rot=(1,0,0;1.5708rad)
  sketch-geometry (17):
    g0: GeomPoint [constr] X=-194.143 Y=29.3727 Z=0
    g1: GeomPoint [constr] X=-194.483 Y=34.2854 Z=0
    g2: GeomPoint [constr] X=-197.902 Y=30.7408 Z=0
    g3: GeomPoint [constr] X=-197.561 Y=25.8282 Z=0
    g4: GeomPoint [constr] X=-196.022 Y=30.0568 Z=0
    g5: LineSegment [constr] StartX=-194.483 StartY=34.2854 StartZ=0 EndX=-196.022 EndY=30.0568 EndZ=0
    g6: LineSegment [constr] StartX=-196.022 StartY=30.0568 StartZ=0 EndX=-197.561 EndY=25.8282 EndZ=0
    g7: LineSegment [constr] StartX=-197.902 StartY=30.7408 StartZ=0 EndX=-196.022 EndY=30.0568 EndZ=0
    g8: LineSegment [constr] StartX=-196.022 StartY=30.0568 StartZ=0 EndX=-194.143 EndY=29.3727 EndZ=0
    g9: LineSegment [constr] StartX=-195.338 StartY=31.9362 StartZ=0 EndX=-196.022 EndY=30.0568 EndZ=0
    g10: LineSegment [constr] StartX=-196.022 StartY=30.0568 StartZ=0 EndX=-196.706 EndY=28.1774 EndZ=0
    g11: LineSegment [constr] StartX=-196.022 StartY=30.0568 StartZ=0 EndX=-196.821 EndY=30.3475 EndZ=0
    g12: LineSegment [constr] StartX=-196.022 StartY=30.0568 StartZ=0 EndX=-195.223 EndY=29.7661 EndZ=0
    g13: LineSegment StartX=-194.539 StartY=31.6454 StartZ=0 EndX=-195.907 EndY=27.8867 EndZ=0
    g14: LineSegment StartX=-196.137 StartY=32.2269 StartZ=0 EndX=-197.505 EndY=28.4681 EndZ=0
    g15: LineSegment StartX=-196.137 StartY=32.2269 StartZ=0 EndX=-194.539 EndY=31.6454 EndZ=0
    g16: LineSegment StartX=-197.505 StartY=28.4681 StartZ=0 EndX=-195.907 EndY=27.8867 EndZ=0
  constraints (34):
    c: Symmetric(g-5,g-5,g1)
    c: Symmetric(g-5,g-6,g0)
    c: Symmetric(g-6,g-6,g3)
    c: Symmetric(g-5,g-6,g2)
    c: Coincident(g5,g1)
    c: Coincident(g5,g4)
    c: Coincident(g6,g4)
    c: Coincident(g6,g3)
    c: Equal(g5,g6)
    c: Coincident(g7,g2)
    c: Coincident(g7,g4)
    c: Coincident(g8,g4)
    c: Coincident(g8,g0)
    c: Equal(g7,g8)
    c: Coincident(g11,g9)
    c: Coincident(g12,g9)
    c: Tangent(g10,g9) = -1.5708
    c: Perpendicular(g11,g9)
    c: Parallel(g9,g-4)
    c: Equal(g9,g10)
    c: Parallel(g12,g11)
    c: Equal(g11,g12)
    c: Distance(g11,g12) = 1.7
    c: Distance(g9,g10) = 4
    c: Symmetric(g13,g13,g12)
    c: Parallel(g13,g9)
    c: Symmetric(g14,g14,g11)
    c: Symmetric(g15,g15,g9)
    c: Parallel(g15,g11)
    c: Symmetric(g16,g16,g10)
    c: Coincident(g16,g14)
    c: Coincident(g15,g14)
    c: Coincident(g13,g15)
    c: Coincident(g9,g4)
FEATURE [Sketcher::SketchObject] Sketch057  label="buco interno per SWITCH"
  ArcFitTolerance = 1e-06
  AttachmentSupport = -> [XZ_Plane]
  ExternalGeometry = -> [Sketch]
  FullyConstrained = true
  MakeInternals = false
  MapMode = 5
  Placement = pos=(0,0,0) rot=(1,0,0;1.5708rad)
  sketch-geometry (10):
    g0: GeomPoint [constr] X=-187.821 Y=29.2 Z=0
    g1: LineSegment [constr] StartX=-188.505 StartY=27.3206 StartZ=0 EndX=-193.203 EndY=29.0307 EndZ=0
    g2: LineSegment [constr] StartX=-190.809 StartY=35.6086 StartZ=0 EndX=-195.597 EndY=22.4529 EndZ=0
    g3: GeomPoint [constr] X=-193.203 Y=29.0307 Z=0
    g4: LineSegment [constr] StartX=-196.492 StartY=30.2278 StartZ=0 EndX=-189.914 EndY=27.8336 EndZ=0
    g5: LineSegment StartX=-194.098 StartY=36.8056 StartZ=0 EndX=-187.52 EndY=34.4115 EndZ=0
    g6: LineSegment StartX=-194.098 StartY=36.8056 StartZ=0 EndX=-198.886 EndY=23.6499 EndZ=0
    g7: LineSegment StartX=-187.52 StartY=34.4115 StartZ=0 EndX=-192.308 EndY=21.2558 EndZ=0
    g8: LineSegment StartX=-198.886 StartY=23.6499 StartZ=0 EndX=-192.308 EndY=21.2558 EndZ=0
    g9: LineSegment [constr] StartX=-187.821 StartY=29.2 StartZ=0 EndX=-188.505 EndY=27.3206 EndZ=0
  constraints (23):
    c: Symmetric(g-3,g-3,g0)
    c: Perpendicular(g1,g-3)
    c: Parallel(g2,g-3)
    c: Symmetric(g2,g2,g3)
    c: Perpendicular(g2,g4)
    c: Symmetric(g4,g4,g3)
    c: Distance(g2) = 14
    c: Distance(g4) = 7
    c: Distance(g1) = 5
    c: Parallel(g5,g4)
    c: Parallel(g7,g2)
    c: Symmetric(g5,g5,g2)
    c: Symmetric(g6,g6,g4)
    c: Symmetric(g7,g7,g4)
    c: Symmetric(g8,g8,g2)
    c: Coincident(g6,g5)
    c: Coincident(g7,g5)
    c: Coincident(g8,g7)
    c: Coincident(g3,g1)
    c: Coincident(g9,g0)
    c: Parallel(g9,g-3)
    c: Distance(g9) = 2
    c: Coincident(g1,g9)
FEATURE [Sketcher::SketchObject] Sketch058  label="buco esterno per SWITCH"
  ArcFitTolerance = 1e-06
  AttachmentSupport = -> [XZ_Plane]
  ExternalGeometry = -> [Sketch057]
  FullyConstrained = true
  MakeInternals = false
  MapMode = 5
  Placement = pos=(0,0,0) rot=(1,0,0;1.5708rad)
  sketch-geometry (12):
    g0: GeomPoint [constr] X=-190.809 Y=35.6086 Z=0
    g1: GeomPoint [constr] X=-196.492 Y=30.2278 Z=0
    g2: GeomPoint [constr] X=-189.914 Y=27.8336 Z=0
    g3: GeomPoint [constr] X=-195.597 Y=22.4529 Z=0
    g4: GeomPoint [constr] X=-193.203 Y=29.0307 Z=0
    g5: LineSegment [constr] StartX=-192.006 StartY=32.3196 StartZ=0 EndX=-194.4 EndY=25.7418 EndZ=0
    g6: GeomPoint [constr] X=-193.203 Y=29.0307 Z=0
    g7: LineSegment [constr] StartX=-195.082 StartY=29.7148 StartZ=0 EndX=-191.324 EndY=28.3467 EndZ=0
    g8: LineSegment StartX=-193.885 StartY=33.0037 StartZ=0 EndX=-190.127 EndY=31.6356 EndZ=0
    g9: LineSegment StartX=-190.127 StartY=31.6356 StartZ=0 EndX=-192.521 EndY=25.0578 EndZ=0
    g10: LineSegment StartX=-196.28 StartY=26.4258 StartZ=0 EndX=-192.521 EndY=25.0578 EndZ=0
    g11: LineSegment StartX=-193.885 StartY=33.0037 StartZ=0 EndX=-196.28 EndY=26.4258 EndZ=0
  constraints (21):
    c: Symmetric(g-6,g-6,g3)
    c: Symmetric(g-4,g-6,g2)
    c: Symmetric(g-5,g-4,g0)
    c: Symmetric(g-5,g-6,g1)
    c: Symmetric(g1,g2,g4)
    c: Parallel(g5,g-4)
    c: Symmetric(g5,g5,g6)
    c: Perpendicular(g7,g5)
    c: Symmetric(g7,g7,g6)
    c: Distance(g5) = 7
    c: Distance(g7) = 4
    c: Parallel(g8,g7)
    c: Parallel(g11,g5)
    c: Symmetric(g8,g8,g5)
    c: Symmetric(g9,g9,g7)
    c: Symmetric(g10,g10,g5)
    c: Symmetric(g11,g11,g7)
    c: Coincident(g11,g8)
    c: Coincident(g9,g8)
    c: Coincident(g9,g10)
    c: Coincident(g6,g4)
FEATURE [Part::Extrusion] Extrude060  label="Extrude buco interno per SWITCH destro"
  Base = -> Sketch057
  Dir = (0,-1,2e-16)
  DirMode = 2
  FaceMakerClass = Part::FaceMakerBullseye
  FaceMakerMode = 3
  LengthFwd = 13.2
  LengthRev = 0
  Placement = pos=(0,2.6,0) rot=(0,0,1;0rad)
  Solid = true
  Symmetric = false
FEATURE [Part::Extrusion] Extrude061  label="Extrude buco esterno per SWITCH destro"
  Base = -> Sketch058
  Dir = (0,-1,2e-16)
  DirMode = 2
  FaceMakerClass = Part::FaceMakerBullseye
  FaceMakerMode = 3
  LengthFwd = 2
  LengthRev = 0
  Placement = pos=(0,-10.6,0) rot=(0,0,1;0rad)
  Solid = true
  Symmetric = false
FEATURE [Sketcher::SketchObject] Sketch059  label="buco per spazio introduzione SWITCH"
  ArcFitTolerance = 1e-06
  AttachmentSupport = -> [XZ_Plane]
  ExternalGeometry = -> [Sketch057,Sketch010]
  FullyConstrained = true
  MakeInternals = false
  MapMode = 5
  Placement = pos=(0,0,0) rot=(1,0,0;1.5708rad)
  sketch-geometry (8):
    g0: LineSegment [constr] StartX=-201.368 StartY=36.3521 StartZ=0 EndX=-195.094 EndY=34.0687 EndZ=0
    g1: LineSegment [constr] StartX=-194.098 StartY=36.8056 StartZ=0 EndX=-195.094 EndY=34.0687 EndZ=0
    g2: LineSegment StartX=-198.658 StartY=24.2771 StartZ=0 EndX=-199.654 EndY=21.5401 EndZ=0
    g3: LineSegment StartX=-199.654 StartY=21.5401 StartZ=0 EndX=-181.196 EndY=14.822 EndZ=0
    g4: LineSegment StartX=-181.196 StartY=14.822 StartZ=0 EndX=-180.2 EndY=17.559 EndZ=0
    g5: LineSegment StartX=-180.2 StartY=17.559 StartZ=0 EndX=-198.658 EndY=24.2771 EndZ=0
    g6: LineSegment [constr] StartX=-204.932 StartY=26.5605 StartZ=0 EndX=-198.658 EndY=24.2771 EndZ=0
    g7: LineSegment [constr] StartX=-198.658 StartY=24.2771 StartZ=0 EndX=-199.654 EndY=21.5401 EndZ=0
  constraints (20):
    c: Parallel(g1,g-3)
    c: Parallel(g0,g-4)
    c: Coincident(g0,g-4)
    c: Coincident(g1,g-3)
    c: Coincident(g0,g1)
    c: Coincident(g3,g2)
    c: Coincident(g4,g3)
    c: Coincident(g5,g4)
    c: Coincident(g5,g2)
    c: Parallel(g5,g-5)
    c: Parallel(g3,g-5)
    c: Parallel(g4,g-6)
    c: DistanceX(g-6,g4) = 0
    c: Coincident(g6,g-5)
    c: Equal(g6,g0)
    c: Coincident(g7,g6)
    c: Equal(g7,g1)
    c: Tangent(g7,g-3)
    c: Coincident(g2,g6)
    c: Coincident(g2,g7)
FEATURE [Part::Extrusion] Extrude062  label="Extrude buco per spazio introduzione SWITCH"
  Base = -> Sketch059
  Dir = (0,-1,2e-16)
  DirMode = 2
  FaceMakerClass = Part::FaceMakerBullseye
  FaceMakerMode = 3
  LengthFwd = 13.2
  LengthRev = 0
  Solid = true
  Symmetric = true
FEATURE [Part::Extrusion] Extrude063  label="Extrude buco interno per SWITCH sinistro"
  Base = -> Sketch057
  Dir = (0,-1,2e-16)
  DirMode = 2
  FaceMakerClass = Part::FaceMakerBullseye
  FaceMakerMode = 3
  LengthFwd = 13.2
  LengthRev = 0
  Placement = pos=(0,10.6,0) rot=(0,0,1;0rad)
  Solid = true
  Symmetric = false
FEATURE [Part::Extrusion] Extrude064  label="Extrude buco esterno per SWITCH sinistro"
  Base = -> Sketch058
  Dir = (0,-1,2e-16)
  DirMode = 2
  FaceMakerClass = Part::FaceMakerBullseye
  FaceMakerMode = 3
  LengthFwd = 2
  LengthRev = 0
  Placement = pos=(0,12.6,0) rot=(0,0,1;0rad)
  Solid = true
  Symmetric = false
FEATURE [Sketcher::SketchObject] Sketch060  label="prova spazio switch"
  ArcFitTolerance = 1e-06
  AttachmentSupport = -> [XY_Plane003]
  FullyConstrained = true
  MakeInternals = false
  MapMode = 5
  sketch-geometry (12):
    g0: LineSegment StartX=-7.5 StartY=10 StartZ=0 EndX=-7.5 EndY=-10 EndZ=0
    g1: LineSegment StartX=-7.5 StartY=-10 StartZ=0 EndX=7.5 EndY=-10 EndZ=0
    g2: LineSegment StartX=7.5 StartY=-10 StartZ=0 EndX=7.5 EndY=10 EndZ=0
    g3: LineSegment StartX=7.5 StartY=10 StartZ=0 EndX=-7.5 EndY=10 EndZ=0
    g4: GeomPoint [constr] X=0 Y=0 Z=0
    g5: LineSegment StartX=-2.95 StartY=-5.55 StartZ=0 EndX=2.95 EndY=-5.55 EndZ=0
    g6: LineSegment StartX=2.95 StartY=-5.55 StartZ=0 EndX=2.95 EndY=5.55 EndZ=0
    g7: LineSegment StartX=2.95 StartY=5.55 StartZ=0 EndX=-2.95 EndY=5.55 EndZ=0
    g8: LineSegment StartX=-2.95 StartY=5.55 StartZ=0 EndX=-2.95 EndY=-5.55 EndZ=0
    g9: GeomPoint [constr] X=0 Y=0 Z=0
    g10: Circle CenterX=0 CenterY=7.75 CenterZ=0 NormalX=0 NormalY=0 NormalZ=1 AngleXU=0 Radius=1.6
    g11: Circle CenterX=0 CenterY=-7.75 CenterZ=0 NormalX=0 NormalY=0 NormalZ=1 AngleXU=0 Radius=1.6
  constraints (29):
    c: Coincident(g0,g1)
    c: Coincident(g1,g2)
    c: Coincident(g2,g3)
    c: Coincident(g3,g0)
    c: Vertical(g0)
    c: Vertical(g2)
    c: Horizontal(g1)
    c: Horizontal(g3)
    c: Symmetric(g2,g0,g4)
    c: Coincident(g4,g-1)
    c: Distance(g3) = 15
    c: Distance(g2) = 20
    c: Coincident(g5,g6)
    c: Coincident(g6,g7)
    c: Coincident(g7,g8)
    c: Coincident(g8,g5)
    c: Horizontal(g5)
    c: Horizontal(g7)
    c: Vertical(g6)
    c: Vertical(g8)
    c: Symmetric(g7,g5,g9)
    c: Coincident(g9,g4)
    c: Distance(g7) = 5.9
    c: Distance(g6) = 11.1
    c: Diameter(g10) = 3.2
    c: Equal(g10,g11)
    c: Symmetric(g10,g11,g-1)
    c: PointOnObject(g10,g-2)
    c: Distance(g10,g11) = 15.5
FEATURE [Sketcher::SketchObject] Sketch061  label="struttura esterna blocco switch"
  ArcFitTolerance = 1e-06
  AttachmentSupport = -> [XZ_Plane003]
  FullyConstrained = true
  MakeInternals = false
  MapMode = 5
  Placement = pos=(0,0,0) rot=(1,0,0;1.5708rad)
  sketch-geometry (5):
    g0: LineSegment StartX=-1 StartY=-5.1 StartZ=0 EndX=1 EndY=-5.1 EndZ=0
    g1: LineSegment StartX=1 StartY=-5.1 StartZ=0 EndX=1 EndY=5.1 EndZ=0
    g2: LineSegment StartX=1 StartY=5.1 StartZ=0 EndX=-1 EndY=5.1 EndZ=0
    g3: LineSegment StartX=-1 StartY=5.1 StartZ=0 EndX=-1 EndY=-5.1 EndZ=0
    g4: GeomPoint [constr] X=0 Y=0 Z=0
  constraints (12):
    c: Coincident(g0,g1)
    c: Coincident(g1,g2)
    c: Coincident(g2,g3)
    c: Coincident(g3,g0)
    c: Horizontal(g0)
    c: Horizontal(g2)
    c: Vertical(g1)
    c: Vertical(g3)
    c: Symmetric(g2,g0,g4)
    c: Distance(g1,g3) = 2
    c: Distance(g0,g2) = 10.2
    c: Coincident(g4,g-1)
FEATURE [Part::Extrusion] Extrude066  label="Extrude struttura esterna blocco switch"
  Base = -> Sketch061
  Dir = (0,-1,2e-16)
  DirMode = 2
  FaceMakerClass = Part::FaceMakerBullseye
  FaceMakerMode = 3
  LengthFwd = 16.8
  LengthRev = 0
  Solid = true
  Symmetric = true
FEATURE [Sketcher::SketchObject] Sketch062  label="struttura interna blocco switch"
  ArcFitTolerance = 1e-06
  AttachmentSupport = -> [XZ_Plane003]
  ExternalGeometry = -> [Sketch061]
  FullyConstrained = true
  MakeInternals = false
  MapMode = 5
  Placement = pos=(0,0,0) rot=(1,0,0;1.5708rad)
  sketch-geometry (5):
    g0: LineSegment StartX=-1 StartY=3.1 StartZ=0 EndX=-1 EndY=-3.1 EndZ=0
    g1: LineSegment StartX=-1 StartY=-3.1 StartZ=0 EndX=1 EndY=-3.1 EndZ=0
    g2: LineSegment StartX=1 StartY=-3.1 StartZ=0 EndX=1 EndY=3.1 EndZ=0
    g3: LineSegment StartX=1 StartY=3.1 StartZ=0 EndX=-1 EndY=3.1 EndZ=0
    g4: GeomPoint [constr] X=0 Y=0 Z=0
  constraints (12):
    c: Coincident(g0,g1)
    c: Coincident(g1,g2)
    c: Coincident(g2,g3)
    c: Coincident(g3,g0)
    c: Vertical(g0)
    c: Vertical(g2)
    c: Horizontal(g1)
    c: Horizontal(g3)
    c: Symmetric(g2,g0,g4)
    c: Coincident(g4,g-1)
    c: Distance(g0) = 6.2
    c: Equal(g3,g-3)
FEATURE [Part::Extrusion] Extrude067  label="Extrude struttura interna blocco switch"
  Base = -> Sketch062
  Dir = (0,-1,2e-16)
  DirMode = 2
  FaceMakerClass = Part::FaceMakerBullseye
  FaceMakerMode = 3
  LengthFwd = 12.8
  LengthRev = 0
  Solid = true
  Symmetric = true
FEATURE [Part::Cut] Cut036  label="struttura blocco switch"
  Base = -> Extrude066
  Refine = true
  Tool = -> Extrude067
FEATURE [Sketcher::SketchObject] Sketch063  label="blocchi tra switch"
  ArcFitTolerance = 1e-06
  AttachmentSupport = -> [XZ_Plane003]
  ExternalGeometry = -> [Sketch061,Sketch062]
  FullyConstrained = true
  MakeInternals = false
  MapMode = 5
  Placement = pos=(0,0,0) rot=(1,0,0;1.5708rad)
  sketch-geometry (8):
    g0: LineSegment StartX=-3 StartY=5.1 StartZ=0 EndX=-1 EndY=5.1 EndZ=0
    g1: LineSegment StartX=-1 StartY=5.1 StartZ=0 EndX=-1 EndY=3.1 EndZ=0
    g2: LineSegment StartX=-1 StartY=3.1 StartZ=0 EndX=-3 EndY=3.1 EndZ=0
    g3: LineSegment StartX=-3 StartY=3.1 StartZ=0 EndX=-3 EndY=5.1 EndZ=0
    g4: LineSegment StartX=-3 StartY=-3.1 StartZ=0 EndX=-1 EndY=-3.1 EndZ=0
    g5: LineSegment StartX=-1 StartY=-3.1 StartZ=0 EndX=-1 EndY=-5.1 EndZ=0
    g6: LineSegment StartX=-1 StartY=-5.1 StartZ=0 EndX=-3 EndY=-5.1 EndZ=0
    g7: LineSegment StartX=-3 StartY=-5.1 StartZ=0 EndX=-3 EndY=-3.1 EndZ=0
  constraints (20):
    c: Horizontal(g0)
    c: Coincident(g1,g0)
    c: Coincident(g2,g1)
    c: Horizontal(g2)
    c: Coincident(g3,g2)
    c: Coincident(g3,g0)
    c: Vertical(g3)
    c: Horizontal(g4)
    c: Coincident(g5,g4)
    c: Coincident(g6,g5)
    c: Horizontal(g6)
    c: Coincident(g7,g6)
    c: Coincident(g7,g4)
    c: Vertical(g7)
    c: Coincident(g0,g-4)
    c: Coincident(g1,g-5)
    c: Coincident(g4,g-6)
    c: Coincident(g5,g-7)
    c: Distance(g0) = 2
    c: Distance(g4) = 2
FEATURE [PartDesign::Body] Body003  label="blocco switch e neopixel"
  AllowCompound = false
  Group = -> [Sketch060,Sketch061,Sketch062,Sketch063]
  Origin = -> Origin003
FEATURE [Part::Extrusion] Extrude068  label="Extrude blocchi tra switch"
  Base = -> Sketch063
  Dir = (0,-1,2e-16)
  DirMode = 2
  FaceMakerClass = Part::FaceMakerBullseye
  FaceMakerMode = 3
  LengthFwd = 7.6
  LengthRev = 0
  Solid = true
  Symmetric = true
FEATURE [Part::MultiFuse] Fusion002  label="Fusion blocco switch"
  Refine = true
  Shapes = -> [Cut036,Extrude068]
FEATURE [Sketcher::SketchObject] Sketch066  label="piano per rampino"
  ArcFitTolerance = 1e-06
  AttachmentSupport = -> [XZ_Plane002]
  ExternalGeometry = -> [Sketch045]
  FullyConstrained = true
  MakeInternals = false
  MapMode = 5
  Placement = pos=(0,0,0) rot=(1,0,0;1.5708rad)
  sketch-geometry (4):
    g0: LineSegment StartX=5.4 StartY=5.1 StartZ=0 EndX=5.4 EndY=3.9 EndZ=0
    g1: LineSegment StartX=5.4 StartY=3.9 StartZ=0 EndX=7 EndY=3.9 EndZ=0
    g2: LineSegment StartX=7 StartY=3.9 StartZ=0 EndX=7 EndY=5.1 EndZ=0
    g3: LineSegment StartX=7 StartY=5.1 StartZ=0 EndX=5.4 EndY=5.1 EndZ=0
  constraints (11):
    c: Coincident(g0,g1)
    c: Coincident(g1,g2)
    c: Coincident(g2,g3)
    c: Coincident(g3,g0)
    c: Vertical(g0)
    c: Vertical(g2)
    c: Horizontal(g1)
    c: Horizontal(g3)
    c: Distance(g0,g2) = 1.6
    c: Distance(g1,g3) = 1.2
    c: Coincident(g2,g-3)
FEATURE [Sketcher::SketchObject] Sketch064  label="rampini_per_serraggio_struttura"
  ArcFitTolerance = 1e-06
  AttachmentSupport = -> [XZ_Plane002]
  ExternalGeometry = -> [Sketch066,Sketch045]
  FullyConstrained = true
  MakeInternals = false
  MapMode = 5
  Placement = pos=(0,0,0) rot=(1,0,0;1.5708rad)
  sketch-geometry (7):
    g0: LineSegment StartX=7 StartY=5.1 StartZ=0 EndX=7 EndY=3.9 EndZ=0
    g1: LineSegment StartX=7 StartY=3.9 StartZ=0 EndX=9 EndY=3.9 EndZ=0
    g2: LineSegment StartX=7 StartY=5.1 StartZ=0 EndX=7 EndY=5.1 EndZ=0
    g3: LineSegment StartX=7 StartY=5.1 StartZ=0 EndX=7 EndY=7.5 EndZ=0
    g4: LineSegment StartX=9 StartY=5.1 StartZ=0 EndX=9 EndY=3.9 EndZ=0
    g5: LineSegment StartX=7 StartY=7.5 StartZ=0 EndX=9 EndY=7.5 EndZ=0
    g6: LineSegment StartX=9 StartY=7.5 StartZ=0 EndX=9 EndY=5.1 EndZ=0
  constraints (20):
    c: Vertical(g0)
    c: Coincident(g1,g0)
    c: Horizontal(g1)
    c: Coincident(g2,g0)
    c: Horizontal(g2)
    c: Coincident(g3,g2)
    c: Vertical(g3)
    c: Coincident(g5,g3)
    c: Coincident(g4,g6)
    c: Coincident(g4,g1)
    c: Vertical(g4)
    c: Coincident(g0,g-3)
    c: DistanceY(g-4,g3) = 2.4
    c: DistanceX(g1,g1) = 2
    c: DistanceY(g2,g6) = 0
    c: DistanceX(g2,g2) = 0
    c: DistanceY(g0,g0) = 1.2
    c: Coincident(g5,g6)
    c: Horizontal(g5)
    c: Vertical(g6)
FEATURE [Part::Extrusion] Extrude070  label="Extrude piano per rampino"
  Base = -> Sketch066
  Dir = (0,-1,2e-16)
  DirMode = 2
  FaceMakerClass = Part::FaceMakerBullseye
  FaceMakerMode = 3
  LengthFwd = 17
  LengthRev = 0
  Solid = true
  Symmetric = true
FEATURE [Part::Extrusion] Extrude071  label="Extrude rampini_per_serraggio_struttura"
  Base = -> Sketch064
  Dir = (0,-1,2e-16)
  DirMode = 2
  FaceMakerClass = Part::FaceMakerBullseye
  FaceMakerMode = 3
  LengthFwd = 5
  LengthRev = 0
  Solid = true
  Symmetric = true
FEATURE [Part::MultiFuse] Fusion003  label="Fusion supporto neopixel completo"
  Refine = true
  Shapes = -> [Fusion001,Extrude070,Extrude071]
FEATURE [Sketcher::SketchObject] Sketch067  label="perno per blocco switch"
  ArcFitTolerance = 1e-06
  AttachmentSupport = -> [XZ_Plane]
  ExternalGeometry = -> [Sketch,Sketch010]
  FullyConstrained = true
  MakeInternals = false
  MapMode = 5
  Placement = pos=(0,0,0) rot=(1,0,0;1.5708rad)
  sketch-geometry (14):
    g0: LineSegment StartX=-191.073 StartY=24.9429 StartZ=0 EndX=-185.81 EndY=23.0276 EndZ=0
    g1: LineSegment StartX=-183.76 StartY=23.9839 StartZ=0 EndX=-182.392 EndY=27.7427 EndZ=0
    g2: LineSegment StartX=-183.348 StartY=29.7934 StartZ=0 EndX=-188.61 EndY=31.7087 EndZ=0
    g3: LineSegment StartX=-188.61 StartY=31.7087 StartZ=0 EndX=-191.073 EndY=24.9429 EndZ=0
    g4: GeomPoint [constr] X=-186.459 Y=27.0946 Z=0
    g5: LineSegment StartX=-189.022 StartY=25.8992 StartZ=0 EndX=-185.263 EndY=24.5311 EndZ=0
    g6: LineSegment StartX=-185.263 StartY=24.5311 StartZ=0 EndX=-183.895 EndY=28.2899 EndZ=0
    g7: LineSegment StartX=-183.895 StartY=28.2899 StartZ=0 EndX=-187.654 EndY=29.658 EndZ=0
    g8: LineSegment StartX=-187.654 StartY=29.658 StartZ=0 EndX=-189.022 EndY=25.8992 EndZ=0
    g9: GeomPoint [constr] X=-186.459 Y=27.0946 Z=0
    g10: ArcOfCircle CenterX=-185.263 CenterY=24.5311 CenterZ=0 NormalX=0 NormalY=0 NormalZ=1 AngleXU=0 Radius=1.6 StartAngle=4.36332 EndAngle=5.93412
    g11: GeomPoint [constr] X=-184.307 Y=22.4804 Z=0
    g12: ArcOfCircle CenterX=-183.895 CenterY=28.2899 CenterZ=0 NormalX=0 NormalY=0 NormalZ=1 AngleXU=0 Radius=1.6 StartAngle=5.93412 EndAngle=7.50492
    g13: GeomPoint [constr] X=-181.844 Y=29.2462 Z=0
  constraints (30):
    c: Coincident(g2,g3)
    c: Coincident(g3,g0)
    c: Symmetric(g13,g0,g4)
    c: Distance(g11,g3) = 7.2
    c: Distance(g0,g2) = 7.2
    c: Parallel(g3,g1)
    c: Parallel(g2,g0)
    c: Perpendicular(g2,g3)
    c: Coincident(g5,g6)
    c: Coincident(g6,g7)
    c: Coincident(g7,g8)
    c: Coincident(g8,g5)
    c: Symmetric(g7,g5,g9)
    c: Distance(g6,g8) = 4
    c: Distance(g5,g7) = 4
    c: Coincident(g9,g4)
    c: Parallel(g8,g6)
    c: Parallel(g7,g5)
    c: Perpendicular(g7,g8)
    c: Tangent(g8,g-3)
    c: Tangent(g2,g-4)
    c: PointOnObject(g11,g1)
    c: PointOnObject(g11,g0)
    c: Tangent(g1,g10) = -1.5708
    c: Tangent(g0,g10) = -1.5708
    c: PointOnObject(g13,g1)
    c: Tangent(g1,g12) = -1.5708
    c: Tangent(g2,g12) = -1.5708
    c: Equal(g10,g12)
    c: Coincident(g10,g5)
FEATURE [Part::Extrusion] Extrude072  label="Extrude perno per blocco switch"
  Base = -> Sketch067
  Dir = (0,-1,2e-16)
  DirMode = 2
  FaceMakerClass = Part::FaceMakerBullseye
  FaceMakerMode = 3
  LengthFwd = 25.2
  LengthRev = 0
  Solid = true
  Symmetric = true
FEATURE [Part::MultiFuse] Fusion
  Refine = true
  Shapes = -> [Extrude,Sweep,Extrude007,Extrude011,Extrude005,Extrude012,Extrude013,Extrude016,Extrude031,Extrude039,Extrude045,Extrude072]
FEATURE [Part::Cut] Cut
  Base = -> Fusion
  Refine = true
  Tool = -> Extrude001
FEATURE [Part::Cut] Cut001
  Base = -> Cut
  Refine = true
  Tool = -> Extrude004
FEATURE [Part::Cut] Cut002
  Base = -> Cut001
  Refine = true
  Tool = -> Extrude006
FEATURE [Part::Cut] Cut003
  Base = -> Cut002
  Refine = true
  Tool = -> Extrude008
FEATURE [Part::Cut] Cut004
  Base = -> Cut003
  Refine = true
  Tool = -> Extrude009
FEATURE [Part::Cut] Cut005
  Base = -> Cut004
  Refine = true
  Tool = -> Extrude010
FEATURE [Part::Cut] Cut006
  Base = -> Cut005
  Refine = true
  Tool = -> Extrude014
FEATURE [Part::Cut] Cut007
  Base = -> Cut006
  Refine = true
  Tool = -> Extrude015
FEATURE [Part::Cut] Cut008
  Base = -> Cut007
  Refine = true
  Tool = -> Extrude018
FEATURE [Part::Cut] Cut009
  Base = -> Cut008
  Refine = true
  Tool = -> Extrude019
FEATURE [Part::Cut] Cut010
  Base = -> Cut009
  Refine = true
  Tool = -> Extrude020
FEATURE [Part::Cut] Cut011
  Base = -> Cut010
  Refine = true
  Tool = -> Extrude021
FEATURE [Part::Cut] Cut012
  Base = -> Cut011
  Refine = true
  Tool = -> Extrude022
FEATURE [Part::Cut] Cut013
  Base = -> Cut012
  Refine = true
  Tool = -> Extrude023
FEATURE [Part::Cut] Cut014
  Base = -> Cut013
  Refine = true
  Tool = -> Extrude032
FEATURE [Part::Cut] Cut015
  Base = -> Cut014
  Refine = true
  Tool = -> Extrude033
FEATURE [Part::Cut] Cut016
  Base = -> Cut015
  Refine = true
  Tool = -> Extrude034
FEATURE [Part::Cut] Cut017
  Base = -> Cut016
  Refine = true
  Tool = -> Extrude035
FEATURE [Part::Cut] Cut018
  Base = -> Cut017
  Refine = true
  Tool = -> Extrude036
FEATURE [Part::Cut] Cut019
  Base = -> Cut018
  Refine = true
  Tool = -> Extrude037
FEATURE [Part::Cut] Cut020
  Base = -> Cut019
  Refine = true
  Tool = -> Extrude030
FEATURE [Part::Cut] Cut022
  Base = -> Cut020
  Refine = true
  Tool = -> Extrude038
FEATURE [Part::Cut] Cut023
  Base = -> Cut022
  Refine = true
  Tool = -> Extrude041
FEATURE [Part::Cut] Cut024
  Base = -> Cut023
  Refine = true
  Tool = -> Extrude040
FEATURE [Part::Cut] Cut025
  Base = -> Cut024
  Refine = true
  Tool = -> Extrude042
FEATURE [Part::Cut] Cut026
  Base = -> Cut025
  Refine = true
  Tool = -> Extrude043
FEATURE [Part::Cut] Cut027
  Base = -> Cut026
  Refine = true
  Tool = -> Extrude044
FEATURE [Part::Cut] Cut028
  Base = -> Cut027
  Refine = true
  Tool = -> Extrude046
FEATURE [Part::Cut] Cut029
  Base = -> Cut028
  Refine = true
  Tool = -> Extrude047
FEATURE [Part::Cut] Cut033
  Base = -> Cut029
  Refine = true
  Tool = -> Extrude055
FEATURE [Part::Cut] Cut034
  Base = -> Cut033
  Refine = true
  Tool = -> Extrude056
FEATURE [Part::Cut] Cut035
  Base = -> Cut034
  Refine = true
  Tool = -> Extrude057
FEATURE [Part::Cut] Cut037
  Base = -> Cut035
  Refine = true
  Tool = -> Extrude060
FEATURE [Part::Cut] Cut038
  Base = -> Cut037
  Refine = true
  Tool = -> Extrude061
FEATURE [Part::Cut] Cut039
  Base = -> Cut038
  Refine = true
  Tool = -> Extrude063
FEATURE [Part::Cut] Cut040
  Base = -> Cut039
  Refine = true
  Tool = -> Extrude064
FEATURE [Part::Cut] Cut041
  Base = -> Cut040
  Refine = true
  Tool = -> Extrude062
FEATURE [Sketcher::SketchObject] Sketch068  label="base con smusso sopra neopixel"
  ArcFitTolerance = 1e-06
  AttachmentSupport = -> [YZ_Plane002]
  FullyConstrained = true
  MakeInternals = false
  MapMode = 5
  Placement = pos=(0,0,0) rot=(0.57735,0.57735,0.57735;2.0944rad)
  sketch-geometry (5):
    g0: LineSegment StartX=-9.5 StartY=-6.1 StartZ=0 EndX=9.5 EndY=-6.1 EndZ=0
    g1: LineSegment StartX=9.5 StartY=-6.1 StartZ=0 EndX=9.5 EndY=6.1 EndZ=0
    g2: LineSegment StartX=9.5 StartY=6.1 StartZ=0 EndX=-9.5 EndY=6.1 EndZ=0
    g3: LineSegment StartX=-9.5 StartY=6.1 StartZ=0 EndX=-9.5 EndY=-6.1 EndZ=0
    g4: GeomPoint [constr] X=0 Y=0 Z=0
  constraints (12):
    c: Coincident(g0,g1)
    c: Coincident(g1,g2)
    c: Coincident(g2,g3)
    c: Coincident(g3,g0)
    c: Horizontal(g0)
    c: Horizontal(g2)
    c: Vertical(g1)
    c: Vertical(g3)
    c: Symmetric(g2,g0,g4)
    c: Distance(g1,g3) = 19
    c: Distance(g0,g2) = 12.2
    c: Coincident(g4,g-1)
FEATURE [PartDesign::Body] Body002  label="supporto per neopixel"
  AllowCompound = false
  Group = -> [Sketch045,Sketch046,Sketch047,Sketch048,Sketch049,Sketch064,Sketch066,Sketch068]
  Origin = -> Origin002
FEATURE [Part::Extrusion] Extrude073  label="Extrude base con smusso sopra neopixel"
  Base = -> Sketch068
  Dir = (1,0,0)
  DirMode = 2
  FaceMakerClass = Part::FaceMakerBullseye
  FaceMakerMode = 3
  LengthFwd = -1
  LengthRev = 0
  Solid = true
  Symmetric = false
FEATURE [Part::Chamfer] Chamfer  label="Chamfer frontale supporto neopixel da fondere al supporto"
  Base = -> Extrude073
  EdgeLinks = -> Extrude073 [Edge4,Edge7,Edge10,Edge12]
  Edges = 4 edges r=0.5: [Edge4,Edge7,Edge10,Edge12]
FEATURE [Sketcher::SketchObject] Sketch069  label="cilindro minore"
  ArcFitTolerance = 1e-06
  AttachmentSupport = -> [XZ_Plane004]
  FullyConstrained = true
  MakeInternals = false
  MapMode = 5
  Placement = pos=(0,0,0) rot=(1,0,0;1.5708rad)
  sketch-geometry (1):
    g0: Circle CenterX=0 CenterY=0 CenterZ=0 NormalX=0 NormalY=0 NormalZ=1 AngleXU=0 Radius=5.8
  constraints (2):
    c: Diameter(g0) = 11.6
    c: Coincident(g0,g-1)
FEATURE [Sketcher::SketchObject] Sketch070  label="cilindro maggiore"
  ArcFitTolerance = 1e-06
  AttachmentSupport = -> [XZ_Plane004]
  ExternalGeometry = -> [Sketch069]
  FullyConstrained = true
  MakeInternals = false
  MapMode = 5
  Placement = pos=(0,0,0) rot=(1,0,0;1.5708rad)
  sketch-geometry (1):
    g0: Circle CenterX=0 CenterY=0 CenterZ=0 NormalX=0 NormalY=0 NormalZ=1 AngleXU=0 Radius=6.5
  constraints (2):
    c: Coincident(g0,g-1)
    c: Diameter(g0) = 13
FEATURE [Sketcher::SketchObject] Sketch071  label="buco interno"
  ArcFitTolerance = 1e-06
  AttachmentSupport = -> [XZ_Plane004]
  ExternalGeometry = -> [Sketch069]
  FullyConstrained = true
  MakeInternals = false
  MapMode = 5
  Placement = pos=(0,0,0) rot=(1,0,0;1.5708rad)
  sketch-geometry (1):
    g0: Circle CenterX=0 CenterY=0 CenterZ=0 NormalX=0 NormalY=0 NormalZ=1 AngleXU=0 Radius=5
  constraints (2):
    c: Coincident(g0,g-1)
    c: Diameter(g0) = 10
FEATURE [PartDesign::Pad] Pad
  Direction = (0,-1,2e-16)
  Length = 1.2
  Length2 = 10
  Placement = pos=(0,0,0) rot=(1,0,0;1.5708rad)
  Profile = -> Sketch070
  ReferenceAxis = -> Sketch070 [N_Axis]
  Refine = true
  Suppressed = false
  Type = 0
FEATURE [PartDesign::Pad] Pad001
  BaseFeature = -> Pad
  Direction = (0,-1,2e-16)
  Length = 5.6
  Length2 = 10
  Placement = pos=(0,0,0) rot=(1,0,0;1.5708rad)
  Profile = -> Sketch069
  ReferenceAxis = -> Sketch069 [N_Axis]
  Refine = true
  Suppressed = false
  Type = 0
FEATURE [PartDesign::Pocket] Pocket
  BaseFeature = -> Pad001
  Direction = (0,1,-2e-16)
  Length = 7
  Length2 = 5
  Midplane = true
  Placement = pos=(0,0,0) rot=(1,0,0;1.5708rad)
  Profile = -> Sketch071
  ReferenceAxis = -> Sketch071 [N_Axis]
  Refine = true
  Suppressed = false
  Type = 0
FEATURE [PartDesign::Fillet] Fillet
  Base = -> Pocket [Face7]
  BaseFeature = -> Pocket
  Placement = pos=(0,0,0) rot=(1,0,0;1.5708rad)
  Radius = 1
  Refine = true
  SupportTransform = false
  Suppressed = false
  UseAllEdges = false
FEATURE [PartDesign::Body] Body004  label="pulsanti lato sinistro"
  AllowCompound = false
  Group = -> [Sketch069,Sketch070,Sketch071,Pad,Pad001,Pocket,Fillet]
  Origin = -> Origin004
  Tip = -> Fillet
FEATURE [Sketcher::SketchObject] Sketch072  label="buco per saldature e diodo driver solenoide"
  ArcFitTolerance = 1e-06
  AttachmentSupport = -> [XZ_Plane]
  ExternalGeometry = -> [Sketch038]
  FullyConstrained = true
  MakeInternals = false
  MapMode = 5
  Placement = pos=(0,0,0) rot=(1,0,0;1.5708rad)
  sketch-geometry (4):
    g0: LineSegment StartX=-209.225 StartY=-40.6939 StartZ=0 EndX=-204.154 EndY=-29.8182 EndZ=0
    g1: LineSegment StartX=-204.154 StartY=-29.8182 StartZ=0 EndX=-206.51 EndY=-28.7194 EndZ=0
    g2: LineSegment StartX=-206.51 StartY=-28.7194 StartZ=0 EndX=-211.582 EndY=-39.5951 EndZ=0
    g3: LineSegment StartX=-211.582 StartY=-39.5951 StartZ=0 EndX=-209.225 EndY=-40.6939 EndZ=0
  constraints (11):
    c: Coincident(g1,g0)
    c: Coincident(g2,g1)
    c: Coincident(g3,g2)
    c: Coincident(g3,g0)
    c: Parallel(g-3,g0)
    c: Parallel(g0,g2)
    c: Perpendicular(g0,g3)
    c: Perpendicular(g1,g0)
    c: Distance(g3) = 2.6
    c: Distance(g2) = 12
    c: Coincident(g0,g-3)
FEATURE [Part::Extrusion] Extrude074  label="Extrude buco per saldature e diodo driver solenoide"
  Base = -> Sketch072
  Dir = (0,-1,2e-16)
  DirMode = 2
  FaceMakerClass = Part::FaceMakerBullseye
  FaceMakerMode = 3
  LengthFwd = 14.6
  LengthRev = 0
  Solid = true
  Symmetric = true
FEATURE [Part::Cut] Cut042
  Base = -> Cut041
  Refine = true
  Tool = -> Extrude074
FEATURE [Sketcher::SketchObject] Sketch073  label="fori slargati blocco solenoide"
  ArcFitTolerance = 1e-06
  AttachmentSupport = -> [XY_Plane]
  ExternalGeometry = -> [Sketch030]
  FullyConstrained = true
  MakeInternals = false
  MapMode = 5
  sketch-geometry (2):
    g0: Circle CenterX=-152.209 CenterY=6.95 CenterZ=0 NormalX=0 NormalY=0 NormalZ=1 AngleXU=0 Radius=3.7
    g1: Circle CenterX=-130.41 CenterY=-6.95 CenterZ=0 NormalX=0 NormalY=0 NormalZ=1 AngleXU=0 Radius=3.7
  constraints (4):
    c: Diameter(g0) = 7.4
    c: Coincident(g0,g-3)
    c: Diameter(g1) = 7.4
    c: Coincident(g1,g-4)
FEATURE [Part::Extrusion] Extrude075  label="Extrude fori slargati blocco solenoide"
  Base = -> Sketch073
  Dir = (0,0,1)
  DirMode = 2
  FaceMakerClass = Part::FaceMakerBullseye
  FaceMakerMode = 3
  LengthFwd = 1.5
  LengthRev = 0
  Placement = pos=(0,0,36.4) rot=(0,0,1;0rad)
  Solid = true
  Symmetric = false
FEATURE [Part::Cut] Cut043
  Base = -> Cut042
  Refine = true
  Tool = -> Extrude075
FEATURE [Sketcher::SketchObject] Sketch074  label="lato sx pistola"
  ArcFitTolerance = 1e-06
  AttachmentSupport = -> [XZ_Plane]
  ExternalGeometry = -> [Sketch016,Sketch,Sketch058]
  FullyConstrained = true
  MakeInternals = false
  MapMode = 5
  Placement = pos=(0,0,0) rot=(1,0,0;1.5708rad)
  sketch-geometry (37):
    g0: LineSegment StartX=-82.8 StartY=3.2 StartZ=0 EndX=0 EndY=3.2 EndZ=0
    g1: LineSegment StartX=-82.8 StartY=3.2 StartZ=0 EndX=-82.8 EndY=6.2 EndZ=0
    g2: LineSegment [constr] StartX=-107.6 StartY=18 StartZ=0 EndX=-107.6 EndY=20 EndZ=0
    g3: LineSegment [constr] StartX=-132.428 StartY=18 StartZ=0 EndX=-132.428 EndY=20 EndZ=0
    g4: LineSegment StartX=-132.428 StartY=20 StartZ=0 EndX=-107.6 EndY=20 EndZ=0
    g5: ArcOfCircle CenterX=-107.6 CenterY=4 CenterZ=0 NormalX=0 NormalY=0 NormalZ=1 AngleXU=0 Radius=16 StartAngle=0.137937 EndAngle=1.5708
    g6: LineSegment StartX=-82.8 StartY=6.2 StartZ=0 EndX=-91.752 EndY=6.2 EndZ=0
    g7: LineSegment [constr] StartX=-145.743 StartY=8.32624 StartZ=0 EndX=-147.645 EndY=8.94427 EndZ=0
    g8: ArcOfCircle CenterX=-132.428 CenterY=4 CenterZ=0 NormalX=0 NormalY=0 NormalZ=1 AngleXU=0 Radius=16 StartAngle=1.5708 EndAngle=2.82743
    g9: LineSegment StartX=-215.932 StartY=-80.4316 StartZ=0 EndX=-176.685 EndY=-80.4316 EndZ=0
    g10: LineSegment StartX=-147.645 StartY=8.94427 StartZ=0 EndX=-176.685 EndY=-80.4316 EndZ=0
    g11: LineSegment [constr] StartX=-193.988 StartY=-2.33927 StartZ=0 EndX=-192.176 EndY=-3.18451 EndZ=0
    g12: LineSegment [constr] StartX=-217.232 StartY=-52.1862 StartZ=0 EndX=-215.42 EndY=-53.0314 EndZ=0
    g13: LineSegment StartX=-192.176 StartY=-3.18451 StartZ=0 EndX=-215.42 EndY=-53.0314 EndZ=0
    g14: ArcOfCircle CenterX=-184.801 CenterY=-67.3089 CenterZ=0 NormalX=0 NormalY=0 NormalZ=1 AngleXU=0 Radius=33.7833 StartAngle=2.70526 EndAngle=3.54053
    g15: ArcOfCircle CenterX=-207.583 CenterY=4 CenterZ=0 NormalX=0 NormalY=0 NormalZ=1 AngleXU=0 Radius=17 StartAngle=5.84685 EndAngle=7.56663
    g16: LineSegment StartX=-202.765 StartY=20.303 StartZ=0 EndX=-195.887 EndY=39.2 EndZ=0
    g17: LineSegment [constr] StartX=-193.885 StartY=33.0037 StartZ=0 EndX=-197.644 EndY=34.3718 EndZ=0
    g18: LineSegment StartX=-195.887 StartY=39.2 StartZ=0 EndX=0 EndY=39.2 EndZ=0
    g19: LineSegment StartX=0 StartY=3.2 StartZ=0 EndX=0 EndY=39.2 EndZ=0
    g20: LineSegment StartX=-189.939 StartY=31.5672 StartZ=0 EndX=-192.333 EndY=24.9893 EndZ=0
    g21: LineSegment StartX=-196.467 StartY=26.4942 StartZ=0 EndX=-194.073 EndY=33.0721 EndZ=0
    g22: Circle CenterX=-213.443 CenterY=-76.8316 CenterZ=0 NormalX=0 NormalY=0 NormalZ=1 AngleXU=0 Radius=1.8
    g23: Circle CenterX=-179.305 CenterY=-76.8316 CenterZ=0 NormalX=0 NormalY=0 NormalZ=1 AngleXU=0 Radius=1.8
    g24: Circle CenterX=-184.08 CenterY=34.8 CenterZ=0 NormalX=0 NormalY=0 NormalZ=1 AngleXU=0 Radius=1.8
    g25: Circle CenterX=-78.51 CenterY=34.8 CenterZ=0 NormalX=0 NormalY=0 NormalZ=1 AngleXU=0 Radius=1.8
    g26: Circle CenterX=-78.51 CenterY=7.6 CenterZ=0 NormalX=0 NormalY=0 NormalZ=1 AngleXU=0 Radius=1.8
    g27: Circle CenterX=-5.6 CenterY=34.8 CenterZ=0 NormalX=0 NormalY=0 NormalZ=1 AngleXU=0 Radius=1.8
    g28: Circle CenterX=-5.6 CenterY=7.6 CenterZ=0 NormalX=0 NormalY=0 NormalZ=1 AngleXU=0 Radius=1.8
    g29: LineSegment StartX=-190.127 StartY=31.6356 StartZ=0 EndX=-189.939 EndY=31.5672 EndZ=0
    g30: LineSegment StartX=-194.073 StartY=33.0721 StartZ=0 EndX=-193.885 EndY=33.0037 EndZ=0
    g31: LineSegment StartX=-193.885 StartY=33.0037 StartZ=0 EndX=-190.127 EndY=31.6356 EndZ=0
    g32: LineSegment StartX=-196.467 StartY=26.4942 StartZ=0 EndX=-192.333 EndY=24.9893 EndZ=0
    g33: Circle CenterX=-19 CenterY=21.2 CenterZ=0 NormalX=0 NormalY=0 NormalZ=1 AngleXU=0 Radius=6.3
    g34: Circle CenterX=-42 CenterY=21.2 CenterZ=0 NormalX=0 NormalY=0 NormalZ=1 AngleXU=0 Radius=6.3
    g35: Circle CenterX=-65 CenterY=21.2 CenterZ=0 NormalX=0 NormalY=0 NormalZ=1 AngleXU=0 Radius=6.3
    g36: LineSegment [constr] StartX=-4 StartY=21.2 StartZ=0 EndX=-65 EndY=21.2 EndZ=0
  constraints (96):
    c: Coincident(g0,g-41)
    c: Horizontal(g0)
    c: PointOnObject(g0,g-39)
    c: Coincident(g1,g0)
    c: Vertical(g1)
    c: DistanceY(g1,g1) = 3
    c: Coincident(g2,g-17)
    c: Vertical(g2)
    c: Coincident(g3,g-16)
    c: Vertical(g3)
    c: DistanceY(g2,g2) = 2
    c: DistanceY(g3,g3) = 2
    c: Coincident(g4,g3)
    c: Coincident(g4,g2)
    c: Coincident(g5,g-17)
    c: Coincident(g5,g2)
    c: Coincident(g6,g1)
    c: Horizontal(g6)
    c: Coincident(g6,g5)
    c: Coincident(g7,g-15)
    c: Coincident(g8,g7)
    c: Coincident(g8,g3)
    c: Coincident(g8,g-15)
    c: Horizontal(g9)
    c: DistanceY(g-13,g9) = 2
    c: Coincident(g10,g7)
    c: Parallel(g10,g-14)
    c: Coincident(g9,g10)
    c: Distance(g11) = 2
    c: Coincident(g11,g-11)
    c: Perpendicular(g-11,g11)
    c: Distance(g12) = 2
    c: Coincident(g12,g-12)
    c: Perpendicular(g-11,g12)
    c: Coincident(g13,g11)
    c: Coincident(g13,g12)
    c: Coincident(g14,g-32)
    c: Coincident(g14,g12)
    c: Coincident(g14,g9)
    c: Coincident(g15,g-10)
    c: Coincident(g15,g11)
    c: Parallel(g16,g-22)
    c: Distance(g17) = 4
    c: PointOnObject(g17,g16)
    c: Coincident(g15,g16)
    c: Horizontal(g18)
    c: Coincident(g18,g16)
    c: Coincident(g19,g0)
    c: PointOnObject(g19,g-39)
    c: DistanceY(g19,g-36) = 2
    c: Coincident(g18,g19)
    c: Diameter(g22) = 3.6
    c: Coincident(g22,g-9)
    c: Diameter(g23) = 3.6
    c: Coincident(g23,g-8)
    c: Diameter(g24) = 3.6
    c: Diameter(g25) = 3.6
    c: Diameter(g26) = 3.6
    c: Diameter(g27) = 3.6
    c: Diameter(g28) = 3.6
    c: Coincident(g27,g-4)
    c: Coincident(g28,g-3)
    c: Coincident(g25,g-6)
    c: Coincident(g26,g-5)
    c: Coincident(g24,g-7)
    c: Parallel(g20,g-21)
    c: Equal(g20,g-21)
    c: Parallel(g21,g-19)
    c: Equal(g21,g-19)
    c: Distance(g29) = 0.2
    c: Distance(g30) = 0.2
    c: Parallel(g29,g-20)
    c: Parallel(g31,g-20)
    c: Equal(g31,g-20)
    c: Coincident(g30,g31)
    c: Coincident(g31,g29)
    c: Coincident(g29,g-21)
    c: Parallel(g30,g31)
    c: Coincident(g17,g30)
    c: Coincident(g20,g29)
    c: Coincident(g21,g30)
    c: Perpendicular(g16,g17)
    c: Coincident(g32,g21)
    c: Coincident(g32,g20)
    c: Perpendicular(g10,g7)
    c: Diameter(g33) = 12.6
    c: Diameter(g34) = 12.6
    c: Diameter(g35) = 12.6
    c: Horizontal(g36)
    c: PointOnObject(g33,g36)
    c: PointOnObject(g34,g36)
    c: DistanceX(g34,g33) = 23
    c: DistanceX(g35,g34) = 23
    c: DistanceX(g33,g36) = 15
    c: Symmetric(g-24,g-24,g36)
    c: Coincident(g36,g35)
FEATURE [Sketcher::SketchObject] Sketch075  label="lato dx pistola"
  ArcFitTolerance = 1e-06
  AttachmentSupport = -> [XZ_Plane]
  ExternalGeometry = -> [Sketch016,Sketch,Sketch058,Sketch074]
  FullyConstrained = true
  MakeInternals = false
  MapMode = 5
  Placement = pos=(0,0,0) rot=(1,0,0;1.5708rad)
  sketch-geometry (61):
    g0: LineSegment StartX=-82.8 StartY=3.2 StartZ=0 EndX=0 EndY=3.2 EndZ=0
    g1: LineSegment StartX=-82.8 StartY=3.2 StartZ=0 EndX=-82.8 EndY=6.2 EndZ=0
    g2: LineSegment [constr] StartX=-107.6 StartY=18 StartZ=0 EndX=-107.6 EndY=20 EndZ=0
    g3: LineSegment [constr] StartX=-132.428 StartY=18 StartZ=0 EndX=-132.428 EndY=20 EndZ=0
    g4: LineSegment StartX=-132.428 StartY=20 StartZ=0 EndX=-107.6 EndY=20 EndZ=0
    g5: ArcOfCircle CenterX=-107.6 CenterY=4 CenterZ=0 NormalX=0 NormalY=0 NormalZ=1 AngleXU=0 Radius=16 StartAngle=0.137937 EndAngle=1.5708
    g6: LineSegment StartX=-82.8 StartY=6.2 StartZ=0 EndX=-91.752 EndY=6.2 EndZ=0
    g7: LineSegment [constr] StartX=-145.743 StartY=8.32624 StartZ=0 EndX=-147.645 EndY=8.94427 EndZ=0
    g8: ArcOfCircle CenterX=-132.428 CenterY=4 CenterZ=0 NormalX=0 NormalY=0 NormalZ=1 AngleXU=0 Radius=16 StartAngle=1.5708 EndAngle=2.82743
    g9: LineSegment StartX=-215.932 StartY=-80.4316 StartZ=0 EndX=-176.685 EndY=-80.4316 EndZ=0
    g10: LineSegment StartX=-147.645 StartY=8.94427 StartZ=0 EndX=-176.685 EndY=-80.4316 EndZ=0
    g11: LineSegment [constr] StartX=-193.988 StartY=-2.33927 StartZ=0 EndX=-192.176 EndY=-3.18451 EndZ=0
    g12: LineSegment [constr] StartX=-217.232 StartY=-52.1862 StartZ=0 EndX=-215.42 EndY=-53.0314 EndZ=0
    g13: LineSegment StartX=-192.176 StartY=-3.18451 StartZ=0 EndX=-215.42 EndY=-53.0314 EndZ=0
    g14: ArcOfCircle CenterX=-184.801 CenterY=-67.3089 CenterZ=0 NormalX=0 NormalY=0 NormalZ=1 AngleXU=0 Radius=33.7833 StartAngle=2.70526 EndAngle=3.54053
    g15: ArcOfCircle CenterX=-207.583 CenterY=4 CenterZ=0 NormalX=0 NormalY=0 NormalZ=1 AngleXU=0 Radius=17 StartAngle=5.84685 EndAngle=7.56663
    g16: LineSegment StartX=-202.765 StartY=20.303 StartZ=0 EndX=-195.887 EndY=39.2 EndZ=0
    g17: LineSegment [constr] StartX=-193.885 StartY=33.0037 StartZ=0 EndX=-197.644 EndY=34.3718 EndZ=0
    g18: LineSegment StartX=-195.887 StartY=39.2 StartZ=0 EndX=0 EndY=39.2 EndZ=0
    g19: LineSegment StartX=0 StartY=3.2 StartZ=0 EndX=0 EndY=39.2 EndZ=0
    g20: LineSegment StartX=-189.939 StartY=31.5672 StartZ=0 EndX=-192.333 EndY=24.9893 EndZ=0
    g21: LineSegment StartX=-196.467 StartY=26.4942 StartZ=0 EndX=-194.073 EndY=33.0721 EndZ=0
    g22: Circle CenterX=-213.443 CenterY=-76.8316 CenterZ=0 NormalX=0 NormalY=0 NormalZ=1 AngleXU=0 Radius=1.8
    g23: Circle CenterX=-179.305 CenterY=-76.8316 CenterZ=0 NormalX=0 NormalY=0 NormalZ=1 AngleXU=0 Radius=1.8
    g24: Circle CenterX=-184.08 CenterY=34.8 CenterZ=0 NormalX=0 NormalY=0 NormalZ=1 AngleXU=0 Radius=1.8
    g25: Circle CenterX=-78.51 CenterY=34.8 CenterZ=0 NormalX=0 NormalY=0 NormalZ=1 AngleXU=0 Radius=1.8
    g26: Circle CenterX=-78.51 CenterY=7.6 CenterZ=0 NormalX=0 NormalY=0 NormalZ=1 AngleXU=0 Radius=1.8
    g27: Circle CenterX=-5.6 CenterY=34.8 CenterZ=0 NormalX=0 NormalY=0 NormalZ=1 AngleXU=0 Radius=1.8
    g28: Circle CenterX=-5.6 CenterY=7.6 CenterZ=0 NormalX=0 NormalY=0 NormalZ=1 AngleXU=0 Radius=1.8
    g29: LineSegment StartX=-190.127 StartY=31.6356 StartZ=0 EndX=-189.939 EndY=31.5672 EndZ=0
    g30: LineSegment StartX=-194.073 StartY=33.0721 StartZ=0 EndX=-193.885 EndY=33.0037 EndZ=0
    g31: LineSegment StartX=-193.885 StartY=33.0037 StartZ=0 EndX=-190.127 EndY=31.6356 EndZ=0
    g32: LineSegment StartX=-196.467 StartY=26.4942 StartZ=0 EndX=-192.333 EndY=24.9893 EndZ=0
    g33: LineSegment [constr] StartX=-4 StartY=21.2 StartZ=0 EndX=-87.91 EndY=21.2 EndZ=0
    g34: GeomPoint [constr] X=-4 Y=21.2 Z=0
    g35: LineSegment [constr] StartX=-15.2 StartY=33.7 StartZ=0 EndX=-15.2 EndY=8.7 EndZ=0
    g36: LineSegment [constr] StartX=-15.2 StartY=33.7 StartZ=0 EndX=-56.2 EndY=33.7 EndZ=0
    g37: LineSegment [constr] StartX=-15.2 StartY=8.7 StartZ=0 EndX=-56.2 EndY=8.7 EndZ=0
    g38: LineSegment [constr] StartX=-56.2 StartY=33.7 StartZ=0 EndX=-56.2 EndY=8.7 EndZ=0
    g39: Circle CenterX=-18.6 CenterY=30.3 CenterZ=0 NormalX=0 NormalY=0 NormalZ=1 AngleXU=0 Radius=3.4
    g40: Circle CenterX=-18.6 CenterY=12.1 CenterZ=0 NormalX=0 NormalY=0 NormalZ=1 AngleXU=0 Radius=3.4
    g41: Circle CenterX=-43.2 CenterY=30.3 CenterZ=0 NormalX=0 NormalY=0 NormalZ=1 AngleXU=0 Radius=3.4
    g42: Circle CenterX=-43.2 CenterY=12.1 CenterZ=0 NormalX=0 NormalY=0 NormalZ=1 AngleXU=0 Radius=3.4
    g43: LineSegment [constr] StartX=-4 StartY=21.2 StartZ=0 EndX=-15.2 EndY=21.2 EndZ=0
    g44: LineSegment [constr] StartX=-15.2 StartY=21.2 StartZ=0 EndX=-36.2 EndY=21.2 EndZ=0
    g45: LineSegment [constr] StartX=-41.5 StartY=16.2 StartZ=0 EndX=-30.9 EndY=16.2 EndZ=0
    g46: LineSegment [constr] StartX=-30.9 StartY=16.2 StartZ=0 EndX=-30.9 EndY=26.2 EndZ=0
    g47: LineSegment [constr] StartX=-30.9 StartY=26.2 StartZ=0 EndX=-41.5 EndY=26.2 EndZ=0
    g48: LineSegment [constr] StartX=-41.5 StartY=26.2 StartZ=0 EndX=-41.5 EndY=16.2 EndZ=0
    g49: GeomPoint [constr] X=-36.2 Y=21.2 Z=0
    g50: Circle CenterX=-36.2 CenterY=21.2 CenterZ=0 NormalX=0 NormalY=0 NormalZ=1 AngleXU=0 Radius=2.8
    g51: LineSegment [constr] StartX=-24.2 StartY=26.7 StartZ=0 EndX=-24.2 EndY=15.7 EndZ=0
    g52: Circle CenterX=-24.2 CenterY=26.7 CenterZ=0 NormalX=0 NormalY=0 NormalZ=1 AngleXU=0 Radius=3
    g53: Circle CenterX=-24.2 CenterY=15.7 CenterZ=0 NormalX=0 NormalY=0 NormalZ=1 AngleXU=0 Radius=3
    g54: GeomPoint X=-18.6 Y=30.3 Z=0
    g55: GeomPoint X=-18.6 Y=12.1 Z=0
    g56: GeomPoint X=-43.2 Y=12.1 Z=0
    g57: GeomPoint X=-43.2 Y=30.3 Z=0
    g58: Circle CenterX=-65 CenterY=21.2 CenterZ=0 NormalX=0 NormalY=0 NormalZ=1 AngleXU=0 Radius=1.5
    g59: Circle CenterX=-42 CenterY=21.2 CenterZ=0 NormalX=0 NormalY=0 NormalZ=1 AngleXU=0 Radius=1.5
    g60: Circle CenterX=-19 CenterY=21.2 CenterZ=0 NormalX=0 NormalY=0 NormalZ=1 AngleXU=0 Radius=1.5
  constraints (149):
    c: Coincident(g0,g-41)
    c: Horizontal(g0)
    c: PointOnObject(g0,g-39)
    c: Coincident(g1,g0)
    c: Vertical(g1)
    c: DistanceY(g1,g1) = 3
    c: Coincident(g2,g-17)
    c: Vertical(g2)
    c: Coincident(g3,g-16)
    c: Vertical(g3)
    c: DistanceY(g2,g2) = 2
    c: DistanceY(g3,g3) = 2
    c: Coincident(g4,g3)
    c: Coincident(g4,g2)
    c: Coincident(g5,g-17)
    c: Coincident(g5,g2)
    c: Coincident(g6,g1)
    c: Horizontal(g6)
    c: Coincident(g6,g5)
    c: Coincident(g7,g-15)
    c: Coincident(g8,g7)
    c: Coincident(g8,g3)
    c: Coincident(g8,g-15)
    c: Horizontal(g9)
    c: DistanceY(g-13,g9) = 2
    c: Coincident(g10,g7)
    c: Parallel(g10,g-14)
    c: Coincident(g9,g10)
    c: Distance(g11) = 2
    c: Coincident(g11,g-11)
    c: Perpendicular(g-11,g11)
    c: Distance(g12) = 2
    c: Coincident(g12,g-12)
    c: Perpendicular(g-11,g12)
    c: Coincident(g13,g11)
    c: Coincident(g13,g12)
    c: Coincident(g14,g-32)
    c: Coincident(g14,g12)
    c: Coincident(g14,g9)
    c: Coincident(g15,g-10)
    c: Coincident(g15,g11)
    c: Parallel(g16,g-22)
    c: Distance(g17) = 4
    c: PointOnObject(g17,g16)
    c: Coincident(g15,g16)
    c: Horizontal(g18)
    c: Coincident(g18,g16)
    c: Coincident(g19,g0)
    c: PointOnObject(g19,g-39)
    c: DistanceY(g19,g-36) = 2
    c: Coincident(g18,g19)
    c: Diameter(g22) = 3.6
    c: Coincident(g22,g-9)
    c: Diameter(g23) = 3.6
    c: Coincident(g23,g-8)
    c: Diameter(g24) = 3.6
    c: Diameter(g25) = 3.6
    c: Diameter(g26) = 3.6
    c: Diameter(g27) = 3.6
    c: Diameter(g28) = 3.6
    c: Coincident(g27,g-4)
    c: Coincident(g28,g-3)
    c: Coincident(g25,g-6)
    c: Coincident(g26,g-5)
    c: Coincident(g24,g-7)
    c: Parallel(g20,g-21)
    c: Equal(g20,g-21)
    c: Parallel(g21,g-19)
    c: Equal(g21,g-19)
    c: Distance(g29) = 0.2
    c: Distance(g30) = 0.2
    c: Parallel(g29,g-20)
    c: Parallel(g31,g-20)
    c: Equal(g31,g-20)
    c: Coincident(g30,g31)
    c: Coincident(g31,g29)
    c: Coincident(g29,g-21)
    c: Parallel(g30,g31)
    c: Coincident(g17,g30)
    c: Coincident(g20,g29)
    c: Coincident(g21,g30)
    c: Perpendicular(g16,g17)
    c: Coincident(g32,g21)
    c: Coincident(g32,g20)
    c: Perpendicular(g10,g7)
    c: Horizontal(g33)
    c: Symmetric(g-24,g-24,g33)
    c: PointOnObject(g33,g-28)
    c: Symmetric(g-24,g-24,g34)
    c: DistanceY(g35,g35) = 25
    c: Symmetric(g35,g35,g33)
    c: Distance(g36) = 41
    c: Coincident(g36,g35)
    c: Horizontal(g36)
    c: Coincident(g37,g35)
    c: Horizontal(g37)
    c: Coincident(g38,g36)
    c: Vertical(g38)
    c: Coincident(g37,g38)
    c: Diameter(g39) = 6.8
    c: Diameter(g40) = 6.8
    c: Tangent(g39,g36)
    c: Tangent(g40,g37)
    c: Tangent(g39,g35)
    c: Tangent(g40,g35)
    c: Diameter(g41) = 6.8
    c: Diameter(g42) = 6.8
    c: Tangent(g41,g36)
    c: Tangent(g42,g37)
    c: DistanceX(g41,g39) = 24.6
    c: DistanceX(g42,g40) = 24.6
    c: Distance(g43) = 11.2
    c: Coincident(g43,g33)
    c: PointOnObject(g43,g33)
    c: PointOnObject(g43,g35)
    c: Distance(g44) = 21
    c: Coincident(g44,g43)
    c: PointOnObject(g44,g33)
    c: Coincident(g45,g46)
    c: Coincident(g46,g47)
    c: Coincident(g47,g48)
    c: Coincident(g48,g45)
    c: Horizontal(g45)
    c: Horizontal(g47)
    c: Vertical(g46)
    c: Vertical(g48)
    c: Symmetric(g47,g45,g49)
    c: Distance(g46,g48) = 10.6
    c: Distance(g45,g47) = 10
    c: Coincident(g49,g44)
    c: Diameter(g50) = 5.6
    c: Coincident(g50,g44)
    c: Distance(g51) = 11
    c: Symmetric(g51,g51,g33)
    c: DistanceX(g51,g43) = 9
    c: Diameter(g52) = 6
    c: Coincident(g52,g51)
    c: Diameter(g53) = 6
    c: Coincident(g53,g51)
    c: Coincident(g40,g55)
    c: Coincident(g39,g54)
    c: Coincident(g41,g57)
    c: Coincident(g42,g56)
    c: Diameter(g58) = 3
    c: Diameter(g59) = 3
    c: Diameter(g60) = 3
    c: Coincident(g58,g-44)
    c: Coincident(g59,g-46)
    c: Coincident(g60,g-45)
FEATURE [PartDesign::Body] Body  label="Struttura pistola"
  AllowCompound = false
  Group = -> [Sketch,Sketch002,Sketch004,DatumPlane,Sketch005,DatumPlane001,CopyCut,Sketch008,Sketch009,Sketch010,Sketch011,Sketch012,Sketch013,Sketch014,Sketch015,Sketch016,Sketch017,Sketch018,Sketch019,Sketch020,Sketch022,Sketch023,Sketch024,Sketch025,Sketch026,Sketch027,Sketch029,Sketch030,Sketch031,Sketch032,Sketch033,Sketch034,Sketch035,Sketch036,Sketch037,Sketch038,Sketch039,Sketch040,Sketch041,Sketch042,+15 more]
  Origin = -> Origin
FEATURE [Sketcher::SketchObject] Sketch078
  ArcFitTolerance = 1e-06
  AttachmentSupport = -> [XZ_Plane005]
  FullyConstrained = true
  MakeInternals = false
  MapMode = 5
  Placement = pos=(0,0,0) rot=(1,0,0;1.5708rad)
  sketch-geometry (5):
    g0: LineSegment [constr] StartX=0 StartY=5.5 StartZ=0 EndX=0 EndY=-5.5 EndZ=0
    g1: ArcOfCircle CenterX=0 CenterY=5.5 CenterZ=0 NormalX=0 NormalY=0 NormalZ=1 AngleXU=0 Radius=2.7 StartAngle=0 EndAngle=3.14159
    g2: ArcOfCircle CenterX=0 CenterY=-5.5 CenterZ=0 NormalX=0 NormalY=0 NormalZ=1 AngleXU=0 Radius=2.7 StartAngle=3.1416 EndAngle=6.28318
    g3: LineSegment StartX=-2.7 StartY=5.5 StartZ=0 EndX=-2.7 EndY=-5.50001 EndZ=0
    g4: LineSegment StartX=2.7 StartY=5.5 StartZ=0 EndX=2.7 EndY=-5.50001 EndZ=0
  constraints (13):
    c: Distance(g0) = 11
    c: Vertical(g0)
    c: Symmetric(g0,g0,g-1)
    c: Radius(g1) = 2.7
    c: Coincident(g1,g0)
    c: Radius(g2) = 2.7
    c: Coincident(g2,g0)
    c: Vertical(g3)
    c: Vertical(g4)
    c: Coincident(g2,g4)
    c: Coincident(g2,g3)
    c: Tangent(g3,g1) = -1.5708
    c: Tangent(g4,g1) = 1.5708
FEATURE [PartDesign::Pad] Pad002
  Direction = (0,-1,2e-16)
  Length = 0.8
  Length2 = 10
  Placement = pos=(0,0,0) rot=(1,0,0;1.5708rad)
  Profile = -> Sketch078
  ReferenceAxis = -> Sketch078 [N_Axis]
  Refine = true
  Suppressed = false
  Type = 0
FEATURE [Sketcher::SketchObject] Sketch079
  ArcFitTolerance = 1e-06
  AttachmentSupport = -> [XZ_Plane005]
  ExternalGeometry = -> [Sketch078]
  FullyConstrained = true
  MakeInternals = false
  MapMode = 5
  Placement = pos=(0,0,0) rot=(1,0,0;1.5708rad)
  sketch-geometry (2):
    g0: Circle CenterX=-1e-16 CenterY=5.5 CenterZ=0 NormalX=0 NormalY=0 NormalZ=1 AngleXU=0 Radius=2.7
    g1: Circle CenterX=0 CenterY=-5.5 CenterZ=0 NormalX=0 NormalY=0 NormalZ=1 AngleXU=0 Radius=2.7
  constraints (4):
    c: Coincident(g0,g-3)
    c: PointOnObject(g-3,g0)
    c: Coincident(g1,g-4)
    c: Equal(g1,g-4)
FEATURE [PartDesign::Pad] Pad003
  BaseFeature = -> Pad002
  Direction = (0,-1,2e-16)
  Length = 5
  Length2 = 10
  Placement = pos=(0,0,0) rot=(1,0,0;1.5708rad)
  Profile = -> Sketch079
  ReferenceAxis = -> Sketch079 [N_Axis]
  Refine = true
  Suppressed = false
  Type = 0
FEATURE [PartDesign::Fillet] Fillet001
  Base = -> Pad003 [Edge16,Edge14]
  BaseFeature = -> Pad003
  Placement = pos=(0,0,0) rot=(1,0,0;1.5708rad)
  Radius = 0.4
  Refine = true
  SupportTransform = false
  Suppressed = false
  UseAllEdges = false
FEATURE [PartDesign::Body] Body005  label="pulsanti lato destro"
  AllowCompound = false
  Group = -> [Sketch078,Pad002,Sketch079,Pad003,Fillet001]
  Origin = -> Origin005
  Tip = -> Fillet001
FEATURE [PartDesign::SubShapeBinder] Binder
  BindCopyOnChange = 0
  BindMode = 0
  ClaimChildren = false
  Context = -> Body006 [Binder.]
  Fuse = false
  MakeFace = true
  OffsetFill = false
  OffsetIntersection = false
  OffsetJoinType = 0
  OffsetOpenResult = false
  PartialLoad = false
  Refine = true
  Relative = true
  Support = -> [Body[Sketch074.]]
  _Version = 2
FEATURE [PartDesign::SubShapeBinder] Binder001
  BindCopyOnChange = 0
  BindMode = 0
  ClaimChildren = false
  Context = -> Body007 [Binder001.]
  Fuse = false
  MakeFace = true
  OffsetFill = false
  OffsetIntersection = false
  OffsetJoinType = 0
  OffsetOpenResult = false
  PartialLoad = false
  Refine = true
  Relative = true
  Support = -> [Body[Sketch075.]]
  _Version = 2
FEATURE [Mesh::Feature] logo_per_PCB_definitivo_positivo
  Placement = pos=(-191,17,-66) rot=(0,1,1;0rad)
FEATURE [Sketcher::SketchObject] Sketch114  label="Sketch114 - base lato DX"
  ArcFitTolerance = 1e-06
  AttachmentSupport = -> [Binder001]
  ExternalGeometry = -> [Binder001]
  FullyConstrained = true
  MakeInternals = false
  MapMode = 5
  Placement = pos=(0,1e-15,0) rot=(0,0.707107,0.707107;3.14159rad)
  sketch-geometry (30):
    g0: Circle CenterX=5.6 CenterY=34.8 CenterZ=0 NormalX=0 NormalY=0 NormalZ=1 AngleXU=0 Radius=1.8
    g1: Circle CenterX=5.6 CenterY=7.6 CenterZ=0 NormalX=0 NormalY=0 NormalZ=1 AngleXU=0 Radius=1.8
    g2: Circle CenterX=24.2 CenterY=26.7 CenterZ=0 NormalX=0 NormalY=0 NormalZ=1 AngleXU=0 Radius=3
    g3: Circle CenterX=24.2 CenterY=15.7 CenterZ=0 NormalX=0 NormalY=0 NormalZ=1 AngleXU=0 Radius=3
    g4: Circle CenterX=36.2 CenterY=21.2 CenterZ=0 NormalX=0 NormalY=0 NormalZ=1 AngleXU=0 Radius=2.8
    g5: Circle CenterX=78.51 CenterY=34.8 CenterZ=0 NormalX=0 NormalY=0 NormalZ=1 AngleXU=0 Radius=1.8
    g6: Circle CenterX=78.51 CenterY=7.6 CenterZ=0 NormalX=0 NormalY=0 NormalZ=1 AngleXU=0 Radius=1.8
    g7: Circle CenterX=184.08 CenterY=34.8 CenterZ=0 NormalX=0 NormalY=0 NormalZ=1 AngleXU=0 Radius=1.8
    g8: Circle CenterX=213.443 CenterY=-76.8316 CenterZ=0 NormalX=0 NormalY=0 NormalZ=1 AngleXU=0 Radius=1.8
    g9: Circle CenterX=179.305 CenterY=-76.8316 CenterZ=0 NormalX=0 NormalY=0 NormalZ=1 AngleXU=0 Radius=1.8
    g10: ArcOfCircle [constr] CenterX=132.428 CenterY=4 CenterZ=0 NormalX=0 NormalY=0 NormalZ=1 AngleXU=0 Radius=16 StartAngle=0.314159 EndAngle=1.5708
    g11: ArcOfCircle CenterX=107.6 CenterY=4 CenterZ=0 NormalX=0 NormalY=0 NormalZ=1 AngleXU=0 Radius=16 StartAngle=1.5708 EndAngle=3.00366
    g12: ArcOfCircle CenterX=207.583 CenterY=4 CenterZ=0 NormalX=0 NormalY=0 NormalZ=1 AngleXU=0 Radius=17 StartAngle=1.85815 EndAngle=3.57792
    g13: ArcOfCircle CenterX=184.801 CenterY=-67.3089 CenterZ=0 NormalX=0 NormalY=0 NormalZ=1 AngleXU=0 Radius=33.7833 StartAngle=5.88425 EndAngle=6.71952
    g14: LineSegment StartX=0 StartY=39.2 StartZ=0 EndX=0 EndY=3.2 EndZ=0
    g15: LineSegment StartX=0 StartY=3.2 StartZ=0 EndX=82.8 EndY=3.2 EndZ=0
    g16: LineSegment StartX=82.8 StartY=3.2 StartZ=0 EndX=82.8 EndY=6.2 EndZ=0
    g17: LineSegment StartX=82.8 StartY=6.2 StartZ=0 EndX=91.752 EndY=6.2 EndZ=0
    g18: LineSegment StartX=107.6 StartY=20 StartZ=0 EndX=132.428 EndY=20 EndZ=0
    g19: LineSegment StartX=147.645 StartY=8.94427 StartZ=0 EndX=176.685 EndY=-80.4316 EndZ=0
    g20: LineSegment StartX=176.685 StartY=-80.4316 StartZ=0 EndX=215.932 EndY=-80.4316 EndZ=0
    g21: LineSegment StartX=215.42 StartY=-53.0314 StartZ=0 EndX=192.176 EndY=-3.18451 EndZ=0
    g22: LineSegment StartX=202.765 StartY=20.303 StartZ=0 EndX=195.887 EndY=39.2 EndZ=0
    g23: LineSegment StartX=195.887 StartY=39.2 StartZ=0 EndX=0 EndY=39.2 EndZ=0
    g24: LineSegment StartX=196.467 StartY=26.4942 StartZ=0 EndX=194.073 EndY=33.0721 EndZ=0
    g25: LineSegment StartX=194.073 StartY=33.0721 StartZ=0 EndX=189.939 EndY=31.5672 EndZ=0
    g26: LineSegment StartX=189.939 StartY=31.5672 StartZ=0 EndX=192.333 EndY=24.9893 EndZ=0
    g27: LineSegment StartX=192.333 StartY=24.9893 StartZ=0 EndX=196.467 EndY=26.4942 EndZ=0
    g28: LineSegment StartX=132.428 StartY=20 StartZ=0 EndX=144.053 EndY=20 EndZ=0
    g29: LineSegment StartX=144.053 StartY=20 StartZ=0 EndX=147.645 EndY=8.94427 EndZ=0
  constraints (65):
    c: Equal(g0,g-25)
    c: Equal(g2,g-29)
    c: Equal(g3,g-30)
    c: Equal(g4,g-28)
    c: Equal(g1,g-26)
    c: Coincident(g0,g-25)
    c: Coincident(g1,g-26)
    c: Coincident(g2,g-29)
    c: Coincident(g3,g-30)
    c: Coincident(g4,g-28)
    c: Equal(g5,g-23)
    c: Equal(g6,g-24)
    c: Coincident(g5,g-23)
    c: Coincident(g6,g-24)
    c: Equal(g7,g-20)
    c: Coincident(g7,g-20)
    c: Equal(g9,g-22)
    c: Coincident(g9,g-22)
    c: Equal(g8,g-21)
    c: Coincident(g8,g-21)
    c: Equal(g13,g-12)
    c: Equal(g12,g-14)
    c: Equal(g10,g-9)
    c: Equal(g11,g-7)
    c: Coincident(g14,g-27)
    c: Coincident(g14,g-27)
    c: Coincident(g15,g14)
    c: Coincident(g15,g-5)
    c: Coincident(g16,g15)
    c: Coincident(g16,g-6)
    c: Coincident(g17,g16)
    c: Coincident(g17,g-7)
    c: Coincident(g11,g17)
    c: Coincident(g11,g-8)
    c: Coincident(g18,g11)
    c: Coincident(g18,g-9)
    c: Coincident(g10,g18)
    c: Coincident(g10,g-10)
    c: Coincident(g19,g10)
    c: Coincident(g19,g-11)
    c: Coincident(g20,g19)
    c: Coincident(g20,g-12)
    c: Coincident(g13,g20)
    c: Coincident(g13,g-13)
    c: Coincident(g21,g13)
    c: Coincident(g21,g-14)
    c: Coincident(g12,g21)
    c: Coincident(g12,g-15)
    c: Coincident(g22,g12)
    c: Coincident(g22,g-15)
    c: Coincident(g23,g22)
    c: Coincident(g23,g14)
    c: Coincident(g24,g-18)
    c: Coincident(g24,g-16)
    c: Coincident(g25,g24)
    c: Coincident(g25,g-19)
    c: Coincident(g26,g25)
    c: Coincident(g26,g-19)
    c: Coincident(g27,g26)
    c: Coincident(g27,g24)
    c: Coincident(g29,g10)
    c: Coincident(g28,g10)
    c: Coincident(g29,g28)
    c: Parallel(g28,g18)
    c: Parallel(g29,g19)
FEATURE [PartDesign::Pad] Pad011
  Direction = (0,1,-2e-16)
  Length = 2
  Length2 = 10
  Profile = -> Sketch114
  ReferenceAxis = -> Sketch114 [N_Axis]
  Refine = true
  Reversed = true
  Suppressed = false
  Type = 0
FEATURE [Sketcher::SketchObject] Sketch115
  ArcFitTolerance = 1e-06
  AttachmentSupport = -> [Pad011]
  ExternalGeometry = -> [Binder001]
  FullyConstrained = true
  MakeInternals = false
  MapMode = 5
  Placement = pos=(0,1.7e-15,0) rot=(0,0.707107,0.707107;3.14159rad)
  sketch-geometry (4):
    g0: ArcOfCircle CenterX=24.2 CenterY=26.7 CenterZ=0 NormalX=0 NormalY=0 NormalZ=1 AngleXU=0 Radius=3 StartAngle=4.48384e-08 EndAngle=3.14159
    g1: ArcOfCircle CenterX=24.2 CenterY=15.7 CenterZ=0 NormalX=0 NormalY=0 NormalZ=1 AngleXU=0 Radius=3 StartAngle=3.14159 EndAngle=6.28318
    g2: LineSegment StartX=21.2 StartY=26.7 StartZ=0 EndX=21.2 EndY=15.7 EndZ=0
    g3: LineSegment StartX=27.2 StartY=26.7 StartZ=0 EndX=27.2 EndY=15.7 EndZ=0
  constraints (12):
    c: Equal(g1,g-4)
    c: Equal(g0,g-3)
    c: Coincident(g0,g-3)
    c: Coincident(g1,g-4)
    c: Vertical(g2)
    c: Vertical(g3)
    c: Tangent(g3,g-3)
    c: Tangent(g2,g-3)
    c: Coincident(g0,g2)
    c: Coincident(g0,g3)
    c: Coincident(g1,g2)
    c: Coincident(g3,g1)
FEATURE [Sketcher::SketchObject] Sketch117  label="Sketch117 - fori per inserto M3 x 3 x 4.5"
  ArcFitTolerance = 1e-06
  AttachmentSupport = -> [Pad011]
  ExternalGeometry = -> [Binder001]
  FullyConstrained = true
  MakeInternals = false
  MapMode = 5
  Placement = pos=(0,1.7e-15,0) rot=(0,0.707107,0.707107;3.14159rad)
  sketch-geometry (4):
    g0: Circle CenterX=43.2 CenterY=30.3 CenterZ=0 NormalX=0 NormalY=0 NormalZ=1 AngleXU=0 Radius=2.25
    g1: Circle CenterX=43.2 CenterY=12.1 CenterZ=0 NormalX=0 NormalY=0 NormalZ=1 AngleXU=0 Radius=2.25
    g2: Circle CenterX=18.6 CenterY=30.3 CenterZ=0 NormalX=0 NormalY=0 NormalZ=1 AngleXU=0 Radius=2.25
    g3: Circle CenterX=18.6 CenterY=12.1 CenterZ=0 NormalX=0 NormalY=0 NormalZ=1 AngleXU=0 Radius=2.25
  constraints (8):
    c: Diameter(g0) = 4.5
    c: Diameter(g1) = 4.5
    c: Diameter(g2) = 4.5
    c: Diameter(g3) = 4.5
    c: Coincident(g2,g-3)
    c: Coincident(g3,g-6)
    c: Coincident(g0,g-4)
    c: Coincident(g1,g-5)
FEATURE [Sketcher::SketchObject] Sketch118
  ArcFitTolerance = 1e-06
  AttachmentSupport = -> [Pad011]
  ExternalGeometry = -> [Binder001]
  FullyConstrained = true
  MakeInternals = false
  MapMode = 5
  Placement = pos=(0,-2,0) rot=(1,0,0;1.5708rad)
  sketch-geometry (12):
    g0: Circle CenterX=-78.51 CenterY=34.8 CenterZ=0 NormalX=0 NormalY=0 NormalZ=1 AngleXU=0 Radius=1.8
    g1: Circle CenterX=-78.51 CenterY=7.6 CenterZ=0 NormalX=0 NormalY=0 NormalZ=1 AngleXU=0 Radius=1.8
    g2: Circle CenterX=-5.6 CenterY=34.8 CenterZ=0 NormalX=0 NormalY=0 NormalZ=1 AngleXU=0 Radius=1.8
    g3: Circle CenterX=-5.6 CenterY=7.6 CenterZ=0 NormalX=0 NormalY=0 NormalZ=1 AngleXU=0 Radius=1.8
    g4: LineSegment StartX=0 StartY=39.2 StartZ=0 EndX=0 EndY=3.2 EndZ=0
    g5: LineSegment StartX=0 StartY=3.2 StartZ=0 EndX=-82.8 EndY=3.2 EndZ=0
    g6: LineSegment StartX=-82.8 StartY=3.2 StartZ=0 EndX=-82.8 EndY=39.2 EndZ=0
    g7: LineSegment StartX=-82.8 StartY=39.2 StartZ=0 EndX=0 EndY=39.2 EndZ=0
    g8: ArcOfCircle CenterX=-65 CenterY=21.2 CenterZ=0 NormalX=0 NormalY=0 NormalZ=1 AngleXU=0 Radius=10 StartAngle=1.5708 EndAngle=4.71239
    g9: ArcOfCircle CenterX=-19 CenterY=21.2 CenterZ=0 NormalX=0 NormalY=0 NormalZ=1 AngleXU=0 Radius=10 StartAngle=4.71239 EndAngle=7.85398
    g10: LineSegment StartX=-65 StartY=31.2 StartZ=0 EndX=-19 EndY=31.2 EndZ=0
    g11: LineSegment StartX=-65 StartY=11.2 StartZ=0 EndX=-19 EndY=11.2 EndZ=0
  constraints (25):
    c: Equal(g2,g-5)
    c: Equal(g3,g-7)
    c: Equal(g1,g-6)
    c: Equal(g0,g-4)
    c: Coincident(g0,g-4)
    c: Coincident(g1,g-6)
    c: Coincident(g3,g-7)
    c: Coincident(g2,g-5)
    c: Coincident(g4,g-8)
    c: Coincident(g4,g-9)
    c: Coincident(g5,g4)
    c: Coincident(g5,g-10)
    c: Coincident(g6,g5)
    c: PointOnObject(g6,g-3)
    c: Vertical(g6)
    c: Coincident(g7,g6)
    c: Coincident(g7,g4)
    c: Tangent(g8,g10) = 1.5708
    c: Tangent(g8,g11) = -1.5708
    c: Tangent(g9,g10) = 1.5708
    c: Tangent(g9,g11) = -1.5708
    c: Equal(g8,g9)
    c: Radius(g8) = 10
    c: Coincident(g8,g-11)
    c: Coincident(g9,g-12)
FEATURE [Sketcher::SketchObject] Sketch120
  ArcFitTolerance = 1e-06
  AttachmentSupport = -> [Pad011]
  ExternalGeometry = -> [Binder001]
  FullyConstrained = true
  MakeInternals = false
  MapMode = 5
  Placement = pos=(0,-2,0) rot=(1,0,0;1.5708rad)
  sketch-geometry (4):
    g0: LineSegment StartX=-137.815 StartY=39.2 StartZ=0 EndX=-142.655 EndY=24.303 EndZ=0
    g1: LineSegment StartX=-137.815 StartY=39.2 StartZ=0 EndX=-110.815 EndY=39.2 EndZ=0
    g2: LineSegment StartX=-142.655 StartY=24.303 StartZ=0 EndX=-110.815 EndY=24.303 EndZ=0
    g3: ArcOfCircle CenterX=-92.2534 CenterY=31.7515 CenterZ=0 NormalX=0 NormalY=0 NormalZ=1 AngleXU=0 Radius=20 StartAngle=2.75997 EndAngle=3.52321
  constraints (12):
    c: PointOnObject(g0,g-3)
    c: Coincident(g1,g0)
    c: PointOnObject(g1,g-3)
    c: Coincident(g2,g0)
    c: Horizontal(g2)
    c: Tangent(g0,g-4)
    c: Vertical(g2,g1)
    c: DistanceX(g1,g1) = 27
    c: DistanceY(g-6,g0) = 4
    c: Radius(g3) = 20
    c: Coincident(g3,g1)
    c: Coincident(g3,g2)
FEATURE [Sketcher::SketchObject] Sketch121
  ArcFitTolerance = 1e-06
  AttachmentSupport = -> [Pad011]
  ExternalGeometry = -> [Binder001]
  FullyConstrained = true
  MakeInternals = false
  MapMode = 5
  Placement = pos=(0,-2,0) rot=(1,0,0;1.5708rad)
  sketch-geometry (15):
    g0: LineSegment StartX=-137.815 StartY=39.2 StartZ=0 EndX=-143.955 EndY=20.303 EndZ=0
    g1: LineSegment StartX=-143.955 StartY=20.303 StartZ=0 EndX=-190.141 EndY=20.303 EndZ=0
    g2: LineSegment StartX=-190.141 StartY=20.303 StartZ=0 EndX=-186.139 EndY=31.3 EndZ=0
    g3: LineSegment StartX=-178.754 StartY=39.2 StartZ=0 EndX=-180.791 EndY=33.6029 EndZ=0
    g4: ArcOfCircle CenterX=-184.08 CenterY=34.8 CenterZ=0 NormalX=0 NormalY=0 NormalZ=1 AngleXU=0 Radius=3.5 StartAngle=4.71239 EndAngle=5.93412
    g5: LineSegment StartX=-184.08 StartY=31.3 StartZ=0 EndX=-186.139 EndY=31.3 EndZ=0
    g6: LineSegment StartX=-137.815 StartY=39.2 StartZ=0 EndX=-156.815 EndY=39.2 EndZ=0
    g7: LineSegment StartX=-168.815 StartY=39.2 StartZ=0 EndX=-178.754 EndY=39.2 EndZ=0
    g8: LineSegment StartX=-157.815 StartY=39.2 StartZ=0 EndX=-167.815 EndY=39.2 EndZ=0
    g9: LineSegment StartX=-168.815 StartY=31.2 StartZ=0 EndX=-156.815 EndY=31.2 EndZ=0
    g10: LineSegment StartX=-167.436 StartY=36.2 StartZ=0 EndX=-157.436 EndY=36.2 EndZ=0
    g11: ArcOfCircle CenterX=-176.411 CenterY=35.2 CenterZ=0 NormalX=0 NormalY=0 NormalZ=1 AngleXU=0 Radius=20 StartAngle=6.08183 EndAngle=6.48454
    g12: ArcOfCircle CenterX=-188.411 CenterY=35.2 CenterZ=0 NormalX=0 NormalY=0 NormalZ=1 AngleXU=0 Radius=20 StartAngle=6.08183 EndAngle=6.48454
    g13: ArcOfCircle CenterX=-177.411 CenterY=35.2 CenterZ=0 NormalX=0 NormalY=0 NormalZ=1 AngleXU=0 Radius=20 StartAngle=0.0500209 EndAngle=0.201358
    g14: ArcOfCircle CenterX=-187.411 CenterY=35.2 CenterZ=0 NormalX=0 NormalY=0 NormalZ=1 AngleXU=0 Radius=20 StartAngle=0.0500209 EndAngle=0.201358
  constraints (46):
    c: PointOnObject(g0,g-3)
    c: Tangent(g0,g-5)
    c: Coincident(g1,g0)
    c: Horizontal(g1)
    c: Coincident(g2,g1)
    c: PointOnObject(g3,g-3)
    c: Parallel(g3,g-6)
    c: Parallel(g2,g-6)
    c: Radius(g4) = 3.5
    c: Coincident(g4,g-7)
    c: Tangent(g3,g4) = 1.5708
    c: Horizontal(g5)
    c: Tangent(g5,g4) = 1.5708
    c: DistanceX(g-8,g5) = 3.8
    c: Coincident(g2,g5)
    c: Coincident(g6,g0)
    c: PointOnObject(g6,g-3)
    c: DistanceX(g6,g6) = 19
    c: PointOnObject(g7,g-3)
    c: DistanceX(g7,g6) = 12
    c: Coincident(g7,g3)
    c: PointOnObject(g8,g-3)
    c: PointOnObject(g8,g-3)
    c: DistanceX(g8,g8) = 10
    c: DistanceX(g8,g6) = 1
    c: Horizontal(g9)
    c: Vertical(g7,g9)
    c: Vertical(g6,g9)
    c: DistanceY(g9,g7) = 8
    c: Horizontal(g10)
    c: Equal(g8,g10)
    c: DistanceY(g10,g8) = 3
    c: Radius(g11) = 20
    c: Coincident(g11,g6)
    c: Coincident(g11,g9)
    c: Radius(g12) = 20
    c: Coincident(g12,g7)
    c: Coincident(g12,g9)
    c: Equal(g13,g11)
    c: Coincident(g13,g8)
    c: Coincident(g13,g10)
    c: Horizontal(g13,g11)
    c: Equal(g14,g12)
    c: Coincident(g14,g8)
    c: Coincident(g14,g10)
    c: Horizontal(g1,g-6)
FEATURE [Sketcher::SketchObject] Sketch122
  ArcFitTolerance = 1e-06
  AttachmentSupport = -> [Pad011]
  ExternalGeometry = -> [Binder001]
  FullyConstrained = true
  MakeInternals = false
  MapMode = 5
  Placement = pos=(0,-2,0) rot=(1,0,0;1.5708rad)
  sketch-geometry (8):
    g0: LineSegment StartX=-202.765 StartY=20.303 StartZ=0 EndX=-143.955 EndY=20.303 EndZ=0
    g1: ArcOfCircle CenterX=-184.801 CenterY=-67.3089 CenterZ=0 NormalX=0 NormalY=0 NormalZ=1 AngleXU=0 Radius=33.7833 StartAngle=2.70526 EndAngle=3.54053
    g2: LineSegment StartX=-176.685 StartY=-80.4316 StartZ=0 EndX=-215.932 EndY=-80.4316 EndZ=0
    g3: LineSegment StartX=-215.42 StartY=-53.0315 StartZ=0 EndX=-192.176 EndY=-3.18454 EndZ=0
    g4: ArcOfCircle CenterX=-207.583 CenterY=4 CenterZ=0 NormalX=0 NormalY=0 NormalZ=1 AngleXU=0 Radius=17 StartAngle=5.84685 EndAngle=7.56663
    g5: Circle CenterX=-213.443 CenterY=-76.8316 CenterZ=0 NormalX=0 NormalY=0 NormalZ=1 AngleXU=0 Radius=3
    g6: Circle CenterX=-179.305 CenterY=-76.8316 CenterZ=0 NormalX=0 NormalY=0 NormalZ=1 AngleXU=0 Radius=3
    g7: LineSegment StartX=-143.955 StartY=20.303 StartZ=0 EndX=-176.685 EndY=-80.4316 EndZ=0
  constraints (18):
    c: Coincident(g0,g-6)
    c: Coincident(g1,g-7)
    c: Coincident(g1,g-8)
    c: Coincident(g2,g1)
    c: Tangent(g3,g-5)
    c: Coincident(g4,g-6)
    c: Coincident(g4,g0)
    c: Coincident(g3,g4)
    c: Coincident(g1,g3)
    c: Diameter(g5) = 6
    c: Diameter(g6) = 6
    c: Coincident(g5,g-9)
    c: Coincident(g6,g-10)
    c: Horizontal(g0)
    c: Horizontal(g2)
    c: Coincident(g7,g0)
    c: Coincident(g7,g2)
    c: Tangent(g7,g-4)
FEATURE [Sketcher::SketchObject] Sketch123
  ArcFitTolerance = 1e-06
  AttachmentSupport = -> [Pad011]
  ExternalGeometry = -> [Binder001]
  FullyConstrained = true
  MakeInternals = false
  MapMode = 5
  Placement = pos=(0,-2,0) rot=(1,0,0;1.5708rad)
  sketch-geometry (4):
    g0: LineSegment StartX=-108 StartY=36.8 StartZ=0 EndX=-90 EndY=36.8 EndZ=0
    g1: LineSegment StartX=-108 StartY=36.8 StartZ=0 EndX=-108 EndY=26.8 EndZ=0
    g2: LineSegment StartX=-108 StartY=26.8 StartZ=0 EndX=-90 EndY=26.8 EndZ=0
    g3: ArcOfCircle CenterX=-94 CenterY=31.8 CenterZ=0 NormalX=0 NormalY=0 NormalZ=1 AngleXU=0 Radius=6.40312 StartAngle=5.38713 EndAngle=7.17924
  constraints (13):
    c: Horizontal(g0)
    c: Coincident(g1,g0)
    c: Vertical(g1)
    c: Coincident(g2,g1)
    c: Horizontal(g2)
    c: DistanceX(g0,g0) = 18
    c: DistanceY(g1,g1) = 10
    c: Equal(g0,g2)
    c: DistanceX(g0,g-3) = 90
    c: DistanceY(g0,g-3) = 2.4
    c: Coincident(g3,g0)
    c: Coincident(g3,g2)
    c: DistanceX(g3,g0) = 4
FEATURE [PartDesign::Chamfer] Chamfer014
  Angle = 45
  Base = -> Pad011 [Edge80,Edge4,Edge7]
  BaseFeature = -> Pad011
  ChamferType = 0
  FlipDirection = false
  Refine = true
  Size = 1.9
  Size2 = 1
  SupportTransform = false
  Suppressed = false
  UseAllEdges = false
FEATURE [PartDesign::Pocket] Pocket006
  BaseFeature = -> Chamfer014
  Direction = (0,-1,2e-16)
  Length = 1.2
  Length2 = 5
  Profile = -> Sketch115
  ReferenceAxis = -> Sketch115 [N_Axis]
  Refine = true
  Suppressed = false
  Type = 0
FEATURE [Sketcher::SketchObject] Sketch116  label="Sketch116 - pieno per inserto M3 x 3 x 4,5"
  ArcFitTolerance = 1e-06
  AttachmentSupport = -> [Pocket006]
  ExternalGeometry = -> [Binder001]
  FullyConstrained = true
  MakeInternals = false
  MapMode = 5
  Placement = pos=(0,1.7e-15,0) rot=(0,0.707107,0.707107;3.14159rad)
  sketch-geometry (4):
    g0: Circle CenterX=43.2 CenterY=30.3 CenterZ=0 NormalX=0 NormalY=0 NormalZ=1 AngleXU=0 Radius=3.4
    g1: Circle CenterX=43.2 CenterY=12.1 CenterZ=0 NormalX=0 NormalY=0 NormalZ=1 AngleXU=0 Radius=3.4
    g2: Circle CenterX=18.6 CenterY=30.3 CenterZ=0 NormalX=0 NormalY=0 NormalZ=1 AngleXU=0 Radius=3.4
    g3: Circle CenterX=18.6 CenterY=12.1 CenterZ=0 NormalX=0 NormalY=0 NormalZ=1 AngleXU=0 Radius=3.4
  constraints (8):
    c: Diameter(g0) = 6.8
    c: Diameter(g1) = 6.8
    c: Diameter(g2) = 6.8
    c: Diameter(g3) = 6.8
    c: Coincident(g2,g-3)
    c: Coincident(g0,g-4)
    c: Coincident(g3,g-6)
    c: Coincident(g1,g-5)
FEATURE [PartDesign::Pad] Pad012
  BaseFeature = -> Pocket006
  Direction = (0,1,-2e-16)
  Length = 2.4
  Length2 = 10
  Profile = -> Sketch116
  ReferenceAxis = -> Sketch116 [N_Axis]
  Refine = true
  Suppressed = false
  Type = 0
FEATURE [PartDesign::Pocket] Pocket007
  BaseFeature = -> Pad012
  Direction = (0,-1,2e-16)
  Length = 0.6
  Length2 = 2.4
  Profile = -> Sketch117
  ReferenceAxis = -> Sketch117 [N_Axis]
  Refine = true
  Suppressed = false
  Type = 4
FEATURE [PartDesign::Pad] Pad013
  BaseFeature = -> Pocket007
  Direction = (0,-1,2e-16)
  Length = 1.6
  Length2 = 10
  Profile = -> Sketch118
  ReferenceAxis = -> Sketch118 [N_Axis]
  Refine = true
  Suppressed = false
  Type = 0
FEATURE [Sketcher::SketchObject] Sketch119
  ArcFitTolerance = 1e-06
  AttachmentSupport = -> [Pad013]
  ExternalGeometry = -> [Binder001]
  FullyConstrained = true
  MakeInternals = false
  MapMode = 5
  Placement = pos=(0,-3.6,0) rot=(1,0,0;1.5708rad)
  sketch-geometry (21):
    g0: LineSegment [constr] StartX=-82.8 StartY=3.2 StartZ=0 EndX=-82.8 EndY=39.2 EndZ=0
    g1: ArcOfCircle CenterX=-78.51 CenterY=34.8 CenterZ=0 NormalX=0 NormalY=0 NormalZ=1 AngleXU=0 Radius=3.5 StartAngle=4.71239 EndAngle=6.28319
    g2: ArcOfCircle CenterX=-78.51 CenterY=7.6 CenterZ=0 NormalX=0 NormalY=0 NormalZ=1 AngleXU=0 Radius=3.5 StartAngle=0 EndAngle=1.5708
    g3: ArcOfCircle CenterX=-5.6 CenterY=34.8 CenterZ=0 NormalX=0 NormalY=0 NormalZ=1 AngleXU=0 Radius=3.5 StartAngle=3.14159 EndAngle=4.71239
    g4: ArcOfCircle CenterX=-5.6 CenterY=7.6 CenterZ=0 NormalX=0 NormalY=0 NormalZ=1 AngleXU=0 Radius=3.5 StartAngle=1.5708 EndAngle=3.14159
    g5: LineSegment StartX=0 StartY=39.2 StartZ=0 EndX=0 EndY=31.3 EndZ=0
    g6: LineSegment StartX=0 StartY=39.2 StartZ=0 EndX=-9.1 EndY=39.2 EndZ=0
    g7: LineSegment StartX=0 StartY=3.2 StartZ=0 EndX=0 EndY=11.1 EndZ=0
    g8: LineSegment StartX=0 StartY=3.2 StartZ=0 EndX=-9.1 EndY=3.2 EndZ=0
    g9: LineSegment StartX=-82.8 StartY=3.2 StartZ=0 EndX=-75.01 EndY=3.2 EndZ=0
    g10: LineSegment StartX=-82.8 StartY=3.2 StartZ=0 EndX=-82.8 EndY=11.1 EndZ=0
    g11: LineSegment StartX=-82.8 StartY=39.2 StartZ=0 EndX=-82.8 EndY=31.3 EndZ=0
    g12: LineSegment StartX=-82.8 StartY=39.2 StartZ=0 EndX=-75.01 EndY=39.2 EndZ=0
    g13: LineSegment StartX=-82.8 StartY=31.3 StartZ=0 EndX=-78.51 EndY=31.3 EndZ=0
    g14: LineSegment StartX=-75.01 StartY=39.2 StartZ=0 EndX=-75.01 EndY=34.8 EndZ=0
    g15: LineSegment StartX=-82.8 StartY=11.1 StartZ=0 EndX=-78.51 EndY=11.1 EndZ=0
    g16: LineSegment StartX=-75.01 StartY=3.2 StartZ=0 EndX=-75.01 EndY=7.6 EndZ=0
    g17: LineSegment StartX=-9.1 StartY=39.2 StartZ=0 EndX=-9.1 EndY=34.8 EndZ=0
    g18: LineSegment StartX=0 StartY=31.3 StartZ=0 EndX=-5.6 EndY=31.3 EndZ=0
    g19: LineSegment StartX=0 StartY=11.1 StartZ=0 EndX=-5.6 EndY=11.1 EndZ=0
    g20: LineSegment StartX=-9.1 StartY=3.2 StartZ=0 EndX=-9.1 EndY=7.6 EndZ=0
  constraints (51):
    c: Coincident(g0,g-10)
    c: PointOnObject(g0,g-8)
    c: Vertical(g0)
    c: Coincident(g1,g-3)
    c: Coincident(g2,g-4)
    c: Coincident(g3,g-5)
    c: Coincident(g4,g-6)
    c: Radius(g4) = 3.5
    c: Radius(g3) = 3.5
    c: Radius(g1) = 3.5
    c: Radius(g2) = 3.5
    c: Coincident(g5,g-9)
    c: PointOnObject(g5,g-9)
    c: Coincident(g6,g5)
    c: PointOnObject(g6,g-8)
    c: Coincident(g7,g-9)
    c: PointOnObject(g7,g-9)
    c: Coincident(g8,g7)
    c: PointOnObject(g8,g-7)
    c: Coincident(g9,g0)
    c: PointOnObject(g9,g-7)
    c: Coincident(g10,g0)
    c: PointOnObject(g10,g0)
    c: Coincident(g11,g0)
    c: PointOnObject(g11,g0)
    c: Coincident(g12,g0)
    c: PointOnObject(g12,g-8)
    c: Coincident(g13,g11)
    c: Horizontal(g13)
    c: Coincident(g14,g12)
    c: Vertical(g14)
    c: Coincident(g15,g10)
    c: Horizontal(g15)
    c: Coincident(g16,g9)
    c: Vertical(g16)
    c: Coincident(g17,g6)
    c: Vertical(g17)
    c: Coincident(g18,g5)
    c: Horizontal(g18)
    c: Coincident(g19,g7)
    c: Horizontal(g19)
    c: Coincident(g20,g8)
    c: Vertical(g20)
    c: Tangent(g20,g4) = 1.5708
    c: Tangent(g4,g19) = -1.5708
    c: Tangent(g18,g3) = 1.5708
    c: Tangent(g3,g17) = -1.5708
    c: Tangent(g13,g1) = -1.5708
    c: Tangent(g1,g14) = 1.5708
    c: Tangent(g16,g2) = -1.5708
    c: Tangent(g2,g15) = 1.5708
FEATURE [PartDesign::Pocket] Pocket008
  BaseFeature = -> Pad013
  Direction = (0,1,-2e-16)
  Length = 1.6
  Length2 = 5
  Profile = -> Sketch119
  ReferenceAxis = -> Sketch119 [N_Axis]
  Refine = true
  Suppressed = false
  Type = 0
FEATURE [PartDesign::Pad] Pad017
  BaseFeature = -> Pocket008
  Direction = (0,-1,2e-16)
  Length = 1.6
  Length2 = 10
  Profile = -> Sketch123
  ReferenceAxis = -> Sketch123 [N_Axis]
  Refine = true
  Suppressed = false
  Type = 0
FEATURE [Sketcher::SketchObject] Sketch125
  ArcFitTolerance = 1e-06
  AttachmentSupport = -> [Pad017]
  ExternalGeometry = -> [Pad017]
  FullyConstrained = true
  MakeInternals = false
  MapMode = 5
  Placement = pos=(0,-3.6,8e-16) rot=(1,0,0;1.5708rad)
  sketch-geometry (20):
    g0: LineSegment StartX=-108 StartY=35.8 StartZ=0 EndX=-108 EndY=35 EndZ=0
    g1: LineSegment StartX=-108 StartY=35 StartZ=0 EndX=-97 EndY=35 EndZ=0
    g2: LineSegment StartX=-97 StartY=35 StartZ=0 EndX=-97 EndY=35.8 EndZ=0
    g3: LineSegment StartX=-97 StartY=35.8 StartZ=0 EndX=-108 EndY=35.8 EndZ=0
    g4: LineSegment StartX=-108 StartY=28.6 StartZ=0 EndX=-108 EndY=27.8 EndZ=0
    g5: LineSegment StartX=-108 StartY=27.8 StartZ=0 EndX=-97 EndY=27.8 EndZ=0
    g6: LineSegment StartX=-97 StartY=27.8 StartZ=0 EndX=-97 EndY=28.6 EndZ=0
    g7: LineSegment StartX=-97 StartY=28.6 StartZ=0 EndX=-108 EndY=28.6 EndZ=0
    g8: LineSegment StartX=-108 StartY=30.4 StartZ=0 EndX=-108 EndY=29.6 EndZ=0
    g9: LineSegment StartX=-108 StartY=29.6 StartZ=0 EndX=-97 EndY=29.6 EndZ=0
    g10: LineSegment StartX=-97 StartY=29.6 StartZ=0 EndX=-97 EndY=30.4 EndZ=0
    g11: LineSegment StartX=-97 StartY=30.4 StartZ=0 EndX=-108 EndY=30.4 EndZ=0
    g12: LineSegment StartX=-108 StartY=32.2 StartZ=0 EndX=-108 EndY=31.4 EndZ=0
    g13: LineSegment StartX=-108 StartY=31.4 StartZ=0 EndX=-97 EndY=31.4 EndZ=0
    g14: LineSegment StartX=-97 StartY=31.4 StartZ=0 EndX=-97 EndY=32.2 EndZ=0
    g15: LineSegment StartX=-97 StartY=32.2 StartZ=0 EndX=-108 EndY=32.2 EndZ=0
    g16: LineSegment StartX=-108 StartY=34 StartZ=0 EndX=-108 EndY=33.2 EndZ=0
    g17: LineSegment StartX=-108 StartY=33.2 StartZ=0 EndX=-97 EndY=33.2 EndZ=0
    g18: LineSegment StartX=-97 StartY=33.2 StartZ=0 EndX=-97 EndY=34 EndZ=0
    g19: LineSegment StartX=-97 StartY=34 StartZ=0 EndX=-108 EndY=34 EndZ=0
  constraints (55):
    c: Coincident(g1,g0)
    c: Horizontal(g1)
    c: Coincident(g2,g1)
    c: Vertical(g2)
    c: Coincident(g3,g2)
    c: Horizontal(g3)
    c: Coincident(g3,g0)
    c: DistanceX(g1,g1) = 11
    c: DistanceY(g2,g2) = 0.8
    c: Coincident(g5,g4)
    c: Horizontal(g5)
    c: Coincident(g6,g5)
    c: Vertical(g6)
    c: Coincident(g7,g6)
    c: Horizontal(g7)
    c: Coincident(g7,g4)
    c: Coincident(g9,g8)
    c: Horizontal(g9)
    c: Coincident(g10,g9)
    c: Vertical(g10)
    c: Coincident(g11,g10)
    c: Horizontal(g11)
    c: Coincident(g11,g8)
    c: Coincident(g13,g12)
    c: Horizontal(g13)
    c: Coincident(g14,g13)
    c: Vertical(g14)
    c: Coincident(g15,g14)
    c: Horizontal(g15)
    c: Coincident(g15,g12)
    c: Coincident(g17,g16)
    c: Horizontal(g17)
    c: Coincident(g18,g17)
    c: Vertical(g18)
    c: Coincident(g19,g18)
    c: Horizontal(g19)
    c: Coincident(g19,g16)
    c: Equal(g3,g19)
    c: Equal(g3,g15)
    c: Equal(g3,g11)
    c: Equal(g3,g7)
    c: Equal(g2,g18)
    c: Equal(g2,g14)
    c: Equal(g2,g10)
    c: Equal(g2,g6)
    c: DistanceY(g-4,g4) = 1
    c: DistanceY(g4,g8) = 1
    c: DistanceY(g8,g12) = 1
    c: DistanceY(g12,g16) = 1
    c: DistanceY(g16,g0) = 1
    c: Tangent(g0,g-5)
    c: Tangent(g16,g-5)
    c: Tangent(g12,g-5)
    c: Tangent(g8,g-5)
    c: Tangent(g4,g-5)
FEATURE [PartDesign::Chamfer] Chamfer009
  Angle = 45
  Base = -> Pad017 [Edge151,Edge154]
  BaseFeature = -> Pad017
  ChamferType = 1
  FlipDirection = false
  Refine = true
  Size = 1.5
  Size2 = 2.8
  SupportTransform = false
  Suppressed = false
  UseAllEdges = false
FEATURE [PartDesign::Pocket] Pocket009
  BaseFeature = -> Chamfer009
  Direction = (0,1,-2e-16)
  Length = 1
  Length2 = 5
  Profile = -> Sketch125
  ReferenceAxis = -> Sketch125 [N_Axis]
  Refine = true
  Suppressed = false
  Type = 0
FEATURE [PartDesign::Pad] Pad014
  BaseFeature = -> Pocket009
  Direction = (0,-1,2e-16)
  Length = 0.8
  Length2 = 10
  Profile = -> Sketch120
  ReferenceAxis = -> Sketch120 [N_Axis]
  Refine = true
  Suppressed = false
  Type = 0
FEATURE [Sketcher::SketchObject] Sketch124
  ArcFitTolerance = 1e-06
  AttachmentSupport = -> [Pad014]
  ExternalGeometry = -> [Binder001]
  FullyConstrained = true
  MakeInternals = false
  MapMode = 5
  Placement = pos=(0,-2.8,6e-16) rot=(1,0,0;1.5708rad)
  sketch-geometry (4):
    g0: LineSegment StartX=-129 StartY=39.2 StartZ=0 EndX=-131.599 EndY=31.2 EndZ=0
    g1: LineSegment StartX=-118 StartY=39.2 StartZ=0 EndX=-120.599 EndY=31.2 EndZ=0
    g2: LineSegment StartX=-129 StartY=39.2 StartZ=0 EndX=-118 EndY=39.2 EndZ=0
    g3: LineSegment StartX=-120.599 StartY=31.2 StartZ=0 EndX=-131.599 EndY=31.2 EndZ=0
  constraints (12):
    c: PointOnObject(g0,g-3)
    c: PointOnObject(g1,g-3)
    c: Parallel(g-4,g0)
    c: Parallel(g-4,g1)
    c: Coincident(g2,g0)
    c: Coincident(g2,g1)
    c: DistanceX(g2,g2) = 11
    c: DistanceY(g1,g1) = 8
    c: Coincident(g3,g1)
    c: Horizontal(g3)
    c: Coincident(g3,g0)
    c: DistanceX(g1,g-3) = 118
FEATURE [PartDesign::Pad] Pad018
  BaseFeature = -> Pad014
  Direction = (0,-1,2e-16)
  Length = 1.2
  Length2 = 10
  Profile = -> Sketch124
  ReferenceAxis = -> Sketch124 [N_Axis]
  Refine = true
  Suppressed = false
  Type = 0
FEATURE [Sketcher::SketchObject] Sketch126
  ArcFitTolerance = 1e-06
  AttachmentSupport = -> [Pad018]
  ExternalGeometry = -> [Pad018]
  FullyConstrained = true
  MakeInternals = false
  MapMode = 5
  Placement = pos=(0,-4,0) rot=(1,0,0;1.5708rad)
  sketch-geometry (8):
    g0: LineSegment StartX=-129.877 StartY=36.5 StartZ=0 EndX=-130.137 EndY=35.7 EndZ=0
    g1: LineSegment StartX=-130.69 StartY=34 StartZ=0 EndX=-130.95 EndY=33.2 EndZ=0
    g2: LineSegment StartX=-129.877 StartY=36.5 StartZ=0 EndX=-118.877 EndY=36.5 EndZ=0
    g3: LineSegment StartX=-130.137 StartY=35.7 StartZ=0 EndX=-119.137 EndY=35.7 EndZ=0
    g4: LineSegment StartX=-130.69 StartY=34 StartZ=0 EndX=-119.69 EndY=34 EndZ=0
    g5: LineSegment StartX=-130.95 StartY=33.2 StartZ=0 EndX=-119.95 EndY=33.2 EndZ=0
    g6: LineSegment StartX=-118.877 StartY=36.5 StartZ=0 EndX=-119.137 EndY=35.7 EndZ=0
    g7: LineSegment StartX=-119.69 StartY=34 StartZ=0 EndX=-119.95 EndY=33.2 EndZ=0
  constraints (20):
    c: Coincident(g2,g0)
    c: Horizontal(g2)
    c: Coincident(g3,g0)
    c: Horizontal(g3)
    c: Coincident(g4,g1)
    c: Horizontal(g4)
    c: Coincident(g5,g1)
    c: Horizontal(g5)
    c: Coincident(g6,g2)
    c: Coincident(g6,g3)
    c: Coincident(g7,g4)
    c: Coincident(g7,g5)
    c: Tangent(g0,g-4)
    c: Tangent(g6,g-5)
    c: Tangent(g1,g-4)
    c: Tangent(g7,g-5)
    c: DistanceY(g3,g2) = 0.8
    c: DistanceY(g5,g4) = 0.8
    c: DistanceY(g-6,g1) = 2
    c: DistanceY(g-6,g0) = 4.5
FEATURE [PartDesign::Chamfer] Chamfer008
  Angle = 45
  Base = -> Pad018 [Edge257]
  BaseFeature = -> Pad018
  ChamferType = 1
  FlipDirection = false
  Refine = true
  Size = 1
  Size2 = 6
  SupportTransform = false
  Suppressed = false
  UseAllEdges = false
FEATURE [PartDesign::Pocket] Pocket010
  BaseFeature = -> Chamfer008
  Direction = (0,1,-2e-16)
  Length = 1
  Length2 = 5
  Profile = -> Sketch126
  ReferenceAxis = -> Sketch126 [N_Axis]
  Refine = true
  Suppressed = false
  Type = 0
FEATURE [PartDesign::Pad] Pad015
  BaseFeature = -> Pocket010
  Direction = (0,-1,2e-16)
  Length = 2
  Length2 = 10
  Profile = -> Sketch121
  ReferenceAxis = -> Sketch121 [N_Axis]
  Refine = true
  Suppressed = false
  Type = 0
FEATURE [PartDesign::Pad] Pad016
  BaseFeature = -> Pad015
  Direction = (0,-1,2e-16)
  Length = 1.6
  Length2 = 10
  Profile = -> Sketch122
  ReferenceAxis = -> Sketch122 [N_Axis]
  Refine = true
  Suppressed = false
  Type = 0
FEATURE [Sketcher::SketchObject] Sketch127
  ArcFitTolerance = 1e-06
  AttachmentSupport = -> [Pad016]
  ExternalGeometry = -> [Pad016]
  FullyConstrained = true
  MakeInternals = false
  MapMode = 5
  Placement = pos=(0,0,-80.4316) rot=(1,0,0;3.14159rad)
  sketch-geometry (8):
    g0: LineSegment StartX=-176.685 StartY=3.6 StartZ=0 EndX=-186.685 EndY=3.6 EndZ=0
    g1: LineSegment [constr] StartX=-186.685 StartY=3.6 StartZ=0 EndX=-186.685 EndY=-9e-16 EndZ=0
    g2: LineSegment StartX=-176.685 StartY=3.6 StartZ=0 EndX=-176.685 EndY=0 EndZ=0
    g3: ArcOfEllipse CenterX=-186.685 CenterY=-9e-16 CenterZ=0 NormalX=0 NormalY=0 NormalZ=1 MajorRadius=10 MinorRadius=3.6 AngleXU=1e-16 StartAngle=0 EndAngle=1.5708
    g4: LineSegment [constr] StartX=-176.685 StartY=-2e-15 StartZ=0 EndX=-196.685 EndY=-2e-15 EndZ=0
    g5: LineSegment [constr] StartX=-186.685 StartY=3.6 StartZ=0 EndX=-186.685 EndY=-3.6 EndZ=0
    g6: GeomPoint [constr] X=-177.356 Y=0 Z=0
    g7: GeomPoint [constr] X=-196.015 Y=-1.9e-15 Z=0
  constraints (13):
    c: Coincident(g0,g-4)
    c: PointOnObject(g0,g-4)
    c: DistanceX(g0,g0) = 10
    c: Coincident(g1,g0)
    c: PointOnObject(g1,g-5)
    c: Vertical(g1)
    c: Coincident(g2,g0)
    c: Coincident(g2,g-5)
    c: InternalAlignment(g4-g7 -> g3) x4
    c: Coincident(g3,g1)
    c: Coincident(g3,g0)
    c: Coincident(g3,g2)
    c: Horizontal(g4)
FEATURE [Sketcher::SketchObject] Sketch128
  ArcFitTolerance = 1e-06
  AttachmentSupport = -> [Pad016]
  ExternalGeometry = -> [Pad016]
  FullyConstrained = true
  MakeInternals = false
  MapMode = 5
  Placement = pos=(0,0,-80.4316) rot=(1,0,0;3.14159rad)
  sketch-geometry (8):
    g0: LineSegment StartX=-215.932 StartY=3.6 StartZ=0 EndX=-215.932 EndY=-1.3e-15 EndZ=0
    g1: LineSegment StartX=-215.932 StartY=3.6 StartZ=0 EndX=-205.932 EndY=3.6 EndZ=0
    g2: LineSegment [constr] StartX=-205.932 StartY=3.6 StartZ=0 EndX=-205.932 EndY=-9e-16 EndZ=0
    g3: ArcOfEllipse CenterX=-205.932 CenterY=-9e-16 CenterZ=0 NormalX=0 NormalY=0 NormalZ=1 MajorRadius=10 MinorRadius=3.6 AngleXU=-3.14159 StartAngle=4.71239 EndAngle=6.28319
    g4: LineSegment [constr] StartX=-215.932 StartY=-1e-15 StartZ=0 EndX=-195.932 EndY=-1e-15 EndZ=0
    g5: LineSegment [constr] StartX=-205.932 StartY=-3.6 StartZ=0 EndX=-205.932 EndY=3.6 EndZ=0
    g6: GeomPoint [constr] X=-215.262 Y=-2e-15 Z=0
    g7: GeomPoint [constr] X=-196.602 Y=-1e-15 Z=0
  constraints (13):
    c: Coincident(g0,g-4)
    c: Coincident(g0,g-5)
    c: Coincident(g1,g0)
    c: PointOnObject(g1,g-3)
    c: DistanceX(g1,g1) = 10
    c: Coincident(g2,g1)
    c: Vertical(g2)
    c: PointOnObject(g2,g-5)
    c: InternalAlignment(g4-g7 -> g3) x4
    c: Coincident(g3,g2)
    c: Coincident(g3,g1)
    c: Coincident(g3,g0)
    c: Horizontal(g4)
FEATURE [PartDesign::SubtractivePipe] SubtractivePipe002
  AuxilleryCurvelinear = true
  AuxillerySpineTangent = false
  BaseFeature = -> Pad016
  Binormal = (0,0,0)
  Mode = 0
  Profile = -> Sketch127
  Refine = true
  Spine = -> Pad016 [Edge254]
  SpineTangent = false
  Suppressed = false
  Transformation = 0
  Transition = 0
FEATURE [PartDesign::SubtractivePipe] SubtractivePipe003
  AuxilleryCurvelinear = true
  AuxillerySpineTangent = false
  BaseFeature = -> SubtractivePipe002
  Binormal = (0,0,0)
  Mode = 0
  Profile = -> Sketch128
  Refine = true
  Spine = -> Pad016 [Edge256,Edge251,Edge252]
  SpineTangent = false
  Suppressed = false
  Transformation = 0
  Transition = 0
FEATURE [Sketcher::SketchObject] Sketch129
  ArcFitTolerance = 1e-06
  AttachmentSupport = -> [Pad016]
  ExternalGeometry = -> [Binder001]
  FullyConstrained = true
  MakeInternals = false
  MapMode = 5
  Placement = pos=(0,-3.6,0) rot=(1,0,0;1.5708rad)
  sketch-geometry (12):
    g0: LineSegment [constr] StartX=-192.176 StartY=-3.18451 StartZ=0 EndX=-181.223 EndY=20.303 EndZ=0
    g1: LineSegment [constr] StartX=-202.765 StartY=20.303 StartZ=0 EndX=-181.223 EndY=20.303 EndZ=0
    g2: LineSegment StartX=-202.765 StartY=20.303 StartZ=0 EndX=-181.223 EndY=20.303 EndZ=0
    g3: LineSegment StartX=-192.176 StartY=-3.18451 StartZ=0 EndX=-196.804 EndY=-13.1107 EndZ=0
    g4: ArcOfCircle CenterX=-207.583 CenterY=4 CenterZ=0 NormalX=0 NormalY=0 NormalZ=1 AngleXU=0 Radius=17 StartAngle=5.84685 EndAngle=7.56663
    g5: ArcOfEllipse CenterX=-181.223 CenterY=8.55923 CenterZ=0 NormalX=0 NormalY=0 NormalZ=1 MajorRadius=23.4779 MinorRadius=11.7437 AngleXU=2e-16 StartAngle=4.71239 EndAngle=7.85398
    g6: LineSegment [constr] StartX=-157.745 StartY=8.55923 StartZ=0 EndX=-204.701 EndY=8.55923 EndZ=0
    g7: LineSegment [constr] StartX=-181.223 StartY=20.303 StartZ=0 EndX=-181.223 EndY=-3.18451 EndZ=0
    g8: GeomPoint [constr] X=-160.894 Y=8.55923 Z=0
    g9: GeomPoint [constr] X=-201.553 Y=8.55923 Z=0
    g10: ArcOfCircle CenterX=-181.223 CenterY=-20.3763 CenterZ=0 NormalX=0 NormalY=0 NormalZ=1 AngleXU=0 Radius=17.1918 StartAngle=1.57079 EndAngle=2.70526
    g11: GeomPoint [constr] X=-181.223 Y=-3.18451 Z=0
  constraints (23):
    c: Coincident(g0,g-5)
    c: Coincident(g1,g-6)
    c: Horizontal(g1)
    c: Coincident(g1,g0)
    c: Parallel(g0,g-4)
    c: Coincident(g2,g1)
    c: Coincident(g2,g0)
    c: Coincident(g3,g0)
    c: Equal(g4,g-5)
    c: Coincident(g4,g1)
    c: Coincident(g4,g0)
    c: InternalAlignment(g6-g9 -> g5) x4
    c: Vertical(g5,g0)
    c: Horizontal(g6)
    c: Coincident(g5,g0)
    c: DistanceX(g6,g-3) = 10.1
    c: Tangent(g10,g3) = -1.5708
    c: PointOnObject(g11,g10)
    c: Tangent(g5,g10,g11) = 1.5708
    c: Coincident(g10,g5)
    c: Coincident(g11,g7)
    c: Parallel(g3,g-4)
    c: Horizontal(g5,g0)
FEATURE [Sketcher::SketchObject] Sketch130
  ArcFitTolerance = 1e-06
  AttachmentOffset = pos=(0,0,-1.6) rot=(0,0,1;0rad)
  AttachmentSupport = -> [Pad016]
  ExternalGeometry = -> [Binder001]
  FullyConstrained = true
  MakeInternals = false
  MapMode = 5
  Placement = pos=(0,-2,-4e-16) rot=(1,0,0;1.5708rad)
  sketch-geometry (12):
    g0: LineSegment [constr] StartX=-192.176 StartY=-3.18451 StartZ=0 EndX=-181.223 EndY=20.303 EndZ=0
    g1: LineSegment [constr] StartX=-202.765 StartY=20.303 StartZ=0 EndX=-181.223 EndY=20.303 EndZ=0
    g2: LineSegment StartX=-202.765 StartY=20.303 StartZ=0 EndX=-181.223 EndY=20.303 EndZ=0
    g3: LineSegment StartX=-192.176 StartY=-3.18451 StartZ=0 EndX=-193.827 EndY=-6.72678 EndZ=0
    g4: ArcOfCircle CenterX=-207.583 CenterY=4 CenterZ=0 NormalX=0 NormalY=0 NormalZ=1 AngleXU=0 Radius=17 StartAngle=5.84685 EndAngle=7.56663
    g5: ArcOfEllipse CenterX=-181.223 CenterY=10.803 CenterZ=0 NormalX=0 NormalY=0 NormalZ=1 MajorRadius=14.4779 MinorRadius=9.5 AngleXU=0 StartAngle=4.71239 EndAngle=7.85398
    g6: LineSegment [constr] StartX=-166.745 StartY=10.803 StartZ=0 EndX=-195.701 EndY=10.803 EndZ=0
    g7: LineSegment [constr] StartX=-181.223 StartY=20.303 StartZ=0 EndX=-181.223 EndY=1.30297 EndZ=0
    g8: GeomPoint [constr] X=-170.298 Y=10.803 Z=0
    g9: GeomPoint [constr] X=-192.148 Y=10.803 Z=0
    g10: ArcOfCircle CenterX=-181.223 CenterY=-12.6042 CenterZ=0 NormalX=0 NormalY=0 NormalZ=1 AngleXU=0 Radius=13.9072 StartAngle=1.5708 EndAngle=2.70526
    g11: GeomPoint [constr] X=-181.223 Y=1.30297 Z=0
  constraints (23):
    c: Coincident(g0,g-5)
    c: Coincident(g1,g-6)
    c: Horizontal(g1)
    c: Coincident(g1,g0)
    c: Parallel(g0,g-4)
    c: Coincident(g2,g1)
    c: Coincident(g2,g0)
    c: Coincident(g3,g0)
    c: Equal(g4,g-5)
    c: Coincident(g4,g1)
    c: Coincident(g4,g0)
    c: InternalAlignment(g6-g9 -> g5) x4
    c: Vertical(g5,g0)
    c: Horizontal(g6)
    c: Coincident(g5,g0)
    c: DistanceX(g6,g-3) = 19.1
    c: Tangent(g10,g3) = -1.5708
    c: PointOnObject(g11,g10)
    c: Tangent(g5,g10,g11) = 1.5708
    c: Coincident(g10,g5)
    c: Coincident(g11,g7)
    c: Parallel(g3,g-4)
    c: DistanceY(g5,g0) = 19
FEATURE [Part::Part2DObjectPython] Clone2D001  label="Sketch130 (2D)"  # Draft 2D object (typed FeaturePython)
  Fuse = false
  Objects = -> [Sketch130]
  Placement = pos=(0,-2,-4e-16) rot=(1,0,0;1.5708rad)
  Scale = (1,1,1)
FEATURE [Sketcher::SketchObject] Sketch131
  ArcFitTolerance = 1e-06
  AttachmentOffset = pos=(0,0,-3.5) rot=(0,0,1;0rad)
  AttachmentSupport = -> [Pad016]
  ExternalGeometry = -> [Binder001]
  FullyConstrained = true
  MakeInternals = false
  MapMode = 5
  Placement = pos=(0,-0.1,-8e-16) rot=(1,0,0;1.5708rad)
  sketch-geometry (1):
    g0: GeomPoint X=-197.47 Y=8.55923 Z=0
  constraints (1):
    c: Symmetric(g-6,g-4,g0)
FEATURE [PartDesign::SubtractiveLoft] SubtractiveLoft002
  BaseFeature = -> SubtractivePipe003
  Closed = false
  Profile = -> Sketch129
  Refine = true
  Ruled = false
  Sections = -> [Sketch130]
  Suppressed = false
FEATURE [PartDesign::SubtractiveLoft] SubtractiveLoft003
  BaseFeature = -> SubtractiveLoft002
  Closed = false
  Profile = -> Clone2D001
  Refine = true
  Ruled = false
  Sections = -> [Sketch131]
  Suppressed = false
FEATURE [PartDesign::Chamfer] Chamfer010
  Angle = 45
  Base = -> SubtractiveLoft003 [Edge200,Edge201,Edge203,Edge202,Edge194]
  BaseFeature = -> SubtractiveLoft003
  ChamferType = 0
  FlipDirection = false
  Refine = true
  Size = 1.5
  Size2 = 1
  SupportTransform = false
  Suppressed = false
  UseAllEdges = false
FEATURE [PartDesign::Chamfer] Chamfer011
  Angle = 45
  Base = -> Chamfer010 [Edge15]
  BaseFeature = -> Chamfer010
  ChamferType = 0
  FlipDirection = false
  Refine = true
  Size = 3.5
  Size2 = 1
  SupportTransform = false
  Suppressed = false
  UseAllEdges = false
FEATURE [PartDesign::Chamfer] Chamfer012
  Angle = 45
  Base = -> Chamfer011 [Edge10]
  BaseFeature = -> Chamfer011
  ChamferType = 0
  FlipDirection = false
  Refine = true
  Size = 3.5
  Size2 = 1
  SupportTransform = false
  Suppressed = false
  UseAllEdges = false
FEATURE [PartDesign::Chamfer] Chamfer013
  Angle = 45
  Base = -> Chamfer012 [Edge146,Edge93]
  BaseFeature = -> Chamfer012
  ChamferType = 0
  FlipDirection = false
  Refine = true
  Size = 1.9
  Size2 = 1
  SupportTransform = false
  Suppressed = false
  UseAllEdges = false
FEATURE [Sketcher::SketchObject] Sketch132
  ArcFitTolerance = 1e-06
  AttachmentSupport = -> [Pad016]
  ExternalGeometry = -> [Binder001]
  FullyConstrained = true
  MakeInternals = false
  MapMode = 5
  Placement = pos=(0,-3.6,0) rot=(1,0,0;1.5708rad)
  sketch-geometry (3):
    g0: LineSegment [constr] StartX=-215.42 StartY=-53.0314 StartZ=0 EndX=-167.782 EndY=-53.0314 EndZ=0
    g1: Circle CenterX=-191.282 CenterY=-53.0314 CenterZ=0 NormalX=0 NormalY=0 NormalZ=1 AngleXU=0 Radius=11.5
    g2: Circle CenterX=-191.282 CenterY=-53.0314 CenterZ=0 NormalX=0 NormalY=0 NormalZ=1 AngleXU=0 Radius=10.7
  constraints (8):
    c: Coincident(g0,g-3)
    c: PointOnObject(g0,g-4)
    c: Horizontal(g0)
    c: Diameter(g1) = 23
    c: PointOnObject(g1,g0)
    c: DistanceX(g1,g0) = 23.5
    c: Diameter(g2) = 21.4
    c: Coincident(g2,g1)
FEATURE [PartDesign::Fillet] Fillet007
  Base = -> Chamfer013 [Edge84]
  BaseFeature = -> Chamfer013
  Radius = 1.1
  Refine = true
  SupportTransform = false
  Suppressed = false
  UseAllEdges = false
FEATURE [PartDesign::Fillet] Fillet008
  Base = -> Fillet007 [Edge77]
  BaseFeature = -> Fillet007
  Radius = 1.9
  Refine = true
  SupportTransform = false
  Suppressed = false
  UseAllEdges = false
FEATURE [PartDesign::Pocket] Pocket011
  BaseFeature = -> Fillet008
  Direction = (0,1,-2e-16)
  Length = 0.8
  Length2 = 5
  Profile = -> Sketch132
  ReferenceAxis = -> Sketch132 [N_Axis]
  Refine = true
  Suppressed = false
  Type = 0
FEATURE [Part::Part2DObjectPython] ShapeString  # Draft 2D object (typed FeaturePython)
  FontFile = <path>
  Fuse = false
  Justification = 6
  JustificationReference = 0
  KeepLeftMargin = false
  MakeFace = true
  ObliqueAngle = 0
  Placement = pos=(-199,-3.6,-57.5) rot=(1,0,0;1.5708rad)
  ScaleToSize = true
  Size = 10
  String = AS
  Tracking = 0
FEATURE [PartDesign::Pocket] Pocket012
  BaseFeature = -> Pocket011
  Direction = (0,1,0)
  Length = 1
  Length2 = 5
  Profile = -> ShapeString
  ReferenceAxis = -> ShapeString [N_Axis]
  Refine = true
  Suppressed = false
  Type = 0
FEATURE [PartDesign::Body] Body007  label="lato DX"
  AllowCompound = false
  Group = -> [Binder001,Sketch114,Pad011,Chamfer014,Sketch115,Pocket006,Sketch116,Pad012,Sketch117,Pocket007,Sketch118,Pad013,Sketch119,Pocket008,Pad017,Chamfer009,Pocket009,Sketch123,Sketch120,Pad014,Pad018,Chamfer008,Pocket010,Sketch121,Pad015,Sketch122,Pad016,Sketch124,Sketch125,Sketch126,Sketch127,Sketch128,SubtractivePipe002,SubtractivePipe003,Sketch129,Sketch130,Clone2D001,Sketch131,SubtractiveLoft002,+11 more]
  Origin = -> Origin007
  Tip = -> Pocket012
FEATURE [Sketcher::SketchObject] Sketch133
  ArcFitTolerance = 1e-06
  AttachmentSupport = -> [Binder]
  ExternalGeometry = -> [Binder]
  FullyConstrained = true
  MakeInternals = false
  MapMode = 5
  Placement = pos=(0,9e-16,0) rot=(0,0.707107,0.707107;3.14159rad)
  sketch-geometry (30):
    g0: LineSegment StartX=0 StartY=39.2 StartZ=0 EndX=0 EndY=3.2 EndZ=0
    g1: LineSegment StartX=0 StartY=3.2 StartZ=0 EndX=82.8 EndY=3.2 EndZ=0
    g2: LineSegment StartX=82.8 StartY=3.2 StartZ=0 EndX=82.8 EndY=6.2 EndZ=0
    g3: LineSegment StartX=82.8 StartY=6.2 StartZ=0 EndX=91.752 EndY=6.2 EndZ=0
    g4: LineSegment StartX=0 StartY=39.2 StartZ=0 EndX=195.887 EndY=39.2 EndZ=0
    g5: LineSegment StartX=195.887 StartY=39.2 StartZ=0 EndX=202.765 EndY=20.303 EndZ=0
    g6: LineSegment StartX=192.333 StartY=24.9893 StartZ=0 EndX=196.467 EndY=26.4942 EndZ=0
    g7: LineSegment StartX=196.467 StartY=26.4942 StartZ=0 EndX=194.073 EndY=33.0721 EndZ=0
    g8: LineSegment StartX=194.073 StartY=33.0721 StartZ=0 EndX=189.939 EndY=31.5672 EndZ=0
    g9: LineSegment StartX=189.939 StartY=31.5672 StartZ=0 EndX=192.333 EndY=24.9893 EndZ=0
    g10: ArcOfCircle CenterX=107.6 CenterY=4 CenterZ=0 NormalX=0 NormalY=0 NormalZ=1 AngleXU=0 Radius=16 StartAngle=1.5708 EndAngle=3.00366
    g11: LineSegment StartX=107.6 StartY=20 StartZ=0 EndX=132.428 EndY=20 EndZ=0
    g12: ArcOfCircle [constr] CenterX=132.428 CenterY=4 CenterZ=0 NormalX=0 NormalY=0 NormalZ=1 AngleXU=0 Radius=16 StartAngle=0.314159 EndAngle=1.5708
    g13: LineSegment StartX=147.645 StartY=8.94427 StartZ=0 EndX=176.685 EndY=-80.4316 EndZ=0
    g14: LineSegment StartX=176.685 StartY=-80.4316 StartZ=0 EndX=215.932 EndY=-80.4316 EndZ=0
    g15: ArcOfCircle CenterX=207.583 CenterY=4 CenterZ=0 NormalX=0 NormalY=0 NormalZ=1 AngleXU=0 Radius=17 StartAngle=1.85815 EndAngle=3.57792
    g16: ArcOfCircle CenterX=184.801 CenterY=-67.3089 CenterZ=0 NormalX=0 NormalY=0 NormalZ=1 AngleXU=0 Radius=33.7833 StartAngle=5.88425 EndAngle=6.71952
    g17: LineSegment StartX=192.176 StartY=-3.18451 StartZ=0 EndX=215.42 EndY=-53.0314 EndZ=0
    g18: Circle CenterX=5.6 CenterY=34.8 CenterZ=0 NormalX=0 NormalY=0 NormalZ=1 AngleXU=0 Radius=1.8
    g19: Circle CenterX=5.6 CenterY=7.6 CenterZ=0 NormalX=0 NormalY=0 NormalZ=1 AngleXU=0 Radius=1.8
    g20: Circle CenterX=78.51 CenterY=34.8 CenterZ=0 NormalX=0 NormalY=0 NormalZ=1 AngleXU=0 Radius=1.8
    g21: Circle CenterX=78.51 CenterY=7.6 CenterZ=0 NormalX=0 NormalY=0 NormalZ=1 AngleXU=0 Radius=1.8
    g22: Circle CenterX=184.08 CenterY=34.8 CenterZ=0 NormalX=0 NormalY=0 NormalZ=1 AngleXU=0 Radius=1.8
    g23: Circle CenterX=179.305 CenterY=-76.8316 CenterZ=0 NormalX=0 NormalY=0 NormalZ=1 AngleXU=0 Radius=1.8
    g24: Circle CenterX=213.443 CenterY=-76.8316 CenterZ=0 NormalX=0 NormalY=0 NormalZ=1 AngleXU=0 Radius=1.8
    g25: Circle CenterX=19 CenterY=21.2 CenterZ=0 NormalX=0 NormalY=0 NormalZ=1 AngleXU=0 Radius=6.3
    g26: Circle CenterX=42 CenterY=21.2 CenterZ=0 NormalX=0 NormalY=0 NormalZ=1 AngleXU=0 Radius=6.3
    g27: Circle CenterX=65 CenterY=21.2 CenterZ=0 NormalX=0 NormalY=0 NormalZ=1 AngleXU=0 Radius=6.3
    g28: LineSegment StartX=132.428 StartY=20 StartZ=0 EndX=144.053 EndY=20 EndZ=0
    g29: LineSegment StartX=147.645 StartY=8.94427 StartZ=0 EndX=144.053 EndY=20 EndZ=0
  constraints (65):
    c: Coincident(g0,g-4)
    c: Coincident(g0,g-5)
    c: Coincident(g1,g0)
    c: Coincident(g1,g-6)
    c: Coincident(g2,g1)
    c: Coincident(g2,g-7)
    c: Coincident(g3,g2)
    c: Coincident(g3,g-8)
    c: Coincident(g4,g0)
    c: Coincident(g4,g-16)
    c: Coincident(g5,g4)
    c: Coincident(g5,g-16)
    c: Coincident(g6,g-20)
    c: Coincident(g6,g-21)
    c: Coincident(g7,g6)
    c: Coincident(g7,g-23)
    c: Coincident(g8,g7)
    c: Coincident(g8,g-22)
    c: Coincident(g9,g8)
    c: Coincident(g9,g6)
    c: Equal(g10,g-8)
    c: Coincident(g10,g3)
    c: Coincident(g10,g-9)
    c: Coincident(g11,g10)
    c: Coincident(g11,g-10)
    c: Equal(g12,g-10)
    c: Coincident(g12,g11)
    c: Coincident(g12,g-11)
    c: Coincident(g13,g12)
    c: Coincident(g13,g-12)
    c: Coincident(g14,g13)
    c: Coincident(g14,g-13)
    c: Equal(g15,g-15)
    c: Coincident(g15,g5)
    c: Coincident(g15,g-15)
    c: Equal(g16,g-13)
    c: Coincident(g16,g14)
    c: Coincident(g16,g-14)
    c: Coincident(g17,g15)
    c: Coincident(g17,g16)
    c: Equal(g18,g-28)
    c: Equal(g19,g-29)
    c: Equal(g20,g-26)
    c: Equal(g21,g-27)
    c: Equal(g22,g-17)
    c: Equal(g24,g-25)
    c: Equal(g23,g-24)
    c: Coincident(g23,g-24)
    c: Coincident(g24,g-25)
    c: Coincident(g22,g-17)
    c: Coincident(g20,g-26)
    c: Coincident(g21,g-27)
    c: Coincident(g18,g-28)
    c: Coincident(g19,g-29)
    c: Equal(g25,g-30)
    c: Equal(g26,g-31)
    c: Equal(g27,g-32)
    c: Coincident(g25,g-30)
    c: Coincident(g26,g-31)
    c: Coincident(g27,g-32)
    c: Parallel(g28,g11)
    c: Parallel(g29,g13)
    c: Coincident(g28,g11)
    c: Coincident(g29,g12)
    c: Coincident(g29,g28)
FEATURE [PartDesign::Pad] Pad019
  Direction = (0,1,-2e-16)
  Length = 2
  Length2 = 10
  Profile = -> Sketch133
  ReferenceAxis = -> Sketch133 [N_Axis]
  Refine = true
  Suppressed = false
  Type = 0
FEATURE [Sketcher::SketchObject] Sketch091  label="Sketch091 - forma anteriore"
  ArcFitTolerance = 1e-06
  AttachmentSupport = -> [Pad019]
  ExternalGeometry = -> [Binder]
  FullyConstrained = true
  MakeInternals = false
  MapMode = 5
  Placement = pos=(0,2,0) rot=(0,0.707107,0.707107;3.14159rad)
  sketch-geometry (12):
    g0: Circle CenterX=5.6 CenterY=34.8 CenterZ=0 NormalX=0 NormalY=0 NormalZ=1 AngleXU=0 Radius=1.8
    g1: Circle CenterX=5.6 CenterY=7.6 CenterZ=0 NormalX=0 NormalY=0 NormalZ=1 AngleXU=0 Radius=1.8
    g2: Circle CenterX=78.51 CenterY=34.8 CenterZ=0 NormalX=0 NormalY=0 NormalZ=1 AngleXU=0 Radius=1.8
    g3: Circle CenterX=78.51 CenterY=7.6 CenterZ=0 NormalX=0 NormalY=0 NormalZ=1 AngleXU=0 Radius=1.8
    g4: LineSegment StartX=0 StartY=39.2 StartZ=0 EndX=0 EndY=3.2 EndZ=0
    g5: LineSegment StartX=0 StartY=3.2 StartZ=0 EndX=82.8 EndY=3.2 EndZ=0
    g6: LineSegment StartX=82.8 StartY=3.2 StartZ=0 EndX=82.8 EndY=39.2 EndZ=0
    g7: LineSegment StartX=82.8 StartY=39.2 StartZ=0 EndX=0 EndY=39.2 EndZ=0
    g8: ArcOfCircle CenterX=19 CenterY=21.2 CenterZ=0 NormalX=0 NormalY=0 NormalZ=1 AngleXU=0 Radius=10 StartAngle=1.5708 EndAngle=4.71239
    g9: ArcOfCircle CenterX=65 CenterY=21.2 CenterZ=0 NormalX=0 NormalY=0 NormalZ=1 AngleXU=0 Radius=10 StartAngle=4.71239 EndAngle=7.85398
    g10: LineSegment StartX=19 StartY=31.2 StartZ=0 EndX=65 EndY=31.2 EndZ=0
    g11: LineSegment StartX=19 StartY=11.2 StartZ=0 EndX=65 EndY=11.2 EndZ=0
  constraints (25):
    c: Equal(g2,g-7)
    c: Equal(g3,g-8)
    c: Equal(g1,g-13)
    c: Equal(g0,g-12)
    c: Coincident(g0,g-12)
    c: Coincident(g1,g-13)
    c: Coincident(g3,g-8)
    c: Coincident(g2,g-7)
    c: Coincident(g4,g-4)
    c: Coincident(g4,g-5)
    c: Coincident(g5,g4)
    c: Coincident(g5,g-6)
    c: Coincident(g6,g5)
    c: PointOnObject(g6,g-3)
    c: Vertical(g6)
    c: Coincident(g7,g6)
    c: Coincident(g7,g4)
    c: Tangent(g8,g10) = 1.5708
    c: Tangent(g8,g11) = -1.5708
    c: Tangent(g9,g10) = 1.5708
    c: Tangent(g9,g11) = -1.5708
    c: Equal(g8,g9)
    c: Radius(g8) = 10
    c: Coincident(g8,g-11)
    c: Coincident(g9,g-9)
FEATURE [Sketcher::SketchObject] Sketch093  label="Sketch093 - scavi interni pulsanti"
  ArcFitTolerance = 1e-06
  AttachmentSupport = -> [Pad019]
  ExternalGeometry = -> [Binder]
  FullyConstrained = true
  MakeInternals = false
  MapMode = 5
  Placement = pos=(0,1.8e-15,0) rot=(1,0,0;1.5708rad)
  sketch-geometry (3):
    g0: Circle CenterX=-65 CenterY=21.2 CenterZ=0 NormalX=0 NormalY=0 NormalZ=1 AngleXU=0 Radius=7.3
    g1: Circle CenterX=-42 CenterY=21.2 CenterZ=0 NormalX=0 NormalY=0 NormalZ=1 AngleXU=0 Radius=7.3
    g2: Circle CenterX=-19 CenterY=21.2 CenterZ=0 NormalX=0 NormalY=0 NormalZ=1 AngleXU=0 Radius=7.3
  constraints (6):
    c: Coincident(g0,g-3)
    c: Coincident(g1,g-4)
    c: Coincident(g2,g-5)
    c: Diameter(g0) = 14.6
    c: Diameter(g1) = 14.6
    c: Diameter(g2) = 14.6
FEATURE [Sketcher::SketchObject] Sketch094  label="Sketch094 - forma centrale"
  ArcFitTolerance = 1e-06
  AttachmentSupport = -> [Pad019]
  ExternalGeometry = -> [Binder]
  FullyConstrained = true
  MakeInternals = false
  MapMode = 5
  Placement = pos=(0,2,0) rot=(0,0.707107,0.707107;3.14159rad)
  sketch-geometry (4):
    g0: LineSegment StartX=137.815 StartY=39.2 StartZ=0 EndX=142.655 EndY=24.303 EndZ=0
    g1: LineSegment StartX=110.815 StartY=24.303 StartZ=0 EndX=142.655 EndY=24.303 EndZ=0
    g2: LineSegment StartX=137.815 StartY=39.2 StartZ=0 EndX=110.815 EndY=39.2 EndZ=0
    g3: ArcOfCircle CenterX=92.2534 CenterY=31.7515 CenterZ=0 NormalX=0 NormalY=0 NormalZ=1 AngleXU=0 Radius=20 StartAngle=5.90156 EndAngle=6.66481
  constraints (12):
    c: PointOnObject(g0,g-3)
    c: Tangent(g0,g-5)
    c: Horizontal(g1)
    c: Coincident(g1,g0)
    c: Coincident(g2,g0)
    c: PointOnObject(g2,g-3)
    c: DistanceX(g2,g2) = 27
    c: Vertical(g1,g2)
    c: Coincident(g3,g2)
    c: Radius(g3) = 20
    c: Coincident(g3,g1)
    c: DistanceY(g-6,g0) = 4
FEATURE [Sketcher::SketchObject] Sketch095  label="Sketch095 - forma posteriore"
  ArcFitTolerance = 1e-06
  AttachmentSupport = -> [Pad019]
  ExternalGeometry = -> [Binder]
  FullyConstrained = true
  MakeInternals = false
  MapMode = 5
  Placement = pos=(0,2,0) rot=(0,0.707107,0.707107;3.14159rad)
  sketch-geometry (15):
    g0: LineSegment StartX=137.815 StartY=39.2 StartZ=0 EndX=143.955 EndY=20.303 EndZ=0
    g1: LineSegment StartX=143.955 StartY=20.303 StartZ=0 EndX=190.141 EndY=20.303 EndZ=0
    g2: ArcOfCircle CenterX=184.08 CenterY=34.8 CenterZ=0 NormalX=0 NormalY=0 NormalZ=1 AngleXU=0 Radius=3.5 StartAngle=3.49066 EndAngle=4.71239
    g3: LineSegment StartX=180.791 StartY=33.6029 StartZ=0 EndX=178.754 EndY=39.2 EndZ=0
    g4: LineSegment StartX=184.08 StartY=31.3 StartZ=0 EndX=186.139 EndY=31.3 EndZ=0
    g5: LineSegment StartX=190.141 StartY=20.303 StartZ=0 EndX=186.139 EndY=31.3 EndZ=0
    g6: LineSegment StartX=137.815 StartY=39.2 StartZ=0 EndX=156.815 EndY=39.2 EndZ=0
    g7: LineSegment StartX=178.754 StartY=39.2 StartZ=0 EndX=168.815 EndY=39.2 EndZ=0
    g8: LineSegment StartX=156.815 StartY=31.2 StartZ=0 EndX=168.815 EndY=31.2 EndZ=0
    g9: ArcOfCircle CenterX=176.411 CenterY=35.2 CenterZ=0 NormalX=0 NormalY=0 NormalZ=1 AngleXU=0 Radius=20 StartAngle=2.94023 EndAngle=3.34295
    g10: ArcOfCircle CenterX=188.411 CenterY=35.2 CenterZ=0 NormalX=0 NormalY=0 NormalZ=1 AngleXU=0 Radius=20 StartAngle=2.94023 EndAngle=3.34295
    g11: LineSegment StartX=157.815 StartY=39.2 StartZ=0 EndX=167.815 EndY=39.2 EndZ=0
    g12: LineSegment StartX=157.436 StartY=36.2 StartZ=0 EndX=167.436 EndY=36.2 EndZ=0
    g13: ArcOfCircle CenterX=177.411 CenterY=35.2 CenterZ=0 NormalX=0 NormalY=0 NormalZ=1 AngleXU=0 Radius=20 StartAngle=2.94023 EndAngle=3.09157
    g14: ArcOfCircle CenterX=187.411 CenterY=35.2 CenterZ=0 NormalX=0 NormalY=0 NormalZ=1 AngleXU=0 Radius=20 StartAngle=2.94023 EndAngle=3.09157
  constraints (46):
    c: PointOnObject(g0,g-3)
    c: Tangent(g0,g-6)
    c: Coincident(g1,g0)
    c: Horizontal(g1)
    c: Radius(g2) = 3.5
    c: Coincident(g2,g-5)
    c: PointOnObject(g3,g-3)
    c: Parallel(g3,g-4)
    c: Tangent(g3,g2) = 1.5708
    c: Horizontal(g4)
    c: Tangent(g4,g2) = -1.5708
    c: Coincident(g5,g1)
    c: Parallel(g5,g-4)
    c: Coincident(g5,g4)
    c: DistanceX(g4,g-8) = 3.8
    c: Coincident(g6,g0)
    c: PointOnObject(g6,g-3)
    c: Coincident(g7,g3)
    c: PointOnObject(g7,g-3)
    c: Horizontal(g8)
    c: DistanceX(g6,g7) = 12
    c: Vertical(g8,g6)
    c: Vertical(g7,g8)
    c: DistanceY(g8,g6) = 8
    c: Coincident(g9,g8)
    c: Coincident(g9,g6)
    c: Coincident(g10,g7)
    c: Coincident(g10,g8)
    c: Radius(g9) = 20
    c: Radius(g10) = 20
    c: PointOnObject(g11,g-3)
    c: PointOnObject(g11,g-3)
    c: DistanceX(g11,g11) = 10
    c: DistanceX(g6,g11) = 1
    c: Horizontal(g12)
    c: Equal(g12,g11)
    c: DistanceY(g12,g11) = 3
    c: Coincident(g13,g11)
    c: Coincident(g13,g12)
    c: Radius(g13) = 20
    c: Coincident(g14,g11)
    c: Coincident(g14,g12)
    c: Radius(g14) = 20
    c: DistanceX(g0,g6) = 19
    c: Horizontal(g9,g13)
    c: Horizontal(g0,g-4)
FEATURE [Sketcher::SketchObject] Sketch096  label="Sketch096 - forma impugnatura"
  ArcFitTolerance = 1e-06
  AttachmentSupport = -> [Pad019]
  ExternalGeometry = -> [Binder]
  FullyConstrained = true
  MakeInternals = false
  MapMode = 5
  Placement = pos=(0,2,0) rot=(0,0.707107,0.707107;3.14159rad)
  sketch-geometry (8):
    g0: LineSegment StartX=176.685 StartY=-80.4316 StartZ=0 EndX=143.955 EndY=20.303 EndZ=0
    g1: LineSegment StartX=176.685 StartY=-80.4316 StartZ=0 EndX=215.932 EndY=-80.4316 EndZ=0
    g2: Circle CenterX=179.305 CenterY=-76.8316 CenterZ=0 NormalX=0 NormalY=0 NormalZ=1 AngleXU=0 Radius=3
    g3: Circle CenterX=213.443 CenterY=-76.8316 CenterZ=0 NormalX=0 NormalY=0 NormalZ=1 AngleXU=0 Radius=3
    g4: LineSegment StartX=143.955 StartY=20.303 StartZ=0 EndX=202.765 EndY=20.303 EndZ=0
    g5: LineSegment StartX=215.42 StartY=-53.0314 StartZ=0 EndX=192.176 EndY=-3.18451 EndZ=0
    g6: ArcOfCircle CenterX=184.801 CenterY=-67.3089 CenterZ=0 NormalX=0 NormalY=0 NormalZ=1 AngleXU=0 Radius=33.7833 StartAngle=5.88425 EndAngle=6.71952
    g7: ArcOfCircle CenterX=207.583 CenterY=4 CenterZ=0 NormalX=0 NormalY=0 NormalZ=1 AngleXU=0 Radius=17 StartAngle=1.85815 EndAngle=3.57792
  constraints (19):
    c: Coincident(g0,g-4)
    c: PointOnObject(g0,g-3)
    c: Horizontal(g0,g-7)
    c: Coincident(g1,g0)
    c: Coincident(g1,g-5)
    c: Diameter(g2) = 6
    c: Diameter(g3) = 6
    c: Coincident(g2,g-9)
    c: Coincident(g3,g-10)
    c: Coincident(g4,g0)
    c: Coincident(g5,g-6)
    c: Coincident(g6,g1)
    c: Coincident(g6,g5)
    c: Equal(g-5,g6)
    c: Coincident(g5,g-7)
    c: Coincident(g4,g-7)
    c: Tangent(g7,g-7)
    c: Coincident(g7,g4)
    c: Coincident(g7,g5)
FEATURE [Sketcher::SketchObject] Sketch097
  ArcFitTolerance = 1e-06
  AttachmentSupport = -> [Pad019]
  ExternalGeometry = -> [Binder]
  FullyConstrained = true
  MakeInternals = false
  MapMode = 5
  Placement = pos=(0,2,0) rot=(0,0.707107,0.707107;3.14159rad)
  sketch-geometry (4):
    g0: LineSegment StartX=90 StartY=36.8 StartZ=0 EndX=108 EndY=36.8 EndZ=0
    g1: LineSegment StartX=108 StartY=36.8 StartZ=0 EndX=108 EndY=26.8 EndZ=0
    g2: LineSegment StartX=108 StartY=26.8 StartZ=0 EndX=90 EndY=26.8 EndZ=0
    g3: ArcOfCircle CenterX=94 CenterY=31.8 CenterZ=0 NormalX=0 NormalY=0 NormalZ=1 AngleXU=0 Radius=6.40312 StartAngle=2.24554 EndAngle=4.03765
  constraints (13):
    c: Horizontal(g0)
    c: Coincident(g1,g0)
    c: Vertical(g1)
    c: DistanceX(g0,g0) = 18
    c: DistanceY(g1,g1) = 10
    c: Coincident(g2,g1)
    c: Horizontal(g2)
    c: Equal(g2,g0)
    c: DistanceY(g0,g-3) = 2.4
    c: Coincident(g3,g0)
    c: Coincident(g3,g2)
    c: DistanceX(g2,g3) = 4
    c: DistanceX(g-3,g0) = 90
FEATURE [PartDesign::Chamfer] Chamfer015
  Angle = 45
  Base = -> Pad019 [Edge19,Edge22,Edge79]
  BaseFeature = -> Pad019
  ChamferType = 0
  FlipDirection = false
  Refine = true
  Size = 1.9
  Size2 = 1
  SupportTransform = false
  Suppressed = false
  UseAllEdges = false
FEATURE [PartDesign::Pocket] Pocket002
  BaseFeature = -> Chamfer015
  Direction = (0,1,-2e-16)
  Length = 1.2
  Length2 = 5
  Profile = -> Sketch093
  ReferenceAxis = -> Sketch093 [N_Axis]
  Refine = true
  Suppressed = false
  Type = 0
FEATURE [PartDesign::Pad] Pad005
  BaseFeature = -> Pocket002
  Direction = (0,1,-2e-16)
  Length = 1.6
  Length2 = 10
  Profile = -> Sketch091
  ReferenceAxis = -> Sketch091 [N_Axis]
  Refine = true
  Suppressed = false
  Type = 0
FEATURE [Sketcher::SketchObject] Sketch092  label="Sketch092 - scavi per viti anteriori"
  ArcFitTolerance = 1e-06
  AttachmentSupport = -> [Pad005]
  ExternalGeometry = -> [Binder]
  FullyConstrained = true
  MakeInternals = false
  MapMode = 5
  Placement = pos=(0,3.6,0) rot=(0,0.707107,0.707107;3.14159rad)
  sketch-geometry (20):
    g0: ArcOfCircle CenterX=5.6 CenterY=7.6 CenterZ=0 NormalX=0 NormalY=0 NormalZ=1 AngleXU=0 Radius=3.5 StartAngle=0 EndAngle=1.5708
    g1: ArcOfCircle CenterX=5.6 CenterY=34.8 CenterZ=0 NormalX=0 NormalY=0 NormalZ=1 AngleXU=0 Radius=3.5 StartAngle=4.71239 EndAngle=6.28319
    g2: ArcOfCircle CenterX=78.51 CenterY=34.8 CenterZ=0 NormalX=0 NormalY=0 NormalZ=1 AngleXU=0 Radius=3.5 StartAngle=3.14159 EndAngle=4.71239
    g3: ArcOfCircle CenterX=78.51 CenterY=7.6 CenterZ=0 NormalX=0 NormalY=0 NormalZ=1 AngleXU=0 Radius=3.5 StartAngle=1.5708 EndAngle=3.14159
    g4: LineSegment StartX=0 StartY=3.2 StartZ=0 EndX=0 EndY=11.1 EndZ=0
    g5: LineSegment StartX=0 StartY=11.1 StartZ=0 EndX=5.6 EndY=11.1 EndZ=0
    g6: LineSegment StartX=0 StartY=3.2 StartZ=0 EndX=9.1 EndY=3.2 EndZ=0
    g7: LineSegment StartX=9.1 StartY=3.2 StartZ=0 EndX=9.1 EndY=7.6 EndZ=0
    g8: LineSegment StartX=0 StartY=39.2 StartZ=0 EndX=0 EndY=31.3 EndZ=0
    g9: LineSegment StartX=0 StartY=31.3 StartZ=0 EndX=5.6 EndY=31.3 EndZ=0
    g10: LineSegment StartX=0 StartY=39.2 StartZ=0 EndX=9.1 EndY=39.2 EndZ=0
    g11: LineSegment StartX=9.1 StartY=39.2 StartZ=0 EndX=9.1 EndY=34.8 EndZ=0
    g12: LineSegment StartX=82.8 StartY=39.2 StartZ=0 EndX=75.01 EndY=39.2 EndZ=0
    g13: LineSegment StartX=82.8 StartY=39.2 StartZ=0 EndX=82.8 EndY=31.3 EndZ=0
    g14: LineSegment StartX=82.8 StartY=31.3 StartZ=0 EndX=78.51 EndY=31.3 EndZ=0
    g15: LineSegment StartX=82.8 StartY=3.2 StartZ=0 EndX=75.01 EndY=3.2 EndZ=0
    g16: LineSegment StartX=75.01 StartY=3.2 StartZ=0 EndX=75.01 EndY=7.6 EndZ=0
    g17: LineSegment StartX=82.8 StartY=3.2 StartZ=0 EndX=82.8 EndY=11.1 EndZ=0
    g18: LineSegment StartX=82.8 StartY=11.1 StartZ=0 EndX=78.51 EndY=11.1 EndZ=0
    g19: LineSegment StartX=75.01 StartY=39.2 StartZ=0 EndX=75.01 EndY=34.8 EndZ=0
  constraints (48):
    c: Radius(g0) = 3.5
    c: Coincident(g0,g-10)
    c: Radius(g1) = 3.5
    c: Coincident(g1,g-9)
    c: Radius(g2) = 3.5
    c: Coincident(g2,g-8)
    c: Radius(g3) = 3.5
    c: Coincident(g3,g-7)
    c: Coincident(g4,g-5)
    c: PointOnObject(g4,g-4)
    c: Coincident(g5,g4)
    c: Horizontal(g5)
    c: Coincident(g6,g4)
    c: PointOnObject(g6,g-5)
    c: Coincident(g7,g6)
    c: Vertical(g7)
    c: Coincident(g8,g-4)
    c: PointOnObject(g8,g-4)
    c: Coincident(g9,g8)
    c: Horizontal(g9)
    c: Coincident(g10,g8)
    c: PointOnObject(g10,g-3)
    c: Coincident(g11,g10)
    c: Vertical(g11)
    c: PointOnObject(g12,g-3)
    c: PointOnObject(g12,g-3)
    c: Coincident(g13,g12)
    c: Vertical(g13)
    c: Coincident(g14,g13)
    c: Horizontal(g14)
    c: Coincident(g15,g-6)
    c: PointOnObject(g15,g-5)
    c: Coincident(g16,g15)
    c: Vertical(g16)
    c: Coincident(g17,g15)
    c: Coincident(g18,g17)
    c: Horizontal(g18)
    c: Tangent(g3,g18) = -1.5708
    c: Tangent(g16,g3) = 1.5708
    c: Coincident(g19,g12)
    c: Vertical(g19)
    c: Tangent(g2,g19) = -1.5708
    c: Tangent(g2,g14) = 1.5708
    c: Tangent(g0,g7) = -1.5708
    c: Tangent(g0,g5) = 1.5708
    c: Tangent(g9,g1) = -1.5708
    c: Tangent(g1,g11) = 1.5708
    c: Tangent(g17,g13)
FEATURE [PartDesign::Pocket] Pocket001
  BaseFeature = -> Pad005
  Direction = (0,-1,2e-16)
  Length = 1.6
  Length2 = 5
  Profile = -> Sketch092
  ReferenceAxis = -> Sketch092 [N_Axis]
  Refine = true
  Suppressed = false
  Type = 0
FEATURE [PartDesign::Pad] Pad006
  BaseFeature = -> Pocket001
  Direction = (0,1,-2e-16)
  Length = 0.8
  Length2 = 10
  Profile = -> Sketch094
  ReferenceAxis = -> Sketch094 [N_Axis]
  Refine = true
  Suppressed = false
  Type = 0
FEATURE [PartDesign::Pad] Pad007
  BaseFeature = -> Pad006
  Direction = (0,1,-2e-16)
  Length = 2
  Length2 = 10
  Profile = -> Sketch095
  ReferenceAxis = -> Sketch095 [N_Axis]
  Refine = true
  Suppressed = false
  Type = 0
FEATURE [PartDesign::Pad] Pad008  label="Pad008 - forma impugnatura"
  BaseFeature = -> Pad007
  Direction = (0,1,-2e-16)
  Length = 1.6
  Length2 = 10
  Profile = -> Sketch096
  ReferenceAxis = -> Sketch096 [N_Axis]
  Refine = true
  Suppressed = false
  Type = 0
FEATURE [PartDesign::Pad] Pad009
  BaseFeature = -> Pad008
  Direction = (0,1,-2e-16)
  Length = 1.6
  Length2 = 10
  Profile = -> Sketch097
  ReferenceAxis = -> Sketch097 [N_Axis]
  Refine = true
  Suppressed = false
  Type = 0
FEATURE [Sketcher::SketchObject] Sketch098
  ArcFitTolerance = 1e-06
  AttachmentSupport = -> [Pad006]
  ExternalGeometry = -> [Binder]
  FullyConstrained = true
  MakeInternals = false
  MapMode = 5
  Placement = pos=(0,2.8,-7e-16) rot=(0,0.707107,0.707107;3.14159rad)
  sketch-geometry (4):
    g0: LineSegment StartX=118 StartY=39.2 StartZ=0 EndX=129 EndY=39.2 EndZ=0
    g1: LineSegment StartX=120.599 StartY=31.2 StartZ=0 EndX=131.599 EndY=31.2 EndZ=0
    g2: LineSegment StartX=129 StartY=39.2 StartZ=0 EndX=131.599 EndY=31.2 EndZ=0
    g3: LineSegment StartX=118 StartY=39.2 StartZ=0 EndX=120.599 EndY=31.2 EndZ=0
  constraints (12):
    c: PointOnObject(g0,g-3)
    c: PointOnObject(g0,g-3)
    c: DistanceX(g0,g0) = 11
    c: Horizontal(g1)
    c: Equal(g1,g0)
    c: Coincident(g2,g0)
    c: Coincident(g3,g0)
    c: Parallel(g-4,g2)
    c: Coincident(g1,g2)
    c: Coincident(g1,g3)
    c: DistanceY(g1,g0) = 8
    c: DistanceX(g-3,g0) = 118
FEATURE [Sketcher::SketchObject] Sketch099
  ArcFitTolerance = 1e-06
  AttachmentSupport = -> [Pad008]
  ExternalGeometry = -> [Binder]
  FullyConstrained = true
  MakeInternals = false
  MapMode = 5
  Placement = pos=(0,3.6,0) rot=(0,0.707107,0.707107;3.14159rad)
  sketch-geometry (13):
    g0: LineSegment StartX=192.176 StartY=-3.18451 StartZ=0 EndX=196.804 EndY=-13.1108 EndZ=0
    g1: LineSegment [constr] StartX=202.765 StartY=20.303 StartZ=0 EndX=181.223 EndY=20.303 EndZ=0
    g2: LineSegment [constr] StartX=181.223 StartY=20.303 StartZ=0 EndX=181.223 EndY=-3.18451 EndZ=0
    g3: ArcOfCircle CenterX=181.223 CenterY=-20.3764 CenterZ=0 NormalX=0 NormalY=0 NormalZ=1 AngleXU=0 Radius=17.1918 StartAngle=0.436332 EndAngle=1.57079
    g4: ArcOfEllipse CenterX=181.223 CenterY=8.55923 CenterZ=0 NormalX=0 NormalY=0 NormalZ=1 MajorRadius=23.4779 MinorRadius=11.7437 AngleXU=0 StartAngle=1.5708 EndAngle=4.71239
    g5: LineSegment [constr] StartX=204.701 StartY=8.55923 StartZ=0 EndX=157.745 EndY=8.55923 EndZ=0
    g6: LineSegment [constr] StartX=181.223 StartY=20.303 StartZ=0 EndX=181.223 EndY=-3.18451 EndZ=0
    g7: GeomPoint [constr] X=201.553 Y=8.55923 Z=0
    g8: GeomPoint [constr] X=160.894 Y=8.55923 Z=0
    g9: GeomPoint [constr] X=181.223 Y=-3.18451 Z=0
    g10: LineSegment StartX=181.223 StartY=20.303 StartZ=0 EndX=202.765 EndY=20.303 EndZ=0
    g11: ArcOfCircle CenterX=207.583 CenterY=4 CenterZ=0 NormalX=0 NormalY=0 NormalZ=1 AngleXU=0 Radius=17 StartAngle=1.85815 EndAngle=3.57792
    g12: LineSegment [constr] StartX=172.411 StartY=39.2 StartZ=0 EndX=192.176 EndY=-3.18451 EndZ=0
  constraints (27):
    c: Coincident(g1,g-7)
    c: Horizontal(g1)
    c: Coincident(g2,g1)
    c: Vertical(g2)
    c: Horizontal(g2,g0)
    c: Coincident(g3,g0)
    c: Coincident(g3,g2)
    c: InternalAlignment(g5-g8 -> g4) x4
    c: Horizontal(g5)
    c: PointOnObject(g4,g2)
    c: Coincident(g4,g1)
    c: DistanceX(g-3,g5) = 10.1
    c: Coincident(g4,g2)
    c: Tangent(g3,g-5)
    c: PointOnObject(g9,g4)
    c: PointOnObject(g9,g3)
    c: Tangent(g4,g3,g9) = 1.5708
    c: Coincident(g10,g1)
    c: Coincident(g10,g1)
    c: Equal(g11,g-4)
    c: Coincident(g11,g1)
    c: Coincident(g11,g0)
    c: PointOnObject(g12,g-6)
    c: PointOnObject(g1,g12)
    c: Tangent(g12,g-5) = -1.5708
    c: Tangent(g0,g-5) = -1.5708
    c: Horizontal(g9,g12)
FEATURE [Sketcher::SketchObject] Sketch106  label="Sketch106 - smusso impuniatura interno"
  ArcFitTolerance = 1e-06
  AttachmentSupport = -> [Pad008]
  ExternalGeometry = -> [Pad008]
  FullyConstrained = true
  MakeInternals = false
  MapMode = 5
  Placement = pos=(0,-1.586e-13,-80.4316) rot=(1,0,0;3.14159rad)
  sketch-geometry (9):
    g0: LineSegment StartX=-176.685 StartY=-3.6 StartZ=0 EndX=-176.685 EndY=2.12528e-11 EndZ=0
    g1: LineSegment [constr] StartX=-176.685 StartY=1.79e-14 StartZ=0 EndX=-176.685 EndY=2.12527e-11 EndZ=0
    g2: LineSegment [constr] StartX=-186.685 StartY=-3.6 StartZ=0 EndX=-186.685 EndY=2.12528e-11 EndZ=0
    g3: ArcOfEllipse CenterX=-186.685 CenterY=2.12527e-11 CenterZ=0 NormalX=0 NormalY=0 NormalZ=1 MajorRadius=10 MinorRadius=3.6 AngleXU=-3.14159 StartAngle=1.5708 EndAngle=3.14159
    g4: LineSegment [constr] StartX=-196.685 StartY=1.79e-14 StartZ=0 EndX=-176.685 EndY=1.79e-14 EndZ=0
    g5: LineSegment [constr] StartX=-186.685 StartY=-3.6 StartZ=0 EndX=-186.685 EndY=3.6 EndZ=0
    g6: GeomPoint [constr] X=-196.015 Y=1.55e-14 Z=0
    g7: GeomPoint [constr] X=-177.356 Y=1.85e-14 Z=0
    g8: LineSegment StartX=-176.685 StartY=-3.6 StartZ=0 EndX=-186.685 EndY=-3.6 EndZ=0
  constraints (15):
    c: PointOnObject(g2,g-3)
    c: Coincident(g1,g-5)
    c: DistanceY(g1,g1) = 0
    c: Coincident(g0,g1)
    c: DistanceX(g2,g-5) = 10
    c: Vertical(g2)
    c: Horizontal(g2,g0)
    c: InternalAlignment(g4-g7 -> g3) x4
    c: Coincident(g3,g2)
    c: Horizontal(g4)
    c: Coincident(g3,g0)
    c: Tangent(g0,g-5) = 1.5708
    c: Coincident(g3,g2)
    c: Coincident(g8,g0)
    c: Coincident(g8,g2)
FEATURE [Sketcher::SketchObject] Sketch107  label="Sketch107 - smusso impugnatura esterno"
  ArcFitTolerance = 1e-06
  AttachmentSupport = -> [Pad008]
  ExternalGeometry = -> [Pad008]
  FullyConstrained = true
  MakeInternals = false
  MapMode = 5
  Placement = pos=(0,-1.586e-13,-80.4316) rot=(1,0,0;3.14159rad)
  sketch-geometry (9):
    g0: LineSegment [constr] StartX=-215.932 StartY=1.79e-14 StartZ=0 EndX=-215.932 EndY=2.09e-14 EndZ=0
    g1: LineSegment StartX=-215.932 StartY=-3.6 StartZ=0 EndX=-215.932 EndY=2.09e-14 EndZ=0
    g2: LineSegment StartX=-215.932 StartY=-3.6 StartZ=0 EndX=-205.932 EndY=-3.6 EndZ=0
    g3: LineSegment [constr] StartX=-205.932 StartY=-3.6 StartZ=0 EndX=-205.932 EndY=2.09e-14 EndZ=0
    g4: ArcOfEllipse CenterX=-205.932 CenterY=2.09e-14 CenterZ=0 NormalX=0 NormalY=0 NormalZ=1 MajorRadius=10 MinorRadius=3.6 AngleXU=3.14159 StartAngle=1e-16 EndAngle=1.5708
    g5: LineSegment [constr] StartX=-215.932 StartY=1.79e-14 StartZ=0 EndX=-195.932 EndY=1.79e-14 EndZ=0
    g6: LineSegment [constr] StartX=-205.932 StartY=-3.6 StartZ=0 EndX=-205.932 EndY=3.6 EndZ=0
    g7: GeomPoint [constr] X=-215.262 Y=2.14e-14 Z=0
    g8: GeomPoint [constr] X=-196.602 Y=1.78e-14 Z=0
  constraints (16):
    c: Coincident(g0,g-6)
    c: PointOnObject(g0,g-6)
    c: DistanceY(g0,g0) = 0
    c: Coincident(g1,g-6)
    c: Coincident(g1,g0)
    c: Tangent(g2,g-3)
    c: DistanceX(g2,g2) = 10
    c: Coincident(g3,g2)
    c: Vertical(g3)
    c: Horizontal(g3,g0)
    c: InternalAlignment(g5-g8 -> g4) x4
    c: Coincident(g4,g3)
    c: Horizontal(g5)
    c: Coincident(g4,g0)
    c: Coincident(g4,g2)
    c: PointOnObject(g2,g1)
FEATURE [Sketcher::SketchObject] Sketch108
  ArcFitTolerance = 1e-06
  AttachmentOffset = pos=(0,0,-1.6) rot=(0,0,1;0rad)
  AttachmentSupport = -> [Pad008]
  ExternalGeometry = -> [Binder]
  FullyConstrained = true
  MakeInternals = false
  MapMode = 5
  Placement = pos=(0,2,4e-16) rot=(0,0.707107,0.707107;3.14159rad)
  sketch-geometry (14):
    g0: LineSegment StartX=192.176 StartY=-3.18451 StartZ=0 EndX=193.827 EndY=-6.72678 EndZ=0
    g1: LineSegment [constr] StartX=202.765 StartY=20.303 StartZ=0 EndX=181.223 EndY=20.303 EndZ=0
    g2: LineSegment [constr] StartX=181.223 StartY=20.303 StartZ=0 EndX=181.223 EndY=1.30297 EndZ=0
    g3: ArcOfCircle CenterX=181.223 CenterY=-12.6042 CenterZ=0 NormalX=0 NormalY=0 NormalZ=1 AngleXU=0 Radius=13.9072 StartAngle=0.436332 EndAngle=1.5708
    g4: ArcOfEllipse CenterX=181.223 CenterY=10.803 CenterZ=0 NormalX=0 NormalY=0 NormalZ=1 MajorRadius=14.4779 MinorRadius=9.5 AngleXU=0 StartAngle=1.5708 EndAngle=4.71239
    g5: LineSegment [constr] StartX=195.701 StartY=10.803 StartZ=0 EndX=166.745 EndY=10.803 EndZ=0
    g6: LineSegment [constr] StartX=181.223 StartY=20.303 StartZ=0 EndX=181.223 EndY=1.30297 EndZ=0
    g7: GeomPoint [constr] X=192.148 Y=10.803 Z=0
    g8: GeomPoint [constr] X=170.298 Y=10.803 Z=0
    g9: LineSegment StartX=181.223 StartY=20.303 StartZ=0 EndX=202.765 EndY=20.303 EndZ=0
    g10: ArcOfCircle CenterX=207.583 CenterY=4 CenterZ=0 NormalX=0 NormalY=0 NormalZ=1 AngleXU=0 Radius=17 StartAngle=1.85815 EndAngle=3.57792
    g11: LineSegment [constr] StartX=172.411 StartY=39.2 StartZ=0 EndX=192.176 EndY=-3.18451 EndZ=0
    g12: GeomPoint [constr] X=181.223 Y=1.30297 Z=0
    g13: GeomPoint [constr] X=181.223 Y=1.30297 Z=0
  constraints (28):
    c: Coincident(g1,g-7)
    c: Horizontal(g1)
    c: Coincident(g2,g1)
    c: Vertical(g2)
    c: Coincident(g3,g2)
    c: InternalAlignment(g5-g8 -> g4) x4
    c: Horizontal(g5)
    c: PointOnObject(g4,g2)
    c: Coincident(g4,g1)
    c: DistanceX(g-3,g5) = 19.1
    c: Coincident(g4,g2)
    c: Coincident(g9,g1)
    c: Coincident(g9,g1)
    c: Coincident(g10,g1)
    c: Coincident(g10,g0)
    c: PointOnObject(g11,g-6)
    c: PointOnObject(g1,g11)
    c: DistanceY(g2,g1) = 19
    c: Coincident(g10,g-4)
    c: PointOnObject(g12,g4)
    c: PointOnObject(g12,g3)
    c: Tangent(g11,g-5) = -1.5708
    c: Tangent(g0,g-5) = -1.5708
    c: Tangent(g3,g0) = 1.5708
    c: PointOnObject(g13,g4)
    c: PointOnObject(g13,g3)
    c: Tangent(g4,g3,g13) = 1.5708
    c: Horizontal(g11,g0)
FEATURE [Part::Part2DObjectPython] Clone2D  label="Sketch108 (2D)"  # Draft 2D object (typed FeaturePython)
  Fuse = false
  Objects = -> [Sketch108]
  Placement = pos=(0,2,4e-16) rot=(0,0.707107,0.707107;3.14159rad)
  Scale = (1,1,1)
FEATURE [Sketcher::SketchObject] Sketch109
  ArcFitTolerance = 1e-06
  AttachmentOffset = pos=(0,0,-3.5) rot=(0,0,1;0rad)
  AttachmentSupport = -> [Pad008]
  ExternalGeometry = -> [Binder]
  FullyConstrained = true
  MakeInternals = false
  MapMode = 5
  Placement = pos=(0,0.1,8e-16) rot=(0,0.707107,0.707107;3.14159rad)
  sketch-geometry (1):
    g0: GeomPoint X=197.47 Y=8.55923 Z=0
  constraints (1):
    c: Symmetric(g-7,g-5,g0)
FEATURE [PartDesign::Chamfer] Chamfer005
  Angle = 45
  Base = -> Pad009 [Edge215,Edge212]
  BaseFeature = -> Pad009
  ChamferType = 1
  FlipDirection = false
  Refine = true
  Size = 1.5
  Size2 = 2.8
  SupportTransform = false
  Suppressed = false
  UseAllEdges = false
FEATURE [Sketcher::SketchObject] Sketch111
  ArcFitTolerance = 1e-06
  AttachmentSupport = -> [Pad009]
  ExternalGeometry = -> [Pad009]
  FullyConstrained = true
  MakeInternals = false
  MapMode = 5
  Placement = pos=(0,3.6,-8e-16) rot=(0,0.707107,0.707107;3.14159rad)
  sketch-geometry (21):
    g0: LineSegment [constr] StartX=97 StartY=36.8 StartZ=0 EndX=97 EndY=26.8 EndZ=0
    g1: LineSegment StartX=97 StartY=28.6 StartZ=0 EndX=97 EndY=27.8 EndZ=0
    g2: LineSegment StartX=97 StartY=27.8 StartZ=0 EndX=108 EndY=27.8 EndZ=0
    g3: LineSegment StartX=108 StartY=27.8 StartZ=0 EndX=108 EndY=28.6 EndZ=0
    g4: LineSegment StartX=108 StartY=28.6 StartZ=0 EndX=97 EndY=28.6 EndZ=0
    g5: LineSegment StartX=97 StartY=35.8 StartZ=0 EndX=97 EndY=35 EndZ=0
    g6: LineSegment StartX=97 StartY=35 StartZ=0 EndX=108 EndY=35 EndZ=0
    g7: LineSegment StartX=108 StartY=35 StartZ=0 EndX=108 EndY=35.8 EndZ=0
    g8: LineSegment StartX=108 StartY=35.8 StartZ=0 EndX=97 EndY=35.8 EndZ=0
    g9: LineSegment StartX=97 StartY=30.4 StartZ=0 EndX=97 EndY=29.6 EndZ=0
    g10: LineSegment StartX=97 StartY=29.6 StartZ=0 EndX=108 EndY=29.6 EndZ=0
    g11: LineSegment StartX=108 StartY=29.6 StartZ=0 EndX=108 EndY=30.4 EndZ=0
    g12: LineSegment StartX=108 StartY=30.4 StartZ=0 EndX=97 EndY=30.4 EndZ=0
    g13: LineSegment StartX=97 StartY=34 StartZ=0 EndX=97 EndY=33.2 EndZ=0
    g14: LineSegment StartX=97 StartY=33.2 StartZ=0 EndX=108 EndY=33.2 EndZ=0
    g15: LineSegment StartX=108 StartY=33.2 StartZ=0 EndX=108 EndY=34 EndZ=0
    g16: LineSegment StartX=108 StartY=34 StartZ=0 EndX=97 EndY=34 EndZ=0
    g17: LineSegment StartX=97 StartY=32.2 StartZ=0 EndX=97 EndY=31.4 EndZ=0
    g18: LineSegment StartX=97 StartY=31.4 StartZ=0 EndX=108 EndY=31.4 EndZ=0
    g19: LineSegment StartX=108 StartY=31.4 StartZ=0 EndX=108 EndY=32.2 EndZ=0
    g20: LineSegment StartX=108 StartY=32.2 StartZ=0 EndX=97 EndY=32.2 EndZ=0
  constraints (54):
    c: Vertical(g0)
    c: PointOnObject(g0,g-3)
    c: PointOnObject(g0,g-4)
    c: DistanceX(g0,g-5) = 11
    c: Coincident(g1,g2)
    c: Coincident(g2,g3)
    c: Coincident(g3,g4)
    c: Coincident(g4,g1)
    c: Horizontal(g2)
    c: Horizontal(g4)
    c: Tangent(g1,g0)
    c: Tangent(g3,g-5)
    c: DistanceY(g2,g3) = 0.8
    c: Coincident(g5,g6)
    c: Coincident(g6,g7)
    c: Coincident(g7,g8)
    c: Coincident(g8,g5)
    c: Horizontal(g6)
    c: Horizontal(g8)
    c: DistanceY(g6,g7) = 0.8
    c: Coincident(g9,g10)
    c: Coincident(g10,g11)
    c: Coincident(g11,g12)
    c: Coincident(g12,g9)
    c: Horizontal(g10)
    c: Horizontal(g12)
    c: DistanceY(g10,g11) = 0.8
    c: Tangent(g5,g0)
    c: Tangent(g7,g-5)
    c: Tangent(g9,g0)
    c: Tangent(g11,g-5)
    c: Coincident(g13,g14)
    c: Coincident(g14,g15)
    c: Coincident(g15,g16)
    c: Coincident(g16,g13)
    c: Horizontal(g14)
    c: Horizontal(g16)
    c: DistanceY(g14,g15) = 0.8
    c: Tangent(g13,g0)
    c: Tangent(g15,g-5)
    c: Coincident(g17,g18)
    c: Coincident(g18,g19)
    c: Coincident(g19,g20)
    c: Coincident(g20,g17)
    c: Horizontal(g18)
    c: Horizontal(g20)
    c: DistanceY(g18,g19) = 0.8
    c: Tangent(g17,g0)
    c: Tangent(g19,g-5)
    c: DistanceY(g1,g9) = 1
    c: DistanceY(g9,g17) = 1
    c: DistanceY(g17,g13) = 1
    c: DistanceY(g13,g5) = 1
    c: DistanceY(g0,g1) = 1
FEATURE [PartDesign::Pocket] Pocket004
  BaseFeature = -> Chamfer005
  Direction = (0,-1,2e-16)
  Length = 1
  Length2 = 5
  Profile = -> Sketch111
  ReferenceAxis = -> Sketch111 [N_Axis]
  Refine = true
  Suppressed = false
  Type = 0
FEATURE [PartDesign::Pad] Pad010
  BaseFeature = -> Pocket004
  Direction = (0,1,-2e-16)
  Length = 1.2
  Length2 = 10
  Profile = -> Sketch098
  ReferenceAxis = -> Sketch098 [N_Axis]
  Refine = true
  Suppressed = false
  Type = 0
FEATURE [PartDesign::Chamfer] Chamfer006
  Angle = 45
  Base = -> Pad010 [Edge291]
  BaseFeature = -> Pad010
  ChamferType = 1
  FlipDirection = false
  Refine = true
  Size = 1
  Size2 = 6
  SupportTransform = false
  Suppressed = false
  UseAllEdges = false
FEATURE [Sketcher::SketchObject] Sketch110
  ArcFitTolerance = 1e-06
  AttachmentSupport = -> [Pad010]
  ExternalGeometry = -> [Sketch098]
  FullyConstrained = true
  MakeInternals = false
  MapMode = 5
  Placement = pos=(0,4,-9e-16) rot=(0,0.707107,0.707107;3.14159rad)
  sketch-geometry (8):
    g0: LineSegment StartX=119.69 StartY=34 StartZ=0 EndX=130.69 EndY=34 EndZ=0
    g1: LineSegment StartX=119.95 StartY=33.2 StartZ=0 EndX=130.95 EndY=33.2 EndZ=0
    g2: LineSegment StartX=119.137 StartY=35.7 StartZ=0 EndX=130.137 EndY=35.7 EndZ=0
    g3: LineSegment StartX=118.877 StartY=36.5 StartZ=0 EndX=129.877 EndY=36.5 EndZ=0
    g4: LineSegment StartX=118.877 StartY=36.5 StartZ=0 EndX=119.137 EndY=35.7 EndZ=0
    g5: LineSegment StartX=129.877 StartY=36.5 StartZ=0 EndX=130.137 EndY=35.7 EndZ=0
    g6: LineSegment StartX=119.69 StartY=34 StartZ=0 EndX=119.95 EndY=33.2 EndZ=0
    g7: LineSegment StartX=130.69 StartY=34 StartZ=0 EndX=130.95 EndY=33.2 EndZ=0
  constraints (24):
    c: Horizontal(g0)
    c: Horizontal(g1)
    c: Horizontal(g2)
    c: Horizontal(g3)
    c: Equal(g1,g-5)
    c: Equal(g0,g-5)
    c: Equal(g2,g-5)
    c: Equal(g3,g-5)
    c: PointOnObject(g0,g-3)
    c: PointOnObject(g1,g-3)
    c: PointOnObject(g2,g-3)
    c: PointOnObject(g3,g-3)
    c: Coincident(g4,g3)
    c: Coincident(g4,g2)
    c: Coincident(g5,g3)
    c: Coincident(g5,g2)
    c: Coincident(g6,g0)
    c: Coincident(g6,g1)
    c: Coincident(g7,g0)
    c: Coincident(g7,g1)
    c: DistanceY(g1,g0) = 0.8
    c: DistanceY(g2,g3) = 0.8
    c: DistanceY(g-5,g1) = 2
    c: DistanceY(g-5,g2) = 4.5
FEATURE [PartDesign::Pocket] Pocket003
  BaseFeature = -> Chamfer006
  Direction = (0,-1,2e-16)
  Length = 1
  Length2 = 5
  Profile = -> Sketch110
  ReferenceAxis = -> Sketch110 [N_Axis]
  Refine = true
  Suppressed = false
  Type = 0
FEATURE [PartDesign::SubtractivePipe] SubtractivePipe
  AuxilleryCurvelinear = true
  AuxillerySpineTangent = false
  BaseFeature = -> Pocket003
  Binormal = (0,0,0)
  Mode = 0
  Profile = -> Sketch106
  Refine = true
  Spine = -> Pad008 [Edge215]
  SpineTangent = false
  Suppressed = false
  Transformation = 0
  Transition = 0
FEATURE [PartDesign::SubtractivePipe] SubtractivePipe001
  AuxilleryCurvelinear = true
  AuxillerySpineTangent = false
  BaseFeature = -> SubtractivePipe
  Binormal = (0,0,0)
  Mode = 0
  Profile = -> Sketch107
  Refine = true
  Spine = -> Pad008 [Edge213,Edge216,Edge210]
  SpineTangent = false
  Suppressed = false
  Transformation = 0
  Transition = 0
FEATURE [PartDesign::SubtractiveLoft] SubtractiveLoft
  BaseFeature = -> SubtractivePipe001
  Closed = false
  Profile = -> Sketch099
  Refine = true
  Ruled = false
  Sections = -> [Sketch108]
  Suppressed = false
FEATURE [PartDesign::SubtractiveLoft] SubtractiveLoft001
  BaseFeature = -> SubtractiveLoft
  Closed = false
  Profile = -> Clone2D
  Refine = true
  Ruled = false
  Sections = -> [Sketch109]
  Suppressed = false
FEATURE [Sketcher::SketchObject] Sketch112
  ArcFitTolerance = 1e-06
  AttachmentSupport = -> [Pad008]
  ExternalGeometry = -> [Binder]
  FullyConstrained = true
  MakeInternals = false
  MapMode = 5
  Placement = pos=(0,3.6,0) rot=(0,0.707107,0.707107;3.14159rad)
  sketch-geometry (4):
    g0: LineSegment [constr] StartX=167.782 StartY=-53.0314 StartZ=0 EndX=215.42 EndY=-53.0314 EndZ=0
    g1: GeomPoint [constr] X=191.282 Y=-53.0314 Z=0
    g2: Circle CenterX=191.282 CenterY=-53.0314 CenterZ=0 NormalX=0 NormalY=0 NormalZ=1 AngleXU=0 Radius=11.5
    g3: Circle CenterX=191.282 CenterY=-53.0314 CenterZ=0 NormalX=0 NormalY=0 NormalZ=1 AngleXU=0 Radius=10.7
  constraints (9):
    c: Horizontal(g0)
    c: PointOnObject(g0,g-3)
    c: Diameter(g2) = 23
    c: Coincident(g2,g1)
    c: Diameter(g3) = 21.4
    c: Coincident(g3,g1)
    c: DistanceX(g0,g1) = 23.5
    c: PointOnObject(g1,g0)
    c: Coincident(g0,g-4)
FEATURE [PartDesign::Chamfer] Chamfer016
  Angle = 45
  Base = -> SubtractiveLoft001 [Edge118,Edge117,Edge119,Edge120,Edge109]
  BaseFeature = -> SubtractiveLoft001
  ChamferType = 0
  FlipDirection = false
  Refine = true
  Size = 1.5
  Size2 = 1
  SupportTransform = false
  Suppressed = false
  UseAllEdges = false
FEATURE [PartDesign::Chamfer] Chamfer017
  Angle = 45
  Base = -> Chamfer016 [Edge15]
  BaseFeature = -> Chamfer016
  ChamferType = 0
  FlipDirection = false
  Refine = true
  Size = 3.5
  Size2 = 1
  SupportTransform = false
  Suppressed = false
  UseAllEdges = false
FEATURE [PartDesign::Chamfer] Chamfer018
  Angle = 45
  Base = -> Chamfer017 [Edge10]
  BaseFeature = -> Chamfer017
  ChamferType = 0
  FlipDirection = false
  Refine = true
  Size = 3.5
  Size2 = 1
  SupportTransform = false
  Suppressed = false
  UseAllEdges = false
FEATURE [PartDesign::Chamfer] Chamfer019
  Angle = 45
  Base = -> Chamfer018 [Edge93,Edge140]
  BaseFeature = -> Chamfer018
  ChamferType = 0
  FlipDirection = false
  Refine = true
  Size = 1.9
  Size2 = 1
  SupportTransform = false
  Suppressed = false
  UseAllEdges = false
FEATURE [PartDesign::Fillet] Fillet009
  Base = -> Chamfer019 [Edge84]
  BaseFeature = -> Chamfer019
  Radius = 1.1
  Refine = true
  SupportTransform = false
  Suppressed = false
  UseAllEdges = false
FEATURE [PartDesign::Fillet] Fillet010
  Base = -> Fillet009 [Edge78]
  BaseFeature = -> Fillet009
  Radius = 1.9
  Refine = true
  SupportTransform = false
  Suppressed = false
  UseAllEdges = false
FEATURE [PartDesign::Pocket] Pocket005
  BaseFeature = -> Fillet010
  Direction = (0,-1,2e-16)
  Length = 0.8
  Length2 = 5
  Profile = -> Sketch112
  ReferenceAxis = -> Sketch112 [N_Axis]
  Refine = true
  Suppressed = false
  Type = 0
FEATURE [Part::Part2DObjectPython] ShapeString001  # Draft 2D object (typed FeaturePython)
  FontFile = <path>
  Fuse = false
  Justification = 6
  JustificationReference = 0
  KeepLeftMargin = false
  MakeFace = true
  ObliqueAngle = 0
  Placement = pos=(-183.5,3.6,-57.5) rot=(0,0.707107,0.707107;3.14159rad)
  ScaleToSize = true
  Size = 10
  String = AS
  Tracking = 0
FEATURE [PartDesign::Pocket] Pocket013
  BaseFeature = -> Pocket005
  Direction = (-1e-16,-1,2e-16)
  Length = 1
  Length2 = 5
  Profile = -> ShapeString001
  ReferenceAxis = -> ShapeString001 [N_Axis]
  Refine = true
  Suppressed = false
  Type = 0
FEATURE [PartDesign::Body] Body006  label="lato SX"
  AllowCompound = false
  Group = -> [Binder,Pad019,Chamfer015,Pocket002,Sketch133,Sketch091,Pad005,Sketch092,Pocket001,Sketch093,Sketch094,Pad006,Sketch095,Pad007,Sketch096,Pad008,Sketch097,Pad009,Chamfer005,Pocket004,Sketch098,Pad010,Chamfer006,Pocket003,SubtractivePipe,SubtractivePipe001,Sketch099,Sketch106,Sketch107,Sketch108,Clone2D,Sketch109,SubtractiveLoft,SubtractiveLoft001,Sketch110,Sketch111,Sketch112,Chamfer016,Chamfer017,+7 more]
  Origin = -> Origin006
  Tip = -> Pocket013
FEATURE [PartDesign::Pad] Pad020
  Direction = (0,-1,2e-16)
  Length = 25.2
  Length2 = 10
  Midplane = true
  Placement = pos=(0,0,0) rot=(1,0,0;1.5708rad)
  Profile = -> Sketch021
  ReferenceAxis = -> Sketch021 [N_Axis]
  Refine = true
  Suppressed = false
  Type = 0
FEATURE [PartDesign::Body] Body001  label="perno fermo rumble"
  AllowCompound = false
  Group = -> [Sketch021,Pad020]
  Origin = -> Origin001
  Tip = -> Pad020
note: 2 file-system paths scrubbed to <path> (originals preserved in the JSON sidecar)
